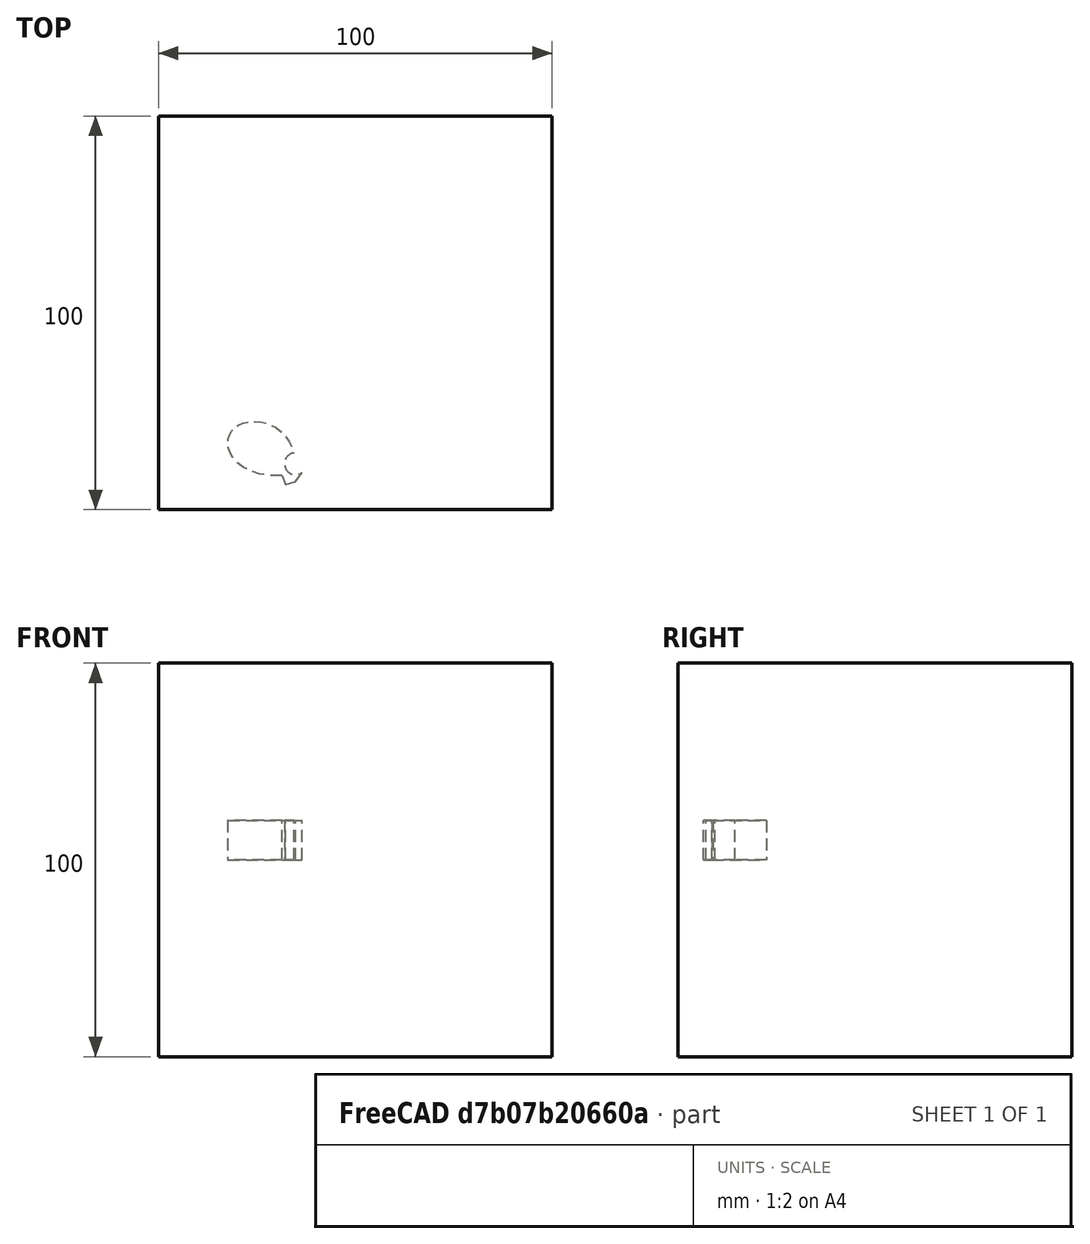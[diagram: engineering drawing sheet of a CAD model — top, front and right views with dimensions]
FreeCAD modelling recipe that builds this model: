
FCSTD DOCUMENT  (FreeCAD 0.19RUnknown)
Label: mirrorTest-3
License: All rights reserved
LicenseURL: http://en.wikipedia.org/wiki/All_rights_reserved
objects: App::DocumentObjectGroupPython×1248, Part::Mirroring×2, App::Part×2, Part::FeaturePython×1, Sketcher::SketchObject×1, Part::Extrusion×1
note: 5 computed .brp shape members not serialized (recipe doc carries the construction recipe); baked Part::Feature solids carry a one-line shape summary decoded from their .brp

FEATURE [App::DocumentObjectGroupPython] HALFPI  # scripted group (container) (typed FeaturePython)
  name = HALFPI
  value = pi/2.
FEATURE [App::DocumentObjectGroupPython] PI  # scripted group (container) (typed FeaturePython)
  name = PI
  value = 1.*pi
FEATURE [App::DocumentObjectGroupPython] TWOPI  # scripted group (container) (typed FeaturePython)
  name = TWOPI
  value = 2.*pi
FEATURE [App::DocumentObjectGroupPython] Constants  # scripted group (container) (typed FeaturePython)
  Group = -> [HALFPI,PI,TWOPI]
FEATURE [App::DocumentObjectGroupPython] Variables  # scripted group (container) (typed FeaturePython)
FEATURE [App::DocumentObjectGroupPython] Quantities  # scripted group (container) (typed FeaturePython)
FEATURE [App::DocumentObjectGroupPython] Isotopes  # scripted group (container) (typed FeaturePython)
FEATURE [App::DocumentObjectGroupPython] Elements  # scripted group (container) (typed FeaturePython)
FEATURE [App::DocumentObjectGroupPython] G4Isotopes  # scripted group (container) (typed FeaturePython)
FEATURE [App::DocumentObjectGroupPython] H_element  # scripted group (container) (typed FeaturePython)
  Z = 1
  atom_value = 1.008
  formula = H
  name = H_element
FEATURE [App::DocumentObjectGroupPython] He_element  # scripted group (container) (typed FeaturePython)
  Z = 2
  atom_value = 4.0026
  formula = He
  name = He_element
FEATURE [App::DocumentObjectGroupPython] Li_element  # scripted group (container) (typed FeaturePython)
  Z = 3
  atom_value = 6.94
  formula = Li
  name = Li_element
FEATURE [App::DocumentObjectGroupPython] Be_element  # scripted group (container) (typed FeaturePython)
  Z = 4
  atom_value = 9.01218
  formula = Be
  name = Be_element
FEATURE [App::DocumentObjectGroupPython] B_element  # scripted group (container) (typed FeaturePython)
  Z = 5
  atom_value = 10.81
  formula = B
  name = B_element
FEATURE [App::DocumentObjectGroupPython] C_element  # scripted group (container) (typed FeaturePython)
  Z = 6
  atom_value = 12.011
  formula = C
  name = C_element
FEATURE [App::DocumentObjectGroupPython] N_element  # scripted group (container) (typed FeaturePython)
  Z = 7
  atom_value = 14.007
  formula = N
  name = N_element
FEATURE [App::DocumentObjectGroupPython] O_element  # scripted group (container) (typed FeaturePython)
  Z = 8
  atom_value = 15.999
  formula = O
  name = O_element
FEATURE [App::DocumentObjectGroupPython] F_element  # scripted group (container) (typed FeaturePython)
  Z = 9
  atom_value = 18.9984
  formula = F
  name = F_element
FEATURE [App::DocumentObjectGroupPython] Ne_element  # scripted group (container) (typed FeaturePython)
  Z = 10
  atom_value = 20.1797
  formula = Ne
  name = Ne_element
FEATURE [App::DocumentObjectGroupPython] Na_element  # scripted group (container) (typed FeaturePython)
  Z = 11
  atom_value = 22.9898
  formula = Na
  name = Na_element
FEATURE [App::DocumentObjectGroupPython] Mg_element  # scripted group (container) (typed FeaturePython)
  Z = 12
  atom_value = 24.305
  formula = Mg
  name = Mg_element
FEATURE [App::DocumentObjectGroupPython] Al_element  # scripted group (container) (typed FeaturePython)
  Z = 13
  atom_value = 26.9815
  formula = Al
  name = Al_element
FEATURE [App::DocumentObjectGroupPython] Si_element  # scripted group (container) (typed FeaturePython)
  Z = 14
  atom_value = 28.085
  formula = Si
  name = Si_element
FEATURE [App::DocumentObjectGroupPython] P_element  # scripted group (container) (typed FeaturePython)
  Z = 15
  atom_value = 30.9738
  formula = P
  name = P_element
FEATURE [App::DocumentObjectGroupPython] S_element  # scripted group (container) (typed FeaturePython)
  Z = 16
  atom_value = 32.06
  formula = S
  name = S_element
FEATURE [App::DocumentObjectGroupPython] Cl_element  # scripted group (container) (typed FeaturePython)
  Z = 17
  atom_value = 35.45
  formula = Cl
  name = Cl_element
FEATURE [App::DocumentObjectGroupPython] Ar_element  # scripted group (container) (typed FeaturePython)
  Z = 18
  atom_value = 39.95
  formula = Ar
  name = Ar_element
FEATURE [App::DocumentObjectGroupPython] K_element  # scripted group (container) (typed FeaturePython)
  Z = 19
  atom_value = 39.0983
  formula = K
  name = K_element
FEATURE [App::DocumentObjectGroupPython] Ca_element  # scripted group (container) (typed FeaturePython)
  Z = 20
  atom_value = 40.078
  formula = Ca
  name = Ca_element
FEATURE [App::DocumentObjectGroupPython] Sc_element  # scripted group (container) (typed FeaturePython)
  Z = 21
  atom_value = 44.9559
  formula = Sc
  name = Sc_element
FEATURE [App::DocumentObjectGroupPython] Ti_element  # scripted group (container) (typed FeaturePython)
  Z = 22
  atom_value = 47.867
  formula = Ti
  name = Ti_element
FEATURE [App::DocumentObjectGroupPython] V_element  # scripted group (container) (typed FeaturePython)
  Z = 23
  atom_value = 50.9415
  formula = V
  name = V_element
FEATURE [App::DocumentObjectGroupPython] Cr_element  # scripted group (container) (typed FeaturePython)
  Z = 24
  atom_value = 51.9961
  formula = Cr
  name = Cr_element
FEATURE [App::DocumentObjectGroupPython] Mn_element  # scripted group (container) (typed FeaturePython)
  Z = 25
  atom_value = 54.938
  formula = Mn
  name = Mn_element
FEATURE [App::DocumentObjectGroupPython] Fe_element  # scripted group (container) (typed FeaturePython)
  Z = 26
  atom_value = 55.845
  formula = Fe
  name = Fe_element
FEATURE [App::DocumentObjectGroupPython] Co_element  # scripted group (container) (typed FeaturePython)
  Z = 27
  atom_value = 58.9332
  formula = Co
  name = Co_element
FEATURE [App::DocumentObjectGroupPython] Ni_element  # scripted group (container) (typed FeaturePython)
  Z = 28
  atom_value = 58.6934
  formula = Ni
  name = Ni_element
FEATURE [App::DocumentObjectGroupPython] Cu_element  # scripted group (container) (typed FeaturePython)
  Z = 29
  atom_value = 63.546
  formula = Cu
  name = Cu_element
FEATURE [App::DocumentObjectGroupPython] Zn_element  # scripted group (container) (typed FeaturePython)
  Z = 30
  atom_value = 65.38
  formula = Zn
  name = Zn_element
FEATURE [App::DocumentObjectGroupPython] Ga_element  # scripted group (container) (typed FeaturePython)
  Z = 31
  atom_value = 69.723
  formula = Ga
  name = Ga_element
FEATURE [App::DocumentObjectGroupPython] Ge_element  # scripted group (container) (typed FeaturePython)
  Z = 32
  atom_value = 72.63
  formula = Ge
  name = Ge_element
FEATURE [App::DocumentObjectGroupPython] As_element  # scripted group (container) (typed FeaturePython)
  Z = 33
  atom_value = 74.9216
  formula = As
  name = As_element
FEATURE [App::DocumentObjectGroupPython] Se_element  # scripted group (container) (typed FeaturePython)
  Z = 34
  atom_value = 78.971
  formula = Se
  name = Se_element
FEATURE [App::DocumentObjectGroupPython] Br_element  # scripted group (container) (typed FeaturePython)
  Z = 35
  atom_value = 79.904
  formula = Br
  name = Br_element
FEATURE [App::DocumentObjectGroupPython] Kr_element  # scripted group (container) (typed FeaturePython)
  Z = 36
  atom_value = 83.798
  formula = Kr
  name = Kr_element
FEATURE [App::DocumentObjectGroupPython] Rb_element  # scripted group (container) (typed FeaturePython)
  Z = 37
  atom_value = 85.4678
  formula = Rb
  name = Rb_element
FEATURE [App::DocumentObjectGroupPython] Sr_element  # scripted group (container) (typed FeaturePython)
  Z = 38
  atom_value = 87.62
  formula = Sr
  name = Sr_element
FEATURE [App::DocumentObjectGroupPython] Y_element  # scripted group (container) (typed FeaturePython)
  Z = 39
  atom_value = 88.9058
  formula = Y
  name = Y_element
FEATURE [App::DocumentObjectGroupPython] Zr_element  # scripted group (container) (typed FeaturePython)
  Z = 40
  atom_value = 91.224
  formula = Zr
  name = Zr_element
FEATURE [App::DocumentObjectGroupPython] Nb_element  # scripted group (container) (typed FeaturePython)
  Z = 41
  atom_value = 92.9064
  formula = Nb
  name = Nb_element
FEATURE [App::DocumentObjectGroupPython] Mo_element  # scripted group (container) (typed FeaturePython)
  Z = 42
  atom_value = 95.95
  formula = Mo
  name = Mo_element
FEATURE [App::DocumentObjectGroupPython] Tc_element  # scripted group (container) (typed FeaturePython)
  Z = 43
  atom_value = 97
  formula = Tc
  name = Tc_element
FEATURE [App::DocumentObjectGroupPython] Ru_element  # scripted group (container) (typed FeaturePython)
  Z = 44
  atom_value = 101.07
  formula = Ru
  name = Ru_element
FEATURE [App::DocumentObjectGroupPython] Rh_element  # scripted group (container) (typed FeaturePython)
  Z = 45
  atom_value = 102.905
  formula = Rh
  name = Rh_element
FEATURE [App::DocumentObjectGroupPython] Pd_element  # scripted group (container) (typed FeaturePython)
  Z = 46
  atom_value = 106.42
  formula = Pd
  name = Pd_element
FEATURE [App::DocumentObjectGroupPython] Ag_element  # scripted group (container) (typed FeaturePython)
  Z = 47
  atom_value = 107.868
  formula = Ag
  name = Ag_element
FEATURE [App::DocumentObjectGroupPython] Cd_element  # scripted group (container) (typed FeaturePython)
  Z = 48
  atom_value = 112.414
  formula = Cd
  name = Cd_element
FEATURE [App::DocumentObjectGroupPython] In_element  # scripted group (container) (typed FeaturePython)
  Z = 49
  atom_value = 114.818
  formula = In
  name = In_element
FEATURE [App::DocumentObjectGroupPython] Sn_element  # scripted group (container) (typed FeaturePython)
  Z = 50
  atom_value = 118.71
  formula = Sn
  name = Sn_element
FEATURE [App::DocumentObjectGroupPython] Sb_element  # scripted group (container) (typed FeaturePython)
  Z = 51
  atom_value = 121.76
  formula = Sb
  name = Sb_element
FEATURE [App::DocumentObjectGroupPython] Te_element  # scripted group (container) (typed FeaturePython)
  Z = 52
  atom_value = 127.6
  formula = Te
  name = Te_element
FEATURE [App::DocumentObjectGroupPython] I_element  # scripted group (container) (typed FeaturePython)
  Z = 53
  atom_value = 126.904
  formula = I
  name = I_element
FEATURE [App::DocumentObjectGroupPython] Xe_element  # scripted group (container) (typed FeaturePython)
  Z = 54
  atom_value = 131.293
  formula = Xe
  name = Xe_element
FEATURE [App::DocumentObjectGroupPython] Cs_element  # scripted group (container) (typed FeaturePython)
  Z = 55
  atom_value = 132.905
  formula = Cs
  name = Cs_element
FEATURE [App::DocumentObjectGroupPython] Ba_element  # scripted group (container) (typed FeaturePython)
  Z = 56
  atom_value = 137.327
  formula = Ba
  name = Ba_element
FEATURE [App::DocumentObjectGroupPython] La_element  # scripted group (container) (typed FeaturePython)
  Z = 57
  atom_value = 138.905
  formula = La
  name = La_element
FEATURE [App::DocumentObjectGroupPython] Ce_element  # scripted group (container) (typed FeaturePython)
  Z = 58
  atom_value = 140.116
  formula = Ce
  name = Ce_element
FEATURE [App::DocumentObjectGroupPython] Pr_element  # scripted group (container) (typed FeaturePython)
  Z = 59
  atom_value = 140.908
  formula = Pr
  name = Pr_element
FEATURE [App::DocumentObjectGroupPython] Nd_element  # scripted group (container) (typed FeaturePython)
  Z = 60
  atom_value = 144.242
  formula = Nd
  name = Nd_element
FEATURE [App::DocumentObjectGroupPython] Pm_element  # scripted group (container) (typed FeaturePython)
  Z = 61
  atom_value = 145
  formula = Pm
  name = Pm_element
FEATURE [App::DocumentObjectGroupPython] Sm_element  # scripted group (container) (typed FeaturePython)
  Z = 62
  atom_value = 150.36
  formula = Sm
  name = Sm_element
FEATURE [App::DocumentObjectGroupPython] Eu_element  # scripted group (container) (typed FeaturePython)
  Z = 63
  atom_value = 151.964
  formula = Eu
  name = Eu_element
FEATURE [App::DocumentObjectGroupPython] Gd_element  # scripted group (container) (typed FeaturePython)
  Z = 64
  atom_value = 157.25
  formula = Gd
  name = Gd_element
FEATURE [App::DocumentObjectGroupPython] Tb_element  # scripted group (container) (typed FeaturePython)
  Z = 65
  atom_value = 158.925
  formula = Tb
  name = Tb_element
FEATURE [App::DocumentObjectGroupPython] Dy_element  # scripted group (container) (typed FeaturePython)
  Z = 66
  atom_value = 162.5
  formula = Dy
  name = Dy_element
FEATURE [App::DocumentObjectGroupPython] Ho_element  # scripted group (container) (typed FeaturePython)
  Z = 67
  atom_value = 164.93
  formula = Ho
  name = Ho_element
FEATURE [App::DocumentObjectGroupPython] Er_element  # scripted group (container) (typed FeaturePython)
  Z = 68
  atom_value = 167.259
  formula = Er
  name = Er_element
FEATURE [App::DocumentObjectGroupPython] Tm_element  # scripted group (container) (typed FeaturePython)
  Z = 69
  atom_value = 168.934
  formula = Tm
  name = Tm_element
FEATURE [App::DocumentObjectGroupPython] Yb_element  # scripted group (container) (typed FeaturePython)
  Z = 70
  atom_value = 173.045
  formula = Yb
  name = Yb_element
FEATURE [App::DocumentObjectGroupPython] Lu_element  # scripted group (container) (typed FeaturePython)
  Z = 71
  atom_value = 174.967
  formula = Lu
  name = Lu_element
FEATURE [App::DocumentObjectGroupPython] Hf_element  # scripted group (container) (typed FeaturePython)
  Z = 72
  atom_value = 178.49
  formula = Hf
  name = Hf_element
FEATURE [App::DocumentObjectGroupPython] Ta_element  # scripted group (container) (typed FeaturePython)
  Z = 73
  atom_value = 180.948
  formula = Ta
  name = Ta_element
FEATURE [App::DocumentObjectGroupPython] W_element  # scripted group (container) (typed FeaturePython)
  Z = 74
  atom_value = 183.84
  formula = W
  name = W_element
FEATURE [App::DocumentObjectGroupPython] Re_element  # scripted group (container) (typed FeaturePython)
  Z = 75
  atom_value = 186.207
  formula = Re
  name = Re_element
FEATURE [App::DocumentObjectGroupPython] Os_element  # scripted group (container) (typed FeaturePython)
  Z = 76
  atom_value = 190.23
  formula = Os
  name = Os_element
FEATURE [App::DocumentObjectGroupPython] Ir_element  # scripted group (container) (typed FeaturePython)
  Z = 77
  atom_value = 192.217
  formula = Ir
  name = Ir_element
FEATURE [App::DocumentObjectGroupPython] Pt_element  # scripted group (container) (typed FeaturePython)
  Z = 78
  atom_value = 195.084
  formula = Pt
  name = Pt_element
FEATURE [App::DocumentObjectGroupPython] Au_element  # scripted group (container) (typed FeaturePython)
  Z = 79
  atom_value = 196.967
  formula = Au
  name = Au_element
FEATURE [App::DocumentObjectGroupPython] Hg_element  # scripted group (container) (typed FeaturePython)
  Z = 80
  atom_value = 200.592
  formula = Hg
  name = Hg_element
FEATURE [App::DocumentObjectGroupPython] Tl_element  # scripted group (container) (typed FeaturePython)
  Z = 81
  atom_value = 204.38
  formula = Tl
  name = Tl_element
FEATURE [App::DocumentObjectGroupPython] Pb_element  # scripted group (container) (typed FeaturePython)
  Z = 82
  atom_value = 207.2
  formula = Pb
  name = Pb_element
FEATURE [App::DocumentObjectGroupPython] Bi_element  # scripted group (container) (typed FeaturePython)
  Z = 83
  atom_value = 208.98
  formula = Bi
  name = Bi_element
FEATURE [App::DocumentObjectGroupPython] Po_element  # scripted group (container) (typed FeaturePython)
  Z = 84
  atom_value = 209
  formula = Po
  name = Po_element
FEATURE [App::DocumentObjectGroupPython] At_element  # scripted group (container) (typed FeaturePython)
  Z = 85
  atom_value = 210
  formula = At
  name = At_element
FEATURE [App::DocumentObjectGroupPython] Rn_element  # scripted group (container) (typed FeaturePython)
  Z = 86
  atom_value = 222
  formula = Rn
  name = Rn_element
FEATURE [App::DocumentObjectGroupPython] Fr_element  # scripted group (container) (typed FeaturePython)
  Z = 87
  atom_value = 223
  formula = Fr
  name = Fr_element
FEATURE [App::DocumentObjectGroupPython] Ra_element  # scripted group (container) (typed FeaturePython)
  Z = 88
  atom_value = 226
  formula = Ra
  name = Ra_element
FEATURE [App::DocumentObjectGroupPython] Ac_element  # scripted group (container) (typed FeaturePython)
  Z = 89
  atom_value = 227
  formula = Ac
  name = Ac_element
FEATURE [App::DocumentObjectGroupPython] Th_element  # scripted group (container) (typed FeaturePython)
  Z = 90
  atom_value = 232.038
  formula = Th
  name = Th_element
FEATURE [App::DocumentObjectGroupPython] Pa_element  # scripted group (container) (typed FeaturePython)
  Z = 91
  atom_value = 231.036
  formula = Pa
  name = Pa_element
FEATURE [App::DocumentObjectGroupPython] U_element  # scripted group (container) (typed FeaturePython)
  Z = 92
  atom_value = 238.029
  formula = U
  name = U_element
FEATURE [App::DocumentObjectGroupPython] Np_element  # scripted group (container) (typed FeaturePython)
  Z = 93
  atom_value = 237
  formula = Np
  name = Np_element
FEATURE [App::DocumentObjectGroupPython] Pu_element  # scripted group (container) (typed FeaturePython)
  Z = 94
  atom_value = 244
  formula = Pu
  name = Pu_element
FEATURE [App::DocumentObjectGroupPython] Am_element  # scripted group (container) (typed FeaturePython)
  Z = 95
  atom_value = 243
  formula = Am
  name = Am_element
FEATURE [App::DocumentObjectGroupPython] Cm_element  # scripted group (container) (typed FeaturePython)
  Z = 96
  atom_value = 247
  formula = Cm
  name = Cm_element
FEATURE [App::DocumentObjectGroupPython] Bk_element  # scripted group (container) (typed FeaturePython)
  Z = 97
  atom_value = 247
  formula = Bk
  name = Bk_element
FEATURE [App::DocumentObjectGroupPython] Cf_element  # scripted group (container) (typed FeaturePython)
  Z = 98
  atom_value = 251
  formula = Cf
  name = Cf_element
FEATURE [App::DocumentObjectGroupPython] G4Elements  # scripted group (container) (typed FeaturePython)
  Group = -> [H_element,He_element,Li_element,Be_element,B_element,C_element,N_element,O_element,F_element,Ne_element,Na_element,Mg_element,Al_element,Si_element,P_element,S_element,Cl_element,Ar_element,K_element,Ca_element,Sc_element,Ti_element,V_element,Cr_element,Mn_element,Fe_element,Co_element,Ni_element,Cu_element,Zn_element,Ga_element,Ge_element,As_element,Se_element,Br_element,Kr_element,Rb_element,+61 more]
FEATURE [App::DocumentObjectGroupPython] H_element001  label="H_element : 0.101"  # scripted group (container) (typed FeaturePython)
  n = 0.101327
FEATURE [App::DocumentObjectGroupPython] C_element001  label="C_element : 0.775"  # scripted group (container) (typed FeaturePython)
  n = 0.7755
FEATURE [App::DocumentObjectGroupPython] N_element001  label="N_element : 0.035"  # scripted group (container) (typed FeaturePython)
  n = 0.035057
FEATURE [App::DocumentObjectGroupPython] O_element001  label="O_element : 0.052"  # scripted group (container) (typed FeaturePython)
  n = 0.0523159
FEATURE [App::DocumentObjectGroupPython] F_element001  label="F_element : 0.017"  # scripted group (container) (typed FeaturePython)
  n = 0.017422
FEATURE [App::DocumentObjectGroupPython] Ca_element001  label="Ca_element : 0.018"  # scripted group (container) (typed FeaturePython)
  n = 0.018378
FEATURE [App::DocumentObjectGroupPython] G4_A_150_TISSUE  label="G4_A-150_TISSUE"  # scripted group (container) (typed FeaturePython)
  Dunit = g/cm3
  Dvalue = 1.127
  Group = -> [H_element001,C_element001,N_element001,O_element001,F_element001,Ca_element001]
  conduct = 2
  density = 1
  expand = 3
  formula = G4_A-150_TISSUE
  name = G4_A-150_TISSUE
  specific = 4
FEATURE [App::DocumentObjectGroupPython] C_element002  label="C_element : 3"  # scripted group (container) (typed FeaturePython)
  n = 3
  ref = C_element
FEATURE [App::DocumentObjectGroupPython] H_element002  label="H_element : 6"  # scripted group (container) (typed FeaturePython)
  n = 6
  ref = H_element
FEATURE [App::DocumentObjectGroupPython] O_element002  label="O_element : 1"  # scripted group (container) (typed FeaturePython)
  n = 1
  ref = O_element
FEATURE [App::DocumentObjectGroupPython] G4_ACETONE  # scripted group (container) (typed FeaturePython)
  Dunit = g/cm3
  Dvalue = 0.7899
  Group = -> [C_element002,H_element002,O_element002]
  conduct = 2
  density = 1
  expand = 3
  formula = G4_ACETONE
  name = G4_ACETONE
  specific = 4
FEATURE [App::DocumentObjectGroupPython] C_element003  label="C_element : 2"  # scripted group (container) (typed FeaturePython)
  n = 2
  ref = C_element
FEATURE [App::DocumentObjectGroupPython] H_element003  label="H_element : 2"  # scripted group (container) (typed FeaturePython)
  n = 2
  ref = H_element
FEATURE [App::DocumentObjectGroupPython] G4_ACETYLENE  # scripted group (container) (typed FeaturePython)
  Dunit = g/cm3
  Dvalue = 0.0010967
  Group = -> [C_element003,H_element003]
  conduct = 2
  density = 1
  expand = 3
  formula = G4_ACETYLENE
  name = G4_ACETYLENE
  specific = 4
FEATURE [App::DocumentObjectGroupPython] C_element004  label="C_element : 5"  # scripted group (container) (typed FeaturePython)
  n = 5
  ref = C_element
FEATURE [App::DocumentObjectGroupPython] H_element004  label="H_element : 5"  # scripted group (container) (typed FeaturePython)
  n = 5
  ref = H_element
FEATURE [App::DocumentObjectGroupPython] N_element002  label="N_element : 5"  # scripted group (container) (typed FeaturePython)
  n = 5
  ref = N_element
FEATURE [App::DocumentObjectGroupPython] G4_ADENINE  # scripted group (container) (typed FeaturePython)
  Dunit = g/cm3
  Dvalue = 1.6
  Group = -> [C_element004,H_element004,N_element002]
  conduct = 2
  density = 1
  expand = 3
  formula = G4_ADENINE
  name = G4_ADENINE
  specific = 4
FEATURE [App::DocumentObjectGroupPython] H_element005  label="H_element : 0.114"  # scripted group (container) (typed FeaturePython)
  n = 0.114
FEATURE [App::DocumentObjectGroupPython] C_element005  label="C_element : 0.598"  # scripted group (container) (typed FeaturePython)
  n = 0.598
FEATURE [App::DocumentObjectGroupPython] N_element003  label="N_element : 0.007"  # scripted group (container) (typed FeaturePython)
  n = 0.007
FEATURE [App::DocumentObjectGroupPython] O_element003  label="O_element : 0.278"  # scripted group (container) (typed FeaturePython)
  n = 0.278
FEATURE [App::DocumentObjectGroupPython] Na_element001  label="Na_element : 0.001"  # scripted group (container) (typed FeaturePython)
  n = 0.001
FEATURE [App::DocumentObjectGroupPython] S_element001  label="S_element : 0.001"  # scripted group (container) (typed FeaturePython)
  n = 0.001
FEATURE [App::DocumentObjectGroupPython] Cl_element001  label="Cl_element : 0.001"  # scripted group (container) (typed FeaturePython)
  n = 0.001
FEATURE [App::DocumentObjectGroupPython] G4_ADIPOSE_TISSUE_ICRP  # scripted group (container) (typed FeaturePython)
  Dunit = g/cm3
  Dvalue = 0.95
  Group = -> [H_element005,C_element005,N_element003,O_element003,Na_element001,S_element001,Cl_element001]
  conduct = 2
  density = 1
  expand = 3
  formula = G4_ADIPOSE_TISSUE_ICRP
  name = G4_ADIPOSE_TISSUE_ICRP
  specific = 4
FEATURE [App::DocumentObjectGroupPython] C_element006  label="C_element : 0.000"  # scripted group (container) (typed FeaturePython)
  n = 0.000124
FEATURE [App::DocumentObjectGroupPython] N_element004  label="N_element : 0.755"  # scripted group (container) (typed FeaturePython)
  n = 0.755268
FEATURE [App::DocumentObjectGroupPython] O_element004  label="O_element : 0.232"  # scripted group (container) (typed FeaturePython)
  n = 0.231781
FEATURE [App::DocumentObjectGroupPython] Ar_element001  label="Ar_element : 0.013"  # scripted group (container) (typed FeaturePython)
  n = 0.012827
FEATURE [App::DocumentObjectGroupPython] G4_AIR  # scripted group (container) (typed FeaturePython)
  Dunit = g/cm3
  Dvalue = 0.00120479
  Group = -> [C_element006,N_element004,O_element004,Ar_element001]
  conduct = 2
  density = 1
  expand = 3
  formula = G4_AIR
  name = G4_AIR
  specific = 4
FEATURE [App::DocumentObjectGroupPython] C_element007  label="C_element : 006"  # scripted group (container) (typed FeaturePython)
  n = 3
  ref = C_element
FEATURE [App::DocumentObjectGroupPython] H_element006  label="H_element : 7"  # scripted group (container) (typed FeaturePython)
  n = 7
  ref = H_element
FEATURE [App::DocumentObjectGroupPython] N_element005  label="N_element : 1"  # scripted group (container) (typed FeaturePython)
  n = 1
  ref = N_element
FEATURE [App::DocumentObjectGroupPython] O_element005  label="O_element : 2"  # scripted group (container) (typed FeaturePython)
  n = 2
  ref = O_element
FEATURE [App::DocumentObjectGroupPython] G4_ALANINE  # scripted group (container) (typed FeaturePython)
  Dunit = g/cm3
  Dvalue = 1.42
  Group = -> [C_element007,H_element006,N_element005,O_element005]
  conduct = 2
  density = 1
  expand = 3
  formula = G4_ALANINE
  name = G4_ALANINE
  specific = 4
FEATURE [App::DocumentObjectGroupPython] Al_element001  label="Al_element : 2"  # scripted group (container) (typed FeaturePython)
  n = 2
  ref = Al_element
FEATURE [App::DocumentObjectGroupPython] O_element006  label="O_element : 3"  # scripted group (container) (typed FeaturePython)
  n = 3
  ref = O_element
FEATURE [App::DocumentObjectGroupPython] G4_ALUMINUM_OXIDE  # scripted group (container) (typed FeaturePython)
  Dunit = g/cm3
  Dvalue = 3.97
  Group = -> [Al_element001,O_element006]
  conduct = 2
  density = 1
  expand = 3
  formula = G4_ALUMINUM_OXIDE
  name = G4_ALUMINUM_OXIDE
  specific = 4
FEATURE [App::DocumentObjectGroupPython] H_element007  label="H_element : 0.106"  # scripted group (container) (typed FeaturePython)
  n = 0.10593
FEATURE [App::DocumentObjectGroupPython] C_element008  label="C_element : 0.789"  # scripted group (container) (typed FeaturePython)
  n = 0.788974
FEATURE [App::DocumentObjectGroupPython] O_element007  label="O_element : 0.105"  # scripted group (container) (typed FeaturePython)
  n = 0.105096
FEATURE [App::DocumentObjectGroupPython] G4_AMBER  # scripted group (container) (typed FeaturePython)
  Dunit = g/cm3
  Dvalue = 1.1
  Group = -> [H_element007,C_element008,O_element007]
  conduct = 2
  density = 1
  expand = 3
  formula = G4_AMBER
  name = G4_AMBER
  specific = 4
FEATURE [App::DocumentObjectGroupPython] N_element006  label="N_element : 006"  # scripted group (container) (typed FeaturePython)
  n = 1
  ref = N_element
FEATURE [App::DocumentObjectGroupPython] H_element008  label="H_element : 3"  # scripted group (container) (typed FeaturePython)
  n = 3
  ref = H_element
FEATURE [App::DocumentObjectGroupPython] G4_AMMONIA  # scripted group (container) (typed FeaturePython)
  Dunit = g/cm3
  Dvalue = 0.000826019
  Group = -> [N_element006,H_element008]
  conduct = 2
  density = 1
  expand = 3
  formula = G4_AMMONIA
  name = G4_AMMONIA
  specific = 4
FEATURE [App::DocumentObjectGroupPython] C_element009  label="C_element : 6"  # scripted group (container) (typed FeaturePython)
  n = 6
  ref = C_element
FEATURE [App::DocumentObjectGroupPython] H_element009  label="H_element : 008"  # scripted group (container) (typed FeaturePython)
  n = 7
  ref = H_element
FEATURE [App::DocumentObjectGroupPython] N_element007  label="N_element : 007"  # scripted group (container) (typed FeaturePython)
  n = 1
  ref = N_element
FEATURE [App::DocumentObjectGroupPython] G4_ANILINE  # scripted group (container) (typed FeaturePython)
  Dunit = g/cm3
  Dvalue = 1.0235
  Group = -> [C_element009,H_element009,N_element007]
  conduct = 2
  density = 1
  expand = 3
  formula = G4_ANILINE
  name = G4_ANILINE
  specific = 4
FEATURE [App::DocumentObjectGroupPython] C_element010  label="C_element : 14"  # scripted group (container) (typed FeaturePython)
  n = 14
  ref = C_element
FEATURE [App::DocumentObjectGroupPython] H_element010  label="H_element : 10"  # scripted group (container) (typed FeaturePython)
  n = 10
  ref = H_element
FEATURE [App::DocumentObjectGroupPython] G4_ANTHRACENE  # scripted group (container) (typed FeaturePython)
  Dunit = g/cm3
  Dvalue = 1.283
  Group = -> [C_element010,H_element010]
  conduct = 2
  density = 1
  expand = 3
  formula = G4_ANTHRACENE
  name = G4_ANTHRACENE
  specific = 4
FEATURE [App::DocumentObjectGroupPython] H_element011  label="H_element : 0.065"  # scripted group (container) (typed FeaturePython)
  n = 0.0654709
FEATURE [App::DocumentObjectGroupPython] C_element011  label="C_element : 0.537"  # scripted group (container) (typed FeaturePython)
  n = 0.536944
FEATURE [App::DocumentObjectGroupPython] N_element008  label="N_element : 0.021"  # scripted group (container) (typed FeaturePython)
  n = 0.0215
FEATURE [App::DocumentObjectGroupPython] O_element008  label="O_element : 0.032"  # scripted group (container) (typed FeaturePython)
  n = 0.032085
FEATURE [App::DocumentObjectGroupPython] F_element002  label="F_element : 0.167"  # scripted group (container) (typed FeaturePython)
  n = 0.167411
FEATURE [App::DocumentObjectGroupPython] Ca_element002  label="Ca_element : 0.177"  # scripted group (container) (typed FeaturePython)
  n = 0.176589
FEATURE [App::DocumentObjectGroupPython] G4_B_100_BONE  label="G4_B-100_BONE"  # scripted group (container) (typed FeaturePython)
  Dunit = g/cm3
  Dvalue = 1.45
  Group = -> [H_element011,C_element011,N_element008,O_element008,F_element002,Ca_element002]
  conduct = 2
  density = 1
  expand = 3
  formula = G4_B-100_BONE
  name = G4_B-100_BONE
  specific = 4
FEATURE [App::DocumentObjectGroupPython] H_element012  label="H_element : 0.057"  # scripted group (container) (typed FeaturePython)
  n = 0.057441
FEATURE [App::DocumentObjectGroupPython] C_element012  label="C_element : 0.790"  # scripted group (container) (typed FeaturePython)
  n = 0.774591
FEATURE [App::DocumentObjectGroupPython] O_element009  label="O_element : 0.168"  # scripted group (container) (typed FeaturePython)
  n = 0.167968
FEATURE [App::DocumentObjectGroupPython] G4_BAKELITE  # scripted group (container) (typed FeaturePython)
  Dunit = g/cm3
  Dvalue = 1.25
  Group = -> [H_element012,C_element012,O_element009]
  conduct = 2
  density = 1
  expand = 3
  formula = G4_BAKELITE
  name = G4_BAKELITE
  specific = 4
FEATURE [App::DocumentObjectGroupPython] Ba_element001  label="Ba_element : 1"  # scripted group (container) (typed FeaturePython)
  n = 1
  ref = Ba_element
FEATURE [App::DocumentObjectGroupPython] F_element003  label="F_element : 2"  # scripted group (container) (typed FeaturePython)
  n = 2
  ref = F_element
FEATURE [App::DocumentObjectGroupPython] G4_BARIUM_FLUORIDE  # scripted group (container) (typed FeaturePython)
  Dunit = g/cm3
  Dvalue = 4.89
  Group = -> [Ba_element001,F_element003]
  conduct = 2
  density = 1
  expand = 3
  formula = G4_BARIUM_FLUORIDE
  name = G4_BARIUM_FLUORIDE
  specific = 4
FEATURE [App::DocumentObjectGroupPython] Ba_element002  label="Ba_element : 002"  # scripted group (container) (typed FeaturePython)
  n = 1
  ref = Ba_element
FEATURE [App::DocumentObjectGroupPython] S_element002  label="S_element : 1"  # scripted group (container) (typed FeaturePython)
  n = 1
  ref = S_element
FEATURE [App::DocumentObjectGroupPython] O_element010  label="O_element : 4"  # scripted group (container) (typed FeaturePython)
  n = 4
  ref = O_element
FEATURE [App::DocumentObjectGroupPython] G4_BARIUM_SULFATE  # scripted group (container) (typed FeaturePython)
  Dunit = g/cm3
  Dvalue = 4.5
  Group = -> [Ba_element002,S_element002,O_element010]
  conduct = 2
  density = 1
  expand = 3
  formula = G4_BARIUM_SULFATE
  name = G4_BARIUM_SULFATE
  specific = 4
FEATURE [App::DocumentObjectGroupPython] C_element013  label="C_element : 007"  # scripted group (container) (typed FeaturePython)
  n = 6
  ref = C_element
FEATURE [App::DocumentObjectGroupPython] H_element013  label="H_element : 009"  # scripted group (container) (typed FeaturePython)
  n = 6
  ref = H_element
FEATURE [App::DocumentObjectGroupPython] G4_BENZENE  # scripted group (container) (typed FeaturePython)
  Dunit = g/cm3
  Dvalue = 0.87865
  Group = -> [C_element013,H_element013]
  conduct = 2
  density = 1
  expand = 3
  formula = G4_BENZENE
  name = G4_BENZENE
  specific = 4
FEATURE [App::DocumentObjectGroupPython] Be_element001  label="Be_element : 1"  # scripted group (container) (typed FeaturePython)
  n = 1
  ref = Be_element
FEATURE [App::DocumentObjectGroupPython] O_element011  label="O_element : 005"  # scripted group (container) (typed FeaturePython)
  n = 1
  ref = O_element
FEATURE [App::DocumentObjectGroupPython] G4_BERYLLIUM_OXIDE  # scripted group (container) (typed FeaturePython)
  Dunit = g/cm3
  Dvalue = 3.01
  Group = -> [Be_element001,O_element011]
  conduct = 2
  density = 1
  expand = 3
  formula = G4_BERYLLIUM_OXIDE
  name = G4_BERYLLIUM_OXIDE
  specific = 4
FEATURE [App::DocumentObjectGroupPython] Bi_element001  label="Bi_element : 4"  # scripted group (container) (typed FeaturePython)
  n = 4
  ref = Bi_element
FEATURE [App::DocumentObjectGroupPython] Ge_element001  label="Ge_element : 3"  # scripted group (container) (typed FeaturePython)
  n = 3
  ref = Ge_element
FEATURE [App::DocumentObjectGroupPython] O_element012  label="O_element : 12"  # scripted group (container) (typed FeaturePython)
  n = 12
  ref = O_element
FEATURE [App::DocumentObjectGroupPython] G4_BGO  # scripted group (container) (typed FeaturePython)
  Dunit = g/cm3
  Dvalue = 7.13
  Group = -> [Bi_element001,Ge_element001,O_element012]
  conduct = 2
  density = 1
  expand = 3
  formula = G4_BGO
  name = G4_BGO
  specific = 4
FEATURE [App::DocumentObjectGroupPython] H_element014  label="H_element : 0.102"  # scripted group (container) (typed FeaturePython)
  n = 0.102
FEATURE [App::DocumentObjectGroupPython] C_element014  label="C_element : 0.110"  # scripted group (container) (typed FeaturePython)
  n = 0.11
FEATURE [App::DocumentObjectGroupPython] N_element009  label="N_element : 0.033"  # scripted group (container) (typed FeaturePython)
  n = 0.033
FEATURE [App::DocumentObjectGroupPython] O_element013  label="O_element : 0.745"  # scripted group (container) (typed FeaturePython)
  n = 0.745
FEATURE [App::DocumentObjectGroupPython] Na_element002  label="Na_element : 0.002"  # scripted group (container) (typed FeaturePython)
  n = 0.001
FEATURE [App::DocumentObjectGroupPython] P_element001  label="P_element : 0.001"  # scripted group (container) (typed FeaturePython)
  n = 0.001
FEATURE [App::DocumentObjectGroupPython] S_element003  label="S_element : 0.002"  # scripted group (container) (typed FeaturePython)
  n = 0.002
FEATURE [App::DocumentObjectGroupPython] Cl_element002  label="Cl_element : 0.003"  # scripted group (container) (typed FeaturePython)
  n = 0.003
FEATURE [App::DocumentObjectGroupPython] K_element001  label="K_element : 0.002"  # scripted group (container) (typed FeaturePython)
  n = 0.002
FEATURE [App::DocumentObjectGroupPython] Fe_element001  label="Fe_element : 0.001"  # scripted group (container) (typed FeaturePython)
  n = 0.001
FEATURE [App::DocumentObjectGroupPython] G4_BLOOD_ICRP  # scripted group (container) (typed FeaturePython)
  Dunit = g/cm3
  Dvalue = 1.06
  Group = -> [H_element014,C_element014,N_element009,O_element013,Na_element002,P_element001,S_element003,Cl_element002,K_element001,Fe_element001]
  conduct = 2
  density = 1
  expand = 3
  formula = G4_BLOOD_ICRP
  name = G4_BLOOD_ICRP
  specific = 4
FEATURE [App::DocumentObjectGroupPython] H_element015  label="H_element : 0.064"  # scripted group (container) (typed FeaturePython)
  n = 0.064
FEATURE [App::DocumentObjectGroupPython] C_element015  label="C_element : 0.278"  # scripted group (container) (typed FeaturePython)
  n = 0.278
FEATURE [App::DocumentObjectGroupPython] N_element010  label="N_element : 0.027"  # scripted group (container) (typed FeaturePython)
  n = 0.027
FEATURE [App::DocumentObjectGroupPython] O_element014  label="O_element : 0.410"  # scripted group (container) (typed FeaturePython)
  n = 0.41
FEATURE [App::DocumentObjectGroupPython] Mg_element001  label="Mg_element : 0.002"  # scripted group (container) (typed FeaturePython)
  n = 0.002
FEATURE [App::DocumentObjectGroupPython] P_element002  label="P_element : 0.070"  # scripted group (container) (typed FeaturePython)
  n = 0.07
FEATURE [App::DocumentObjectGroupPython] S_element004  label="S_element : 0.003"  # scripted group (container) (typed FeaturePython)
  n = 0.002
FEATURE [App::DocumentObjectGroupPython] Ca_element003  label="Ca_element : 0.147"  # scripted group (container) (typed FeaturePython)
  n = 0.147
FEATURE [App::DocumentObjectGroupPython] G4_BONE_COMPACT_ICRU  # scripted group (container) (typed FeaturePython)
  Dunit = g/cm3
  Dvalue = 1.85
  Group = -> [H_element015,C_element015,N_element010,O_element014,Mg_element001,P_element002,S_element004,Ca_element003]
  conduct = 2
  density = 1
  expand = 3
  formula = G4_BONE_COMPACT_ICRU
  name = G4_BONE_COMPACT_ICRU
  specific = 4
FEATURE [App::DocumentObjectGroupPython] H_element016  label="H_element : 0.034"  # scripted group (container) (typed FeaturePython)
  n = 0.034
FEATURE [App::DocumentObjectGroupPython] C_element016  label="C_element : 0.155"  # scripted group (container) (typed FeaturePython)
  n = 0.155
FEATURE [App::DocumentObjectGroupPython] N_element011  label="N_element : 0.042"  # scripted group (container) (typed FeaturePython)
  n = 0.042
FEATURE [App::DocumentObjectGroupPython] O_element015  label="O_element : 0.435"  # scripted group (container) (typed FeaturePython)
  n = 0.435
FEATURE [App::DocumentObjectGroupPython] Na_element003  label="Na_element : 0.003"  # scripted group (container) (typed FeaturePython)
  n = 0.001
FEATURE [App::DocumentObjectGroupPython] Mg_element002  label="Mg_element : 0.003"  # scripted group (container) (typed FeaturePython)
  n = 0.002
FEATURE [App::DocumentObjectGroupPython] P_element003  label="P_element : 0.103"  # scripted group (container) (typed FeaturePython)
  n = 0.103
FEATURE [App::DocumentObjectGroupPython] S_element005  label="S_element : 0.004"  # scripted group (container) (typed FeaturePython)
  n = 0.003
FEATURE [App::DocumentObjectGroupPython] Ca_element004  label="Ca_element : 0.225"  # scripted group (container) (typed FeaturePython)
  n = 0.225
FEATURE [App::DocumentObjectGroupPython] G4_BONE_CORTICAL_ICRP  # scripted group (container) (typed FeaturePython)
  Dunit = g/cm3
  Dvalue = 1.92
  Group = -> [H_element016,C_element016,N_element011,O_element015,Na_element003,Mg_element002,P_element003,S_element005,Ca_element004]
  conduct = 2
  density = 1
  expand = 3
  formula = G4_BONE_CORTICAL_ICRP
  name = G4_BONE_CORTICAL_ICRP
  specific = 4
FEATURE [App::DocumentObjectGroupPython] B_element001  label="B_element : 4"  # scripted group (container) (typed FeaturePython)
  n = 4
  ref = B_element
FEATURE [App::DocumentObjectGroupPython] C_element017  label="C_element : 1"  # scripted group (container) (typed FeaturePython)
  n = 1
  ref = C_element
FEATURE [App::DocumentObjectGroupPython] G4_BORON_CARBIDE  # scripted group (container) (typed FeaturePython)
  Dunit = g/cm3
  Dvalue = 2.52
  Group = -> [B_element001,C_element017]
  conduct = 2
  density = 1
  expand = 3
  formula = G4_BORON_CARBIDE
  name = G4_BORON_CARBIDE
  specific = 4
FEATURE [App::DocumentObjectGroupPython] B_element002  label="B_element : 2"  # scripted group (container) (typed FeaturePython)
  n = 2
  ref = B_element
FEATURE [App::DocumentObjectGroupPython] O_element016  label="O_element : 006"  # scripted group (container) (typed FeaturePython)
  n = 3
  ref = O_element
FEATURE [App::DocumentObjectGroupPython] G4_BORON_OXIDE  # scripted group (container) (typed FeaturePython)
  Dunit = g/cm3
  Dvalue = 1.812
  Group = -> [B_element002,O_element016]
  conduct = 2
  density = 1
  expand = 3
  formula = G4_BORON_OXIDE
  name = G4_BORON_OXIDE
  specific = 4
FEATURE [App::DocumentObjectGroupPython] H_element017  label="H_element : 0.107"  # scripted group (container) (typed FeaturePython)
  n = 0.107
FEATURE [App::DocumentObjectGroupPython] C_element018  label="C_element : 0.145"  # scripted group (container) (typed FeaturePython)
  n = 0.145
FEATURE [App::DocumentObjectGroupPython] N_element012  label="N_element : 0.022"  # scripted group (container) (typed FeaturePython)
  n = 0.022
FEATURE [App::DocumentObjectGroupPython] O_element017  label="O_element : 0.712"  # scripted group (container) (typed FeaturePython)
  n = 0.712
FEATURE [App::DocumentObjectGroupPython] Na_element004  label="Na_element : 0.004"  # scripted group (container) (typed FeaturePython)
  n = 0.002
FEATURE [App::DocumentObjectGroupPython] P_element004  label="P_element : 0.004"  # scripted group (container) (typed FeaturePython)
  n = 0.004
FEATURE [App::DocumentObjectGroupPython] S_element006  label="S_element : 0.005"  # scripted group (container) (typed FeaturePython)
  n = 0.002
FEATURE [App::DocumentObjectGroupPython] Cl_element003  label="Cl_element : 0.004"  # scripted group (container) (typed FeaturePython)
  n = 0.003
FEATURE [App::DocumentObjectGroupPython] K_element002  label="K_element : 0.003"  # scripted group (container) (typed FeaturePython)
  n = 0.003
FEATURE [App::DocumentObjectGroupPython] G4_BRAIN_ICRP  # scripted group (container) (typed FeaturePython)
  Dunit = g/cm3
  Dvalue = 1.04
  Group = -> [H_element017,C_element018,N_element012,O_element017,Na_element004,P_element004,S_element006,Cl_element003,K_element002]
  conduct = 2
  density = 1
  expand = 3
  formula = G4_BRAIN_ICRP
  name = G4_BRAIN_ICRP
  specific = 4
FEATURE [App::DocumentObjectGroupPython] C_element019  label="C_element : 4"  # scripted group (container) (typed FeaturePython)
  n = 4
  ref = C_element
FEATURE [App::DocumentObjectGroupPython] H_element018  label="H_element : 010"  # scripted group (container) (typed FeaturePython)
  n = 10
  ref = H_element
FEATURE [App::DocumentObjectGroupPython] G4_BUTANE  # scripted group (container) (typed FeaturePython)
  Dunit = g/cm3
  Dvalue = 0.00249343
  Group = -> [C_element019,H_element018]
  conduct = 2
  density = 1
  expand = 3
  formula = G4_BUTANE
  name = G4_BUTANE
  specific = 4
FEATURE [App::DocumentObjectGroupPython] C_element020  label="C_element : 008"  # scripted group (container) (typed FeaturePython)
  n = 4
  ref = C_element
FEATURE [App::DocumentObjectGroupPython] H_element019  label="H_element : 011"  # scripted group (container) (typed FeaturePython)
  n = 10
  ref = H_element
FEATURE [App::DocumentObjectGroupPython] O_element018  label="O_element : 007"  # scripted group (container) (typed FeaturePython)
  n = 1
  ref = O_element
FEATURE [App::DocumentObjectGroupPython] G4_N_BUTYL_ALCOHOL  label="G4_N-BUTYL_ALCOHOL"  # scripted group (container) (typed FeaturePython)
  Dunit = g/cm3
  Dvalue = 0.8098
  Group = -> [C_element020,H_element019,O_element018]
  conduct = 2
  density = 1
  expand = 3
  formula = G4_N-BUTYL_ALCOHOL
  name = G4_N-BUTYL_ALCOHOL
  specific = 4
FEATURE [App::DocumentObjectGroupPython] H_element020  label="H_element : 0.025"  # scripted group (container) (typed FeaturePython)
  n = 0.02468
FEATURE [App::DocumentObjectGroupPython] C_element021  label="C_element : 0.502"  # scripted group (container) (typed FeaturePython)
  n = 0.501611
FEATURE [App::DocumentObjectGroupPython] O_element019  label="O_element : 0.005"  # scripted group (container) (typed FeaturePython)
  n = 0.004527
FEATURE [App::DocumentObjectGroupPython] F_element004  label="F_element : 0.465"  # scripted group (container) (typed FeaturePython)
  n = 0.465209
FEATURE [App::DocumentObjectGroupPython] Si_element001  label="Si_element : 0.004"  # scripted group (container) (typed FeaturePython)
  n = 0.003973
FEATURE [App::DocumentObjectGroupPython] G4_C_552  label="G4_C-552"  # scripted group (container) (typed FeaturePython)
  Dunit = g/cm3
  Dvalue = 1.76
  Group = -> [H_element020,C_element021,O_element019,F_element004,Si_element001]
  conduct = 2
  density = 1
  expand = 3
  formula = G4_C-552
  name = G4_C-552
  specific = 4
FEATURE [App::DocumentObjectGroupPython] Cd_element001  label="Cd_element : 1"  # scripted group (container) (typed FeaturePython)
  n = 1
  ref = Cd_element
FEATURE [App::DocumentObjectGroupPython] Te_element001  label="Te_element : 1"  # scripted group (container) (typed FeaturePython)
  n = 1
  ref = Te_element
FEATURE [App::DocumentObjectGroupPython] G4_CADMIUM_TELLURIDE  # scripted group (container) (typed FeaturePython)
  Dunit = g/cm3
  Dvalue = 6.2
  Group = -> [Cd_element001,Te_element001]
  conduct = 2
  density = 1
  expand = 3
  formula = G4_CADMIUM_TELLURIDE
  name = G4_CADMIUM_TELLURIDE
  specific = 4
FEATURE [App::DocumentObjectGroupPython] Cd_element002  label="Cd_element : 002"  # scripted group (container) (typed FeaturePython)
  n = 1
  ref = Cd_element
FEATURE [App::DocumentObjectGroupPython] W_element001  label="W_element : 1"  # scripted group (container) (typed FeaturePython)
  n = 1
  ref = W_element
FEATURE [App::DocumentObjectGroupPython] O_element020  label="O_element : 008"  # scripted group (container) (typed FeaturePython)
  n = 4
  ref = O_element
FEATURE [App::DocumentObjectGroupPython] G4_CADMIUM_TUNGSTATE  # scripted group (container) (typed FeaturePython)
  Dunit = g/cm3
  Dvalue = 7.9
  Group = -> [Cd_element002,W_element001,O_element020]
  conduct = 2
  density = 1
  expand = 3
  formula = G4_CADMIUM_TUNGSTATE
  name = G4_CADMIUM_TUNGSTATE
  specific = 4
FEATURE [App::DocumentObjectGroupPython] Ca_element005  label="Ca_element : 1"  # scripted group (container) (typed FeaturePython)
  n = 1
  ref = Ca_element
FEATURE [App::DocumentObjectGroupPython] C_element022  label="C_element : 009"  # scripted group (container) (typed FeaturePython)
  n = 1
  ref = C_element
FEATURE [App::DocumentObjectGroupPython] O_element021  label="O_element : 009"  # scripted group (container) (typed FeaturePython)
  n = 3
  ref = O_element
FEATURE [App::DocumentObjectGroupPython] G4_CALCIUM_CARBONATE  # scripted group (container) (typed FeaturePython)
  Dunit = g/cm3
  Dvalue = 2.8
  Group = -> [Ca_element005,C_element022,O_element021]
  conduct = 2
  density = 1
  expand = 3
  formula = G4_CALCIUM_CARBONATE
  name = G4_CALCIUM_CARBONATE
  specific = 4
FEATURE [App::DocumentObjectGroupPython] Ca_element006  label="Ca_element : 002"  # scripted group (container) (typed FeaturePython)
  n = 1
  ref = Ca_element
FEATURE [App::DocumentObjectGroupPython] F_element005  label="F_element : 003"  # scripted group (container) (typed FeaturePython)
  n = 2
  ref = F_element
FEATURE [App::DocumentObjectGroupPython] G4_CALCIUM_FLUORIDE  # scripted group (container) (typed FeaturePython)
  Dunit = g/cm3
  Dvalue = 3.18
  Group = -> [Ca_element006,F_element005]
  conduct = 2
  density = 1
  expand = 3
  formula = G4_CALCIUM_FLUORIDE
  name = G4_CALCIUM_FLUORIDE
  specific = 4
FEATURE [App::DocumentObjectGroupPython] Ca_element007  label="Ca_element : 003"  # scripted group (container) (typed FeaturePython)
  n = 1
  ref = Ca_element
FEATURE [App::DocumentObjectGroupPython] O_element022  label="O_element : 010"  # scripted group (container) (typed FeaturePython)
  n = 1
  ref = O_element
FEATURE [App::DocumentObjectGroupPython] G4_CALCIUM_OXIDE  # scripted group (container) (typed FeaturePython)
  Dunit = g/cm3
  Dvalue = 3.3
  Group = -> [Ca_element007,O_element022]
  conduct = 2
  density = 1
  expand = 3
  formula = G4_CALCIUM_OXIDE
  name = G4_CALCIUM_OXIDE
  specific = 4
FEATURE [App::DocumentObjectGroupPython] Ca_element008  label="Ca_element : 004"  # scripted group (container) (typed FeaturePython)
  n = 1
  ref = Ca_element
FEATURE [App::DocumentObjectGroupPython] S_element007  label="S_element : 002"  # scripted group (container) (typed FeaturePython)
  n = 1
  ref = S_element
FEATURE [App::DocumentObjectGroupPython] O_element023  label="O_element : 011"  # scripted group (container) (typed FeaturePython)
  n = 4
  ref = O_element
FEATURE [App::DocumentObjectGroupPython] G4_CALCIUM_SULFATE  # scripted group (container) (typed FeaturePython)
  Dunit = g/cm3
  Dvalue = 2.96
  Group = -> [Ca_element008,S_element007,O_element023]
  conduct = 2
  density = 1
  expand = 3
  formula = G4_CALCIUM_SULFATE
  name = G4_CALCIUM_SULFATE
  specific = 4
FEATURE [App::DocumentObjectGroupPython] Ca_element009  label="Ca_element : 005"  # scripted group (container) (typed FeaturePython)
  n = 1
  ref = Ca_element
FEATURE [App::DocumentObjectGroupPython] W_element002  label="W_element : 002"  # scripted group (container) (typed FeaturePython)
  n = 1
  ref = W_element
FEATURE [App::DocumentObjectGroupPython] O_element024  label="O_element : 012"  # scripted group (container) (typed FeaturePython)
  n = 4
  ref = O_element
FEATURE [App::DocumentObjectGroupPython] G4_CALCIUM_TUNGSTATE  # scripted group (container) (typed FeaturePython)
  Dunit = g/cm3
  Dvalue = 6.062
  Group = -> [Ca_element009,W_element002,O_element024]
  conduct = 2
  density = 1
  expand = 3
  formula = G4_CALCIUM_TUNGSTATE
  name = G4_CALCIUM_TUNGSTATE
  specific = 4
FEATURE [App::DocumentObjectGroupPython] C_element023  label="C_element : 010"  # scripted group (container) (typed FeaturePython)
  n = 1
  ref = C_element
FEATURE [App::DocumentObjectGroupPython] O_element025  label="O_element : 013"  # scripted group (container) (typed FeaturePython)
  n = 2
  ref = O_element
FEATURE [App::DocumentObjectGroupPython] G4_CARBON_DIOXIDE  # scripted group (container) (typed FeaturePython)
  Dunit = g/cm3
  Dvalue = 0.00184212
  Group = -> [C_element023,O_element025]
  conduct = 2
  density = 1
  expand = 3
  formula = G4_CARBON_DIOXIDE
  name = G4_CARBON_DIOXIDE
  specific = 4
FEATURE [App::DocumentObjectGroupPython] C_element024  label="C_element : 011"  # scripted group (container) (typed FeaturePython)
  n = 1
  ref = C_element
FEATURE [App::DocumentObjectGroupPython] Cl_element004  label="Cl_element : 4"  # scripted group (container) (typed FeaturePython)
  n = 4
  ref = Cl_element
FEATURE [App::DocumentObjectGroupPython] G4_CARBON_TETRACHLORIDE  # scripted group (container) (typed FeaturePython)
  Dunit = g/cm3
  Dvalue = 1.594
  Group = -> [C_element024,Cl_element004]
  conduct = 2
  density = 1
  expand = 3
  formula = G4_CARBON_TETRACHLORIDE
  name = G4_CARBON_TETRACHLORIDE
  specific = 4
FEATURE [App::DocumentObjectGroupPython] C_element025  label="C_element : 012"  # scripted group (container) (typed FeaturePython)
  n = 6
  ref = C_element
FEATURE [App::DocumentObjectGroupPython] H_element021  label="H_element : 012"  # scripted group (container) (typed FeaturePython)
  n = 10
  ref = H_element
FEATURE [App::DocumentObjectGroupPython] O_element026  label="O_element : 5"  # scripted group (container) (typed FeaturePython)
  n = 5
  ref = O_element
FEATURE [App::DocumentObjectGroupPython] G4_CELLULOSE_CELLOPHANE  # scripted group (container) (typed FeaturePython)
  Dunit = g/cm3
  Dvalue = 1.42
  Group = -> [C_element025,H_element021,O_element026]
  conduct = 2
  density = 1
  expand = 3
  formula = G4_CELLULOSE_CELLOPHANE
  name = G4_CELLULOSE_CELLOPHANE
  specific = 4
FEATURE [App::DocumentObjectGroupPython] H_element022  label="H_element : 0.067"  # scripted group (container) (typed FeaturePython)
  n = 0.067125
FEATURE [App::DocumentObjectGroupPython] C_element026  label="C_element : 0.545"  # scripted group (container) (typed FeaturePython)
  n = 0.545403
FEATURE [App::DocumentObjectGroupPython] O_element027  label="O_element : 0.387"  # scripted group (container) (typed FeaturePython)
  n = 0.387472
FEATURE [App::DocumentObjectGroupPython] G4_CELLULOSE_BUTYRATE  # scripted group (container) (typed FeaturePython)
  Dunit = g/cm3
  Dvalue = 1.2
  Group = -> [H_element022,C_element026,O_element027]
  conduct = 2
  density = 1
  expand = 3
  formula = G4_CELLULOSE_BUTYRATE
  name = G4_CELLULOSE_BUTYRATE
  specific = 4
FEATURE [App::DocumentObjectGroupPython] H_element023  label="H_element : 0.029"  # scripted group (container) (typed FeaturePython)
  n = 0.029216
FEATURE [App::DocumentObjectGroupPython] C_element027  label="C_element : 0.271"  # scripted group (container) (typed FeaturePython)
  n = 0.271296
FEATURE [App::DocumentObjectGroupPython] N_element013  label="N_element : 0.121"  # scripted group (container) (typed FeaturePython)
  n = 0.121276
FEATURE [App::DocumentObjectGroupPython] O_element028  label="O_element : 0.578"  # scripted group (container) (typed FeaturePython)
  n = 0.578212
FEATURE [App::DocumentObjectGroupPython] G4_CELLULOSE_NITRATE  # scripted group (container) (typed FeaturePython)
  Dunit = g/cm3
  Dvalue = 1.49
  Group = -> [H_element023,C_element027,N_element013,O_element028]
  conduct = 2
  density = 1
  expand = 3
  formula = G4_CELLULOSE_NITRATE
  name = G4_CELLULOSE_NITRATE
  specific = 4
FEATURE [App::DocumentObjectGroupPython] H_element024  label="H_element : 0.108"  # scripted group (container) (typed FeaturePython)
  n = 0.107596
FEATURE [App::DocumentObjectGroupPython] N_element014  label="N_element : 0.001"  # scripted group (container) (typed FeaturePython)
  n = 0.0008
FEATURE [App::DocumentObjectGroupPython] O_element029  label="O_element : 0.875"  # scripted group (container) (typed FeaturePython)
  n = 0.874976
FEATURE [App::DocumentObjectGroupPython] S_element008  label="S_element : 0.015"  # scripted group (container) (typed FeaturePython)
  n = 0.014627
FEATURE [App::DocumentObjectGroupPython] Ce_element001  label="Ce_element : 0.002"  # scripted group (container) (typed FeaturePython)
  n = 0.002001
FEATURE [App::DocumentObjectGroupPython] G4_CERIC_SULFATE  # scripted group (container) (typed FeaturePython)
  Dunit = g/cm3
  Dvalue = 1.03
  Group = -> [H_element024,N_element014,O_element029,S_element008,Ce_element001]
  conduct = 2
  density = 1
  expand = 3
  formula = G4_CERIC_SULFATE
  name = G4_CERIC_SULFATE
  specific = 4
FEATURE [App::DocumentObjectGroupPython] Cs_element001  label="Cs_element : 1"  # scripted group (container) (typed FeaturePython)
  n = 1
  ref = Cs_element
FEATURE [App::DocumentObjectGroupPython] F_element006  label="F_element : 1"  # scripted group (container) (typed FeaturePython)
  n = 1
  ref = F_element
FEATURE [App::DocumentObjectGroupPython] G4_CESIUM_FLUORIDE  # scripted group (container) (typed FeaturePython)
  Dunit = g/cm3
  Dvalue = 4.115
  Group = -> [Cs_element001,F_element006]
  conduct = 2
  density = 1
  expand = 3
  formula = G4_CESIUM_FLUORIDE
  name = G4_CESIUM_FLUORIDE
  specific = 4
FEATURE [App::DocumentObjectGroupPython] Cs_element002  label="Cs_element : 002"  # scripted group (container) (typed FeaturePython)
  n = 1
  ref = Cs_element
FEATURE [App::DocumentObjectGroupPython] I_element001  label="I_element : 1"  # scripted group (container) (typed FeaturePython)
  n = 1
  ref = I_element
FEATURE [App::DocumentObjectGroupPython] G4_CESIUM_IODIDE  # scripted group (container) (typed FeaturePython)
  Dunit = g/cm3
  Dvalue = 4.51
  Group = -> [Cs_element002,I_element001]
  conduct = 2
  density = 1
  expand = 3
  formula = G4_CESIUM_IODIDE
  name = G4_CESIUM_IODIDE
  specific = 4
FEATURE [App::DocumentObjectGroupPython] C_element028  label="C_element : 013"  # scripted group (container) (typed FeaturePython)
  n = 6
  ref = C_element
FEATURE [App::DocumentObjectGroupPython] H_element025  label="H_element : 013"  # scripted group (container) (typed FeaturePython)
  n = 5
  ref = H_element
FEATURE [App::DocumentObjectGroupPython] Cl_element005  label="Cl_element : 1"  # scripted group (container) (typed FeaturePython)
  n = 1
  ref = Cl_element
FEATURE [App::DocumentObjectGroupPython] G4_CHLOROBENZENE  # scripted group (container) (typed FeaturePython)
  Dunit = g/cm3
  Dvalue = 1.1058
  Group = -> [C_element028,H_element025,Cl_element005]
  conduct = 2
  density = 1
  expand = 3
  formula = G4_CHLOROBENZENE
  name = G4_CHLOROBENZENE
  specific = 4
FEATURE [App::DocumentObjectGroupPython] C_element029  label="C_element : 014"  # scripted group (container) (typed FeaturePython)
  n = 1
  ref = C_element
FEATURE [App::DocumentObjectGroupPython] H_element026  label="H_element : 1"  # scripted group (container) (typed FeaturePython)
  n = 1
  ref = H_element
FEATURE [App::DocumentObjectGroupPython] Cl_element006  label="Cl_element : 3"  # scripted group (container) (typed FeaturePython)
  n = 3
  ref = Cl_element
FEATURE [App::DocumentObjectGroupPython] G4_CHLOROFORM  # scripted group (container) (typed FeaturePython)
  Dunit = g/cm3
  Dvalue = 1.4832
  Group = -> [C_element029,H_element026,Cl_element006]
  conduct = 2
  density = 1
  expand = 3
  formula = G4_CHLOROFORM
  name = G4_CHLOROFORM
  specific = 4
FEATURE [App::DocumentObjectGroupPython] H_element027  label="H_element : 0.010"  # scripted group (container) (typed FeaturePython)
  n = 0.01
FEATURE [App::DocumentObjectGroupPython] C_element030  label="C_element : 0.001"  # scripted group (container) (typed FeaturePython)
  n = 0.001
FEATURE [App::DocumentObjectGroupPython] O_element030  label="O_element : 0.529"  # scripted group (container) (typed FeaturePython)
  n = 0.529107
FEATURE [App::DocumentObjectGroupPython] Na_element005  label="Na_element : 0.016"  # scripted group (container) (typed FeaturePython)
  n = 0.016
FEATURE [App::DocumentObjectGroupPython] Mg_element003  label="Mg_element : 0.004"  # scripted group (container) (typed FeaturePython)
  n = 0.002
FEATURE [App::DocumentObjectGroupPython] Al_element002  label="Al_element : 0.034"  # scripted group (container) (typed FeaturePython)
  n = 0.033872
FEATURE [App::DocumentObjectGroupPython] Si_element002  label="Si_element : 0.337"  # scripted group (container) (typed FeaturePython)
  n = 0.337021
FEATURE [App::DocumentObjectGroupPython] K_element003  label="K_element : 0.013"  # scripted group (container) (typed FeaturePython)
  n = 0.013
FEATURE [App::DocumentObjectGroupPython] Ca_element010  label="Ca_element : 0.044"  # scripted group (container) (typed FeaturePython)
  n = 0.044
FEATURE [App::DocumentObjectGroupPython] Fe_element002  label="Fe_element : 0.014"  # scripted group (container) (typed FeaturePython)
  n = 0.014
FEATURE [App::DocumentObjectGroupPython] G4_CONCRETE  # scripted group (container) (typed FeaturePython)
  Dunit = g/cm3
  Dvalue = 2.3
  Group = -> [H_element027,C_element030,O_element030,Na_element005,Mg_element003,Al_element002,Si_element002,K_element003,Ca_element010,Fe_element002]
  conduct = 2
  density = 1
  expand = 3
  formula = G4_CONCRETE
  name = G4_CONCRETE
  specific = 4
FEATURE [App::DocumentObjectGroupPython] C_element031  label="C_element : 015"  # scripted group (container) (typed FeaturePython)
  n = 6
  ref = C_element
FEATURE [App::DocumentObjectGroupPython] H_element028  label="H_element : 12"  # scripted group (container) (typed FeaturePython)
  n = 12
  ref = H_element
FEATURE [App::DocumentObjectGroupPython] G4_CYCLOHEXANE  # scripted group (container) (typed FeaturePython)
  Dunit = g/cm3
  Dvalue = 0.779
  Group = -> [C_element031,H_element028]
  conduct = 2
  density = 1
  expand = 3
  formula = G4_CYCLOHEXANE
  name = G4_CYCLOHEXANE
  specific = 4
FEATURE [App::DocumentObjectGroupPython] C_element032  label="C_element : 016"  # scripted group (container) (typed FeaturePython)
  n = 6
  ref = C_element
FEATURE [App::DocumentObjectGroupPython] H_element029  label="H_element : 4"  # scripted group (container) (typed FeaturePython)
  n = 4
  ref = H_element
FEATURE [App::DocumentObjectGroupPython] Cl_element007  label="Cl_element : 2"  # scripted group (container) (typed FeaturePython)
  n = 2
  ref = Cl_element
FEATURE [App::DocumentObjectGroupPython] G4_1_2_DICHLOROBENZENE  label="G4_1.2-DICHLOROBENZENE"  # scripted group (container) (typed FeaturePython)
  Dunit = g/cm3
  Dvalue = 1.3048
  Group = -> [C_element032,H_element029,Cl_element007]
  conduct = 2
  density = 1
  expand = 3
  formula = G4_1.2-DICHLOROBENZENE
  name = G4_1.2-DICHLOROBENZENE
  specific = 4
FEATURE [App::DocumentObjectGroupPython] C_element033  label="C_element : 017"  # scripted group (container) (typed FeaturePython)
  n = 4
  ref = C_element
FEATURE [App::DocumentObjectGroupPython] H_element030  label="H_element : 8"  # scripted group (container) (typed FeaturePython)
  n = 8
  ref = H_element
FEATURE [App::DocumentObjectGroupPython] O_element031  label="O_element : 014"  # scripted group (container) (typed FeaturePython)
  n = 1
  ref = O_element
FEATURE [App::DocumentObjectGroupPython] Cl_element008  label="Cl_element : 005"  # scripted group (container) (typed FeaturePython)
  n = 2
  ref = Cl_element
FEATURE [App::DocumentObjectGroupPython] G4_DICHLORODIETHYL_ETHER  # scripted group (container) (typed FeaturePython)
  Dunit = g/cm3
  Dvalue = 1.2199
  Group = -> [C_element033,H_element030,O_element031,Cl_element008]
  conduct = 2
  density = 1
  expand = 3
  formula = G4_DICHLORODIETHYL_ETHER
  name = G4_DICHLORODIETHYL_ETHER
  specific = 4
FEATURE [App::DocumentObjectGroupPython] C_element034  label="C_element : 018"  # scripted group (container) (typed FeaturePython)
  n = 2
  ref = C_element
FEATURE [App::DocumentObjectGroupPython] H_element031  label="H_element : 014"  # scripted group (container) (typed FeaturePython)
  n = 4
  ref = H_element
FEATURE [App::DocumentObjectGroupPython] Cl_element009  label="Cl_element : 006"  # scripted group (container) (typed FeaturePython)
  n = 2
  ref = Cl_element
FEATURE [App::DocumentObjectGroupPython] G4_1_2_DICHLOROETHANE  label="G4_1.2-DICHLOROETHANE"  # scripted group (container) (typed FeaturePython)
  Dunit = g/cm3
  Dvalue = 1.2351
  Group = -> [C_element034,H_element031,Cl_element009]
  conduct = 2
  density = 1
  expand = 3
  formula = G4_1.2-DICHLOROETHANE
  name = G4_1.2-DICHLOROETHANE
  specific = 4
FEATURE [App::DocumentObjectGroupPython] C_element035  label="C_element : 019"  # scripted group (container) (typed FeaturePython)
  n = 4
  ref = C_element
FEATURE [App::DocumentObjectGroupPython] H_element032  label="H_element : 015"  # scripted group (container) (typed FeaturePython)
  n = 10
  ref = H_element
FEATURE [App::DocumentObjectGroupPython] O_element032  label="O_element : 015"  # scripted group (container) (typed FeaturePython)
  n = 1
  ref = O_element
FEATURE [App::DocumentObjectGroupPython] G4_DIETHYL_ETHER  # scripted group (container) (typed FeaturePython)
  Dunit = g/cm3
  Dvalue = 0.71378
  Group = -> [C_element035,H_element032,O_element032]
  conduct = 2
  density = 1
  expand = 3
  formula = G4_DIETHYL_ETHER
  name = G4_DIETHYL_ETHER
  specific = 4
FEATURE [App::DocumentObjectGroupPython] C_element036  label="C_element : 020"  # scripted group (container) (typed FeaturePython)
  n = 3
  ref = C_element
FEATURE [App::DocumentObjectGroupPython] H_element033  label="H_element : 016"  # scripted group (container) (typed FeaturePython)
  n = 7
  ref = H_element
FEATURE [App::DocumentObjectGroupPython] N_element015  label="N_element : 008"  # scripted group (container) (typed FeaturePython)
  n = 1
  ref = N_element
FEATURE [App::DocumentObjectGroupPython] O_element033  label="O_element : 016"  # scripted group (container) (typed FeaturePython)
  n = 1
  ref = O_element
FEATURE [App::DocumentObjectGroupPython] G4_N_N_DIMETHYL_FORMAMIDE  label="G4_N.N-DIMETHYL_FORMAMIDE"  # scripted group (container) (typed FeaturePython)
  Dunit = g/cm3
  Dvalue = 0.9487
  Group = -> [C_element036,H_element033,N_element015,O_element033]
  conduct = 2
  density = 1
  expand = 3
  formula = G4_N.N-DIMETHYL_FORMAMIDE
  name = G4_N.N-DIMETHYL_FORMAMIDE
  specific = 4
FEATURE [App::DocumentObjectGroupPython] C_element037  label="C_element : 021"  # scripted group (container) (typed FeaturePython)
  n = 2
  ref = C_element
FEATURE [App::DocumentObjectGroupPython] H_element034  label="H_element : 017"  # scripted group (container) (typed FeaturePython)
  n = 6
  ref = H_element
FEATURE [App::DocumentObjectGroupPython] O_element034  label="O_element : 017"  # scripted group (container) (typed FeaturePython)
  n = 1
  ref = O_element
FEATURE [App::DocumentObjectGroupPython] S_element009  label="S_element : 003"  # scripted group (container) (typed FeaturePython)
  n = 1
  ref = S_element
FEATURE [App::DocumentObjectGroupPython] G4_DIMETHYL_SULFOXIDE  # scripted group (container) (typed FeaturePython)
  Dunit = g/cm3
  Dvalue = 1.1014
  Group = -> [C_element037,H_element034,O_element034,S_element009]
  conduct = 2
  density = 1
  expand = 3
  formula = G4_DIMETHYL_SULFOXIDE
  name = G4_DIMETHYL_SULFOXIDE
  specific = 4
FEATURE [App::DocumentObjectGroupPython] C_element038  label="C_element : 022"  # scripted group (container) (typed FeaturePython)
  n = 2
  ref = C_element
FEATURE [App::DocumentObjectGroupPython] H_element035  label="H_element : 018"  # scripted group (container) (typed FeaturePython)
  n = 6
  ref = H_element
FEATURE [App::DocumentObjectGroupPython] G4_ETHANE  # scripted group (container) (typed FeaturePython)
  Dunit = g/cm3
  Dvalue = 0.00125324
  Group = -> [C_element038,H_element035]
  conduct = 2
  density = 1
  expand = 3
  formula = G4_ETHANE
  name = G4_ETHANE
  specific = 4
FEATURE [App::DocumentObjectGroupPython] C_element039  label="C_element : 023"  # scripted group (container) (typed FeaturePython)
  n = 2
  ref = C_element
FEATURE [App::DocumentObjectGroupPython] H_element036  label="H_element : 019"  # scripted group (container) (typed FeaturePython)
  n = 6
  ref = H_element
FEATURE [App::DocumentObjectGroupPython] O_element035  label="O_element : 018"  # scripted group (container) (typed FeaturePython)
  n = 1
  ref = O_element
FEATURE [App::DocumentObjectGroupPython] G4_ETHYL_ALCOHOL  # scripted group (container) (typed FeaturePython)
  Dunit = g/cm3
  Dvalue = 0.7893
  Group = -> [C_element039,H_element036,O_element035]
  conduct = 2
  density = 1
  expand = 3
  formula = G4_ETHYL_ALCOHOL
  name = G4_ETHYL_ALCOHOL
  specific = 4
FEATURE [App::DocumentObjectGroupPython] H_element037  label="H_element : 0.090"  # scripted group (container) (typed FeaturePython)
  n = 0.090027
FEATURE [App::DocumentObjectGroupPython] C_element040  label="C_element : 0.585"  # scripted group (container) (typed FeaturePython)
  n = 0.585182
FEATURE [App::DocumentObjectGroupPython] O_element036  label="O_element : 0.325"  # scripted group (container) (typed FeaturePython)
  n = 0.324791
FEATURE [App::DocumentObjectGroupPython] G4_ETHYL_CELLULOSE  # scripted group (container) (typed FeaturePython)
  Dunit = g/cm3
  Dvalue = 1.13
  Group = -> [H_element037,C_element040,O_element036]
  conduct = 2
  density = 1
  expand = 3
  formula = G4_ETHYL_CELLULOSE
  name = G4_ETHYL_CELLULOSE
  specific = 4
FEATURE [App::DocumentObjectGroupPython] C_element041  label="C_element : 024"  # scripted group (container) (typed FeaturePython)
  n = 2
  ref = C_element
FEATURE [App::DocumentObjectGroupPython] H_element038  label="H_element : 020"  # scripted group (container) (typed FeaturePython)
  n = 4
  ref = H_element
FEATURE [App::DocumentObjectGroupPython] G4_ETHYLENE  # scripted group (container) (typed FeaturePython)
  Dunit = g/cm3
  Dvalue = 0.00117497
  Group = -> [C_element041,H_element038]
  conduct = 2
  density = 1
  expand = 3
  formula = G4_ETHYLENE
  name = G4_ETHYLENE
  specific = 4
FEATURE [App::DocumentObjectGroupPython] H_element039  label="H_element : 0.096"  # scripted group (container) (typed FeaturePython)
  n = 0.096
FEATURE [App::DocumentObjectGroupPython] C_element042  label="C_element : 0.195"  # scripted group (container) (typed FeaturePython)
  n = 0.195
FEATURE [App::DocumentObjectGroupPython] N_element016  label="N_element : 0.057"  # scripted group (container) (typed FeaturePython)
  n = 0.057
FEATURE [App::DocumentObjectGroupPython] O_element037  label="O_element : 0.646"  # scripted group (container) (typed FeaturePython)
  n = 0.646
FEATURE [App::DocumentObjectGroupPython] Na_element006  label="Na_element : 0.017"  # scripted group (container) (typed FeaturePython)
  n = 0.001
FEATURE [App::DocumentObjectGroupPython] P_element005  label="P_element : 0.104"  # scripted group (container) (typed FeaturePython)
  n = 0.001
FEATURE [App::DocumentObjectGroupPython] S_element010  label="S_element : 0.016"  # scripted group (container) (typed FeaturePython)
  n = 0.003
FEATURE [App::DocumentObjectGroupPython] Cl_element010  label="Cl_element : 0.005"  # scripted group (container) (typed FeaturePython)
  n = 0.001
FEATURE [App::DocumentObjectGroupPython] G4_EYE_LENS_ICRP  # scripted group (container) (typed FeaturePython)
  Dunit = g/cm3
  Dvalue = 1.07
  Group = -> [H_element039,C_element042,N_element016,O_element037,Na_element006,P_element005,S_element010,Cl_element010]
  conduct = 2
  density = 1
  expand = 3
  formula = G4_EYE_LENS_ICRP
  name = G4_EYE_LENS_ICRP
  specific = 4
FEATURE [App::DocumentObjectGroupPython] Fe_element003  label="Fe_element : 2"  # scripted group (container) (typed FeaturePython)
  n = 2
  ref = Fe_element
FEATURE [App::DocumentObjectGroupPython] O_element038  label="O_element : 019"  # scripted group (container) (typed FeaturePython)
  n = 3
  ref = O_element
FEATURE [App::DocumentObjectGroupPython] G4_FERRIC_OXIDE  # scripted group (container) (typed FeaturePython)
  Dunit = g/cm3
  Dvalue = 5.2
  Group = -> [Fe_element003,O_element038]
  conduct = 2
  density = 1
  expand = 3
  formula = G4_FERRIC_OXIDE
  name = G4_FERRIC_OXIDE
  specific = 4
FEATURE [App::DocumentObjectGroupPython] Fe_element004  label="Fe_element : 1"  # scripted group (container) (typed FeaturePython)
  n = 1
  ref = Fe_element
FEATURE [App::DocumentObjectGroupPython] B_element003  label="B_element : 1"  # scripted group (container) (typed FeaturePython)
  n = 1
  ref = B_element
FEATURE [App::DocumentObjectGroupPython] G4_FERROBORIDE  # scripted group (container) (typed FeaturePython)
  Dunit = g/cm3
  Dvalue = 7.15
  Group = -> [Fe_element004,B_element003]
  conduct = 2
  density = 1
  expand = 3
  formula = G4_FERROBORIDE
  name = G4_FERROBORIDE
  specific = 4
FEATURE [App::DocumentObjectGroupPython] Fe_element005  label="Fe_element : 003"  # scripted group (container) (typed FeaturePython)
  n = 1
  ref = Fe_element
FEATURE [App::DocumentObjectGroupPython] O_element039  label="O_element : 020"  # scripted group (container) (typed FeaturePython)
  n = 1
  ref = O_element
FEATURE [App::DocumentObjectGroupPython] G4_FERROUS_OXIDE  # scripted group (container) (typed FeaturePython)
  Dunit = g/cm3
  Dvalue = 5.7
  Group = -> [Fe_element005,O_element039]
  conduct = 2
  density = 1
  expand = 3
  formula = G4_FERROUS_OXIDE
  name = G4_FERROUS_OXIDE
  specific = 4
FEATURE [App::DocumentObjectGroupPython] H_element040  label="H_element : 0.115"  # scripted group (container) (typed FeaturePython)
  n = 0.108259
FEATURE [App::DocumentObjectGroupPython] N_element017  label="N_element : 0.000"  # scripted group (container) (typed FeaturePython)
  n = 2.7e-05
FEATURE [App::DocumentObjectGroupPython] O_element040  label="O_element : 0.879"  # scripted group (container) (typed FeaturePython)
  n = 0.878636
FEATURE [App::DocumentObjectGroupPython] Na_element007  label="Na_element : 0.000"  # scripted group (container) (typed FeaturePython)
  n = 2.2e-05
FEATURE [App::DocumentObjectGroupPython] S_element011  label="S_element : 0.013"  # scripted group (container) (typed FeaturePython)
  n = 0.012968
FEATURE [App::DocumentObjectGroupPython] Cl_element011  label="Cl_element : 0.000"  # scripted group (container) (typed FeaturePython)
  n = 3.4e-05
FEATURE [App::DocumentObjectGroupPython] Fe_element006  label="Fe_element : 0.000"  # scripted group (container) (typed FeaturePython)
  n = 5.4e-05
FEATURE [App::DocumentObjectGroupPython] G4_FERROUS_SULFATE  # scripted group (container) (typed FeaturePython)
  Dunit = g/cm3
  Dvalue = 1.024
  Group = -> [H_element040,N_element017,O_element040,Na_element007,S_element011,Cl_element011,Fe_element006]
  conduct = 2
  density = 1
  expand = 3
  formula = G4_FERROUS_SULFATE
  name = G4_FERROUS_SULFATE
  specific = 4
FEATURE [App::DocumentObjectGroupPython] C_element043  label="C_element : 0.099"  # scripted group (container) (typed FeaturePython)
  n = 0.099335
FEATURE [App::DocumentObjectGroupPython] F_element007  label="F_element : 0.314"  # scripted group (container) (typed FeaturePython)
  n = 0.314247
FEATURE [App::DocumentObjectGroupPython] Cl_element012  label="Cl_element : 0.586"  # scripted group (container) (typed FeaturePython)
  n = 0.586418
FEATURE [App::DocumentObjectGroupPython] G4_FREON_12  label="G4_FREON-12"  # scripted group (container) (typed FeaturePython)
  Dunit = g/cm3
  Dvalue = 1.12
  Group = -> [C_element043,F_element007,Cl_element012]
  conduct = 2
  density = 1
  expand = 3
  formula = G4_FREON-12
  name = G4_FREON-12
  specific = 4
FEATURE [App::DocumentObjectGroupPython] C_element044  label="C_element : 0.057"  # scripted group (container) (typed FeaturePython)
  n = 0.057245
FEATURE [App::DocumentObjectGroupPython] F_element008  label="F_element : 0.181"  # scripted group (container) (typed FeaturePython)
  n = 0.181096
FEATURE [App::DocumentObjectGroupPython] Br_element001  label="Br_element : 0.762"  # scripted group (container) (typed FeaturePython)
  n = 0.761659
FEATURE [App::DocumentObjectGroupPython] G4_FREON_12B2  label="G4_FREON-12B2"  # scripted group (container) (typed FeaturePython)
  Dunit = g/cm3
  Dvalue = 1.8
  Group = -> [C_element044,F_element008,Br_element001]
  conduct = 2
  density = 1
  expand = 3
  formula = G4_FREON-12B2
  name = G4_FREON-12B2
  specific = 4
FEATURE [App::DocumentObjectGroupPython] C_element045  label="C_element : 0.115"  # scripted group (container) (typed FeaturePython)
  n = 0.114983
FEATURE [App::DocumentObjectGroupPython] F_element009  label="F_element : 0.546"  # scripted group (container) (typed FeaturePython)
  n = 0.545621
FEATURE [App::DocumentObjectGroupPython] Cl_element013  label="Cl_element : 0.339"  # scripted group (container) (typed FeaturePython)
  n = 0.339396
FEATURE [App::DocumentObjectGroupPython] G4_FREON_13  label="G4_FREON-13"  # scripted group (container) (typed FeaturePython)
  Dunit = g/cm3
  Dvalue = 0.95
  Group = -> [C_element045,F_element009,Cl_element013]
  conduct = 2
  density = 1
  expand = 3
  formula = G4_FREON-13
  name = G4_FREON-13
  specific = 4
FEATURE [App::DocumentObjectGroupPython] C_element046  label="C_element : 025"  # scripted group (container) (typed FeaturePython)
  n = 1
  ref = C_element
FEATURE [App::DocumentObjectGroupPython] F_element010  label="F_element : 3"  # scripted group (container) (typed FeaturePython)
  n = 3
  ref = F_element
FEATURE [App::DocumentObjectGroupPython] Br_element002  label="Br_element : 1"  # scripted group (container) (typed FeaturePython)
  n = 1
  ref = Br_element
FEATURE [App::DocumentObjectGroupPython] G4_FREON_13B1  label="G4_FREON-13B1"  # scripted group (container) (typed FeaturePython)
  Dunit = g/cm3
  Dvalue = 1.5
  Group = -> [C_element046,F_element010,Br_element002]
  conduct = 2
  density = 1
  expand = 3
  formula = G4_FREON-13B1
  name = G4_FREON-13B1
  specific = 4
FEATURE [App::DocumentObjectGroupPython] C_element047  label="C_element : 0.061"  # scripted group (container) (typed FeaturePython)
  n = 0.061309
FEATURE [App::DocumentObjectGroupPython] F_element011  label="F_element : 0.291"  # scripted group (container) (typed FeaturePython)
  n = 0.290924
FEATURE [App::DocumentObjectGroupPython] I_element002  label="I_element : 0.648"  # scripted group (container) (typed FeaturePython)
  n = 0.647767
FEATURE [App::DocumentObjectGroupPython] G4_FREON_13I1  label="G4_FREON-13I1"  # scripted group (container) (typed FeaturePython)
  Dunit = g/cm3
  Dvalue = 1.8
  Group = -> [C_element047,F_element011,I_element002]
  conduct = 2
  density = 1
  expand = 3
  formula = G4_FREON-13I1
  name = G4_FREON-13I1
  specific = 4
FEATURE [App::DocumentObjectGroupPython] Gd_element001  label="Gd_element : 2"  # scripted group (container) (typed FeaturePython)
  n = 2
  ref = Gd_element
FEATURE [App::DocumentObjectGroupPython] O_element041  label="O_element : 021"  # scripted group (container) (typed FeaturePython)
  n = 2
  ref = O_element
FEATURE [App::DocumentObjectGroupPython] S_element012  label="S_element : 004"  # scripted group (container) (typed FeaturePython)
  n = 1
  ref = S_element
FEATURE [App::DocumentObjectGroupPython] G4_GADOLINIUM_OXYSULFIDE  # scripted group (container) (typed FeaturePython)
  Dunit = g/cm3
  Dvalue = 7.44
  Group = -> [Gd_element001,O_element041,S_element012]
  conduct = 2
  density = 1
  expand = 3
  formula = G4_GADOLINIUM_OXYSULFIDE
  name = G4_GADOLINIUM_OXYSULFIDE
  specific = 4
FEATURE [App::DocumentObjectGroupPython] Ga_element001  label="Ga_element : 1"  # scripted group (container) (typed FeaturePython)
  n = 1
  ref = Ga_element
FEATURE [App::DocumentObjectGroupPython] As_element001  label="As_element : 1"  # scripted group (container) (typed FeaturePython)
  n = 1
  ref = As_element
FEATURE [App::DocumentObjectGroupPython] G4_GALLIUM_ARSENIDE  # scripted group (container) (typed FeaturePython)
  Dunit = g/cm3
  Dvalue = 5.31
  Group = -> [Ga_element001,As_element001]
  conduct = 2
  density = 1
  expand = 3
  formula = G4_GALLIUM_ARSENIDE
  name = G4_GALLIUM_ARSENIDE
  specific = 4
FEATURE [App::DocumentObjectGroupPython] H_element041  label="H_element : 0.081"  # scripted group (container) (typed FeaturePython)
  n = 0.08118
FEATURE [App::DocumentObjectGroupPython] C_element048  label="C_element : 0.416"  # scripted group (container) (typed FeaturePython)
  n = 0.41606
FEATURE [App::DocumentObjectGroupPython] N_element018  label="N_element : 0.111"  # scripted group (container) (typed FeaturePython)
  n = 0.11124
FEATURE [App::DocumentObjectGroupPython] O_element042  label="O_element : 0.381"  # scripted group (container) (typed FeaturePython)
  n = 0.38064
FEATURE [App::DocumentObjectGroupPython] S_element013  label="S_element : 0.011"  # scripted group (container) (typed FeaturePython)
  n = 0.01088
FEATURE [App::DocumentObjectGroupPython] G4_GEL_PHOTO_EMULSION  # scripted group (container) (typed FeaturePython)
  Dunit = g/cm3
  Dvalue = 1.2914
  Group = -> [H_element041,C_element048,N_element018,O_element042,S_element013]
  conduct = 2
  density = 1
  expand = 3
  formula = G4_GEL_PHOTO_EMULSION
  name = G4_GEL_PHOTO_EMULSION
  specific = 4
FEATURE [App::DocumentObjectGroupPython] B_element004  label="B_element : 0.040"  # scripted group (container) (typed FeaturePython)
  n = 0.0400639
FEATURE [App::DocumentObjectGroupPython] O_element043  label="O_element : 0.540"  # scripted group (container) (typed FeaturePython)
  n = 0.539561
FEATURE [App::DocumentObjectGroupPython] Na_element008  label="Na_element : 0.028"  # scripted group (container) (typed FeaturePython)
  n = 0.0281909
FEATURE [App::DocumentObjectGroupPython] Al_element003  label="Al_element : 0.012"  # scripted group (container) (typed FeaturePython)
  n = 0.011644
FEATURE [App::DocumentObjectGroupPython] Si_element003  label="Si_element : 0.377"  # scripted group (container) (typed FeaturePython)
  n = 0.377219
FEATURE [App::DocumentObjectGroupPython] K_element004  label="K_element : 0.014"  # scripted group (container) (typed FeaturePython)
  n = 0.00332099
FEATURE [App::DocumentObjectGroupPython] G4_Pyrex_Glass  # scripted group (container) (typed FeaturePython)
  Dunit = g/cm3
  Dvalue = 2.23
  Group = -> [B_element004,O_element043,Na_element008,Al_element003,Si_element003,K_element004]
  conduct = 2
  density = 1
  expand = 3
  formula = G4_Pyrex_Glass
  name = G4_Pyrex_Glass
  specific = 4
FEATURE [App::DocumentObjectGroupPython] O_element044  label="O_element : 0.156"  # scripted group (container) (typed FeaturePython)
  n = 0.156453
FEATURE [App::DocumentObjectGroupPython] Si_element004  label="Si_element : 0.081"  # scripted group (container) (typed FeaturePython)
  n = 0.080866
FEATURE [App::DocumentObjectGroupPython] Ti_element001  label="Ti_element : 0.008"  # scripted group (container) (typed FeaturePython)
  n = 0.008092
FEATURE [App::DocumentObjectGroupPython] As_element002  label="As_element : 0.003"  # scripted group (container) (typed FeaturePython)
  n = 0.002651
FEATURE [App::DocumentObjectGroupPython] Pb_element001  label="Pb_element : 0.752"  # scripted group (container) (typed FeaturePython)
  n = 0.751938
FEATURE [App::DocumentObjectGroupPython] G4_GLASS_LEAD  # scripted group (container) (typed FeaturePython)
  Dunit = g/cm3
  Dvalue = 6.22
  Group = -> [O_element044,Si_element004,Ti_element001,As_element002,Pb_element001]
  conduct = 2
  density = 1
  expand = 3
  formula = G4_GLASS_LEAD
  name = G4_GLASS_LEAD
  specific = 4
FEATURE [App::DocumentObjectGroupPython] O_element045  label="O_element : 0.460"  # scripted group (container) (typed FeaturePython)
  n = 0.4598
FEATURE [App::DocumentObjectGroupPython] Na_element009  label="Na_element : 0.096"  # scripted group (container) (typed FeaturePython)
  n = 0.0964411
FEATURE [App::DocumentObjectGroupPython] Si_element005  label="Si_element : 0.378"  # scripted group (container) (typed FeaturePython)
  n = 0.336553
FEATURE [App::DocumentObjectGroupPython] Ca_element011  label="Ca_element : 0.107"  # scripted group (container) (typed FeaturePython)
  n = 0.107205
FEATURE [App::DocumentObjectGroupPython] G4_GLASS_PLATE  # scripted group (container) (typed FeaturePython)
  Dunit = g/cm3
  Dvalue = 2.4
  Group = -> [O_element045,Na_element009,Si_element005,Ca_element011]
  conduct = 2
  density = 1
  expand = 3
  formula = G4_GLASS_PLATE
  name = G4_GLASS_PLATE
  specific = 4
FEATURE [App::DocumentObjectGroupPython] C_element049  label="C_element : 026"  # scripted group (container) (typed FeaturePython)
  n = 5
  ref = C_element
FEATURE [App::DocumentObjectGroupPython] H_element042  label="H_element : 021"  # scripted group (container) (typed FeaturePython)
  n = 10
  ref = H_element
FEATURE [App::DocumentObjectGroupPython] N_element019  label="N_element : 2"  # scripted group (container) (typed FeaturePython)
  n = 2
  ref = N_element
FEATURE [App::DocumentObjectGroupPython] O_element046  label="O_element : 022"  # scripted group (container) (typed FeaturePython)
  n = 3
  ref = O_element
FEATURE [App::DocumentObjectGroupPython] G4_GLUTAMINE  # scripted group (container) (typed FeaturePython)
  Dunit = g/cm3
  Dvalue = 1.46
  Group = -> [C_element049,H_element042,N_element019,O_element046]
  conduct = 2
  density = 1
  expand = 3
  formula = G4_GLUTAMINE
  name = G4_GLUTAMINE
  specific = 4
FEATURE [App::DocumentObjectGroupPython] C_element050  label="C_element : 027"  # scripted group (container) (typed FeaturePython)
  n = 3
  ref = C_element
FEATURE [App::DocumentObjectGroupPython] H_element043  label="H_element : 022"  # scripted group (container) (typed FeaturePython)
  n = 8
  ref = H_element
FEATURE [App::DocumentObjectGroupPython] O_element047  label="O_element : 023"  # scripted group (container) (typed FeaturePython)
  n = 3
  ref = O_element
FEATURE [App::DocumentObjectGroupPython] G4_GLYCEROL  # scripted group (container) (typed FeaturePython)
  Dunit = g/cm3
  Dvalue = 1.2613
  Group = -> [C_element050,H_element043,O_element047]
  conduct = 2
  density = 1
  expand = 3
  formula = G4_GLYCEROL
  name = G4_GLYCEROL
  specific = 4
FEATURE [App::DocumentObjectGroupPython] C_element051  label="C_element : 028"  # scripted group (container) (typed FeaturePython)
  n = 5
  ref = C_element
FEATURE [App::DocumentObjectGroupPython] H_element044  label="H_element : 023"  # scripted group (container) (typed FeaturePython)
  n = 5
  ref = H_element
FEATURE [App::DocumentObjectGroupPython] N_element020  label="N_element : 009"  # scripted group (container) (typed FeaturePython)
  n = 5
  ref = N_element
FEATURE [App::DocumentObjectGroupPython] O_element048  label="O_element : 024"  # scripted group (container) (typed FeaturePython)
  n = 1
  ref = O_element
FEATURE [App::DocumentObjectGroupPython] G4_GUANINE  # scripted group (container) (typed FeaturePython)
  Dunit = g/cm3
  Dvalue = 2.2
  Group = -> [C_element051,H_element044,N_element020,O_element048]
  conduct = 2
  density = 1
  expand = 3
  formula = G4_GUANINE
  name = G4_GUANINE
  specific = 4
FEATURE [App::DocumentObjectGroupPython] Ca_element012  label="Ca_element : 006"  # scripted group (container) (typed FeaturePython)
  n = 1
  ref = Ca_element
FEATURE [App::DocumentObjectGroupPython] S_element014  label="S_element : 005"  # scripted group (container) (typed FeaturePython)
  n = 1
  ref = S_element
FEATURE [App::DocumentObjectGroupPython] O_element049  label="O_element : 6"  # scripted group (container) (typed FeaturePython)
  n = 6
  ref = O_element
FEATURE [App::DocumentObjectGroupPython] H_element045  label="H_element : 024"  # scripted group (container) (typed FeaturePython)
  n = 4
  ref = H_element
FEATURE [App::DocumentObjectGroupPython] G4_GYPSUM  # scripted group (container) (typed FeaturePython)
  Dunit = g/cm3
  Dvalue = 2.32
  Group = -> [Ca_element012,S_element014,O_element049,H_element045]
  conduct = 2
  density = 1
  expand = 3
  formula = G4_GYPSUM
  name = G4_GYPSUM
  specific = 4
FEATURE [App::DocumentObjectGroupPython] C_element052  label="C_element : 7"  # scripted group (container) (typed FeaturePython)
  n = 7
  ref = C_element
FEATURE [App::DocumentObjectGroupPython] H_element046  label="H_element : 16"  # scripted group (container) (typed FeaturePython)
  n = 16
  ref = H_element
FEATURE [App::DocumentObjectGroupPython] G4_N_HEPTANE  label="G4_N-HEPTANE"  # scripted group (container) (typed FeaturePython)
  Dunit = g/cm3
  Dvalue = 0.68376
  Group = -> [C_element052,H_element046]
  conduct = 2
  density = 1
  expand = 3
  formula = G4_N-HEPTANE
  name = G4_N-HEPTANE
  specific = 4
FEATURE [App::DocumentObjectGroupPython] C_element053  label="C_element : 029"  # scripted group (container) (typed FeaturePython)
  n = 6
  ref = C_element
FEATURE [App::DocumentObjectGroupPython] H_element047  label="H_element : 14"  # scripted group (container) (typed FeaturePython)
  n = 14
  ref = H_element
FEATURE [App::DocumentObjectGroupPython] G4_N_HEXANE  label="G4_N-HEXANE"  # scripted group (container) (typed FeaturePython)
  Dunit = g/cm3
  Dvalue = 0.6603
  Group = -> [C_element053,H_element047]
  conduct = 2
  density = 1
  expand = 3
  formula = G4_N-HEXANE
  name = G4_N-HEXANE
  specific = 4
FEATURE [App::DocumentObjectGroupPython] C_element054  label="C_element : 22"  # scripted group (container) (typed FeaturePython)
  n = 22
  ref = C_element
FEATURE [App::DocumentObjectGroupPython] H_element048  label="H_element : 025"  # scripted group (container) (typed FeaturePython)
  n = 10
  ref = H_element
FEATURE [App::DocumentObjectGroupPython] N_element021  label="N_element : 010"  # scripted group (container) (typed FeaturePython)
  n = 2
  ref = N_element
FEATURE [App::DocumentObjectGroupPython] O_element050  label="O_element : 025"  # scripted group (container) (typed FeaturePython)
  n = 5
  ref = O_element
FEATURE [App::DocumentObjectGroupPython] G4_KAPTON  # scripted group (container) (typed FeaturePython)
  Dunit = g/cm3
  Dvalue = 1.42
  Group = -> [C_element054,H_element048,N_element021,O_element050]
  conduct = 2
  density = 1
  expand = 3
  formula = G4_KAPTON
  name = G4_KAPTON
  specific = 4
FEATURE [App::DocumentObjectGroupPython] La_element001  label="La_element : 1"  # scripted group (container) (typed FeaturePython)
  n = 1
  ref = La_element
FEATURE [App::DocumentObjectGroupPython] Br_element003  label="Br_element : 002"  # scripted group (container) (typed FeaturePython)
  n = 1
  ref = Br_element
FEATURE [App::DocumentObjectGroupPython] O_element051  label="O_element : 026"  # scripted group (container) (typed FeaturePython)
  n = 1
  ref = O_element
FEATURE [App::DocumentObjectGroupPython] G4_LANTHANUM_OXYBROMIDE  # scripted group (container) (typed FeaturePython)
  Dunit = g/cm3
  Dvalue = 6.28
  Group = -> [La_element001,Br_element003,O_element051]
  conduct = 2
  density = 1
  expand = 3
  formula = G4_LANTHANUM_OXYBROMIDE
  name = G4_LANTHANUM_OXYBROMIDE
  specific = 4
FEATURE [App::DocumentObjectGroupPython] La_element002  label="La_element : 2"  # scripted group (container) (typed FeaturePython)
  n = 2
  ref = La_element
FEATURE [App::DocumentObjectGroupPython] O_element052  label="O_element : 027"  # scripted group (container) (typed FeaturePython)
  n = 2
  ref = O_element
FEATURE [App::DocumentObjectGroupPython] S_element015  label="S_element : 006"  # scripted group (container) (typed FeaturePython)
  n = 1
  ref = S_element
FEATURE [App::DocumentObjectGroupPython] G4_LANTHANUM_OXYSULFIDE  # scripted group (container) (typed FeaturePython)
  Dunit = g/cm3
  Dvalue = 5.86
  Group = -> [La_element002,O_element052,S_element015]
  conduct = 2
  density = 1
  expand = 3
  formula = G4_LANTHANUM_OXYSULFIDE
  name = G4_LANTHANUM_OXYSULFIDE
  specific = 4
FEATURE [App::DocumentObjectGroupPython] O_element053  label="O_element : 0.072"  # scripted group (container) (typed FeaturePython)
  n = 0.071682
FEATURE [App::DocumentObjectGroupPython] Pb_element002  label="Pb_element : 0.928"  # scripted group (container) (typed FeaturePython)
  n = 0.928318
FEATURE [App::DocumentObjectGroupPython] G4_LEAD_OXIDE  # scripted group (container) (typed FeaturePython)
  Dunit = g/cm3
  Dvalue = 9.53
  Group = -> [O_element053,Pb_element002]
  conduct = 2
  density = 1
  expand = 3
  formula = G4_LEAD_OXIDE
  name = G4_LEAD_OXIDE
  specific = 4
FEATURE [App::DocumentObjectGroupPython] Li_element001  label="Li_element : 1"  # scripted group (container) (typed FeaturePython)
  n = 1
  ref = Li_element
FEATURE [App::DocumentObjectGroupPython] N_element022  label="N_element : 011"  # scripted group (container) (typed FeaturePython)
  n = 1
  ref = N_element
FEATURE [App::DocumentObjectGroupPython] H_element049  label="H_element : 026"  # scripted group (container) (typed FeaturePython)
  n = 2
  ref = H_element
FEATURE [App::DocumentObjectGroupPython] G4_LITHIUM_AMIDE  # scripted group (container) (typed FeaturePython)
  Dunit = g/cm3
  Dvalue = 1.178
  Group = -> [Li_element001,N_element022,H_element049]
  conduct = 2
  density = 1
  expand = 3
  formula = G4_LITHIUM_AMIDE
  name = G4_LITHIUM_AMIDE
  specific = 4
FEATURE [App::DocumentObjectGroupPython] Li_element002  label="Li_element : 2"  # scripted group (container) (typed FeaturePython)
  n = 2
  ref = Li_element
FEATURE [App::DocumentObjectGroupPython] C_element055  label="C_element : 030"  # scripted group (container) (typed FeaturePython)
  n = 1
  ref = C_element
FEATURE [App::DocumentObjectGroupPython] O_element054  label="O_element : 028"  # scripted group (container) (typed FeaturePython)
  n = 3
  ref = O_element
FEATURE [App::DocumentObjectGroupPython] G4_LITHIUM_CARBONATE  # scripted group (container) (typed FeaturePython)
  Dunit = g/cm3
  Dvalue = 2.11
  Group = -> [Li_element002,C_element055,O_element054]
  conduct = 2
  density = 1
  expand = 3
  formula = G4_LITHIUM_CARBONATE
  name = G4_LITHIUM_CARBONATE
  specific = 4
FEATURE [App::DocumentObjectGroupPython] Li_element003  label="Li_element : 003"  # scripted group (container) (typed FeaturePython)
  n = 1
  ref = Li_element
FEATURE [App::DocumentObjectGroupPython] F_element012  label="F_element : 004"  # scripted group (container) (typed FeaturePython)
  n = 1
  ref = F_element
FEATURE [App::DocumentObjectGroupPython] G4_LITHIUM_FLUORIDE  # scripted group (container) (typed FeaturePython)
  Dunit = g/cm3
  Dvalue = 2.635
  Group = -> [Li_element003,F_element012]
  conduct = 2
  density = 1
  expand = 3
  formula = G4_LITHIUM_FLUORIDE
  name = G4_LITHIUM_FLUORIDE
  specific = 4
FEATURE [App::DocumentObjectGroupPython] Li_element004  label="Li_element : 004"  # scripted group (container) (typed FeaturePython)
  n = 1
  ref = Li_element
FEATURE [App::DocumentObjectGroupPython] H_element050  label="H_element : 027"  # scripted group (container) (typed FeaturePython)
  n = 1
  ref = H_element
FEATURE [App::DocumentObjectGroupPython] G4_LITHIUM_HYDRIDE  # scripted group (container) (typed FeaturePython)
  Dunit = g/cm3
  Dvalue = 0.82
  Group = -> [Li_element004,H_element050]
  conduct = 2
  density = 1
  expand = 3
  formula = G4_LITHIUM_HYDRIDE
  name = G4_LITHIUM_HYDRIDE
  specific = 4
FEATURE [App::DocumentObjectGroupPython] Li_element005  label="Li_element : 005"  # scripted group (container) (typed FeaturePython)
  n = 1
  ref = Li_element
FEATURE [App::DocumentObjectGroupPython] I_element003  label="I_element : 002"  # scripted group (container) (typed FeaturePython)
  n = 1
  ref = I_element
FEATURE [App::DocumentObjectGroupPython] G4_LITHIUM_IODIDE  # scripted group (container) (typed FeaturePython)
  Dunit = g/cm3
  Dvalue = 3.494
  Group = -> [Li_element005,I_element003]
  conduct = 2
  density = 1
  expand = 3
  formula = G4_LITHIUM_IODIDE
  name = G4_LITHIUM_IODIDE
  specific = 4
FEATURE [App::DocumentObjectGroupPython] Li_element006  label="Li_element : 006"  # scripted group (container) (typed FeaturePython)
  n = 2
  ref = Li_element
FEATURE [App::DocumentObjectGroupPython] O_element055  label="O_element : 029"  # scripted group (container) (typed FeaturePython)
  n = 1
  ref = O_element
FEATURE [App::DocumentObjectGroupPython] G4_LITHIUM_OXIDE  # scripted group (container) (typed FeaturePython)
  Dunit = g/cm3
  Dvalue = 2.013
  Group = -> [Li_element006,O_element055]
  conduct = 2
  density = 1
  expand = 3
  formula = G4_LITHIUM_OXIDE
  name = G4_LITHIUM_OXIDE
  specific = 4
FEATURE [App::DocumentObjectGroupPython] Li_element007  label="Li_element : 007"  # scripted group (container) (typed FeaturePython)
  n = 2
  ref = Li_element
FEATURE [App::DocumentObjectGroupPython] B_element005  label="B_element : 005"  # scripted group (container) (typed FeaturePython)
  n = 4
  ref = B_element
FEATURE [App::DocumentObjectGroupPython] O_element056  label="O_element : 7"  # scripted group (container) (typed FeaturePython)
  n = 7
  ref = O_element
FEATURE [App::DocumentObjectGroupPython] G4_LITHIUM_TETRABORATE  # scripted group (container) (typed FeaturePython)
  Dunit = g/cm3
  Dvalue = 2.44
  Group = -> [Li_element007,B_element005,O_element056]
  conduct = 2
  density = 1
  expand = 3
  formula = G4_LITHIUM_TETRABORATE
  name = G4_LITHIUM_TETRABORATE
  specific = 4
FEATURE [App::DocumentObjectGroupPython] H_element051  label="H_element : 0.105"  # scripted group (container) (typed FeaturePython)
  n = 0.105
FEATURE [App::DocumentObjectGroupPython] C_element056  label="C_element : 0.083"  # scripted group (container) (typed FeaturePython)
  n = 0.083
FEATURE [App::DocumentObjectGroupPython] N_element023  label="N_element : 0.023"  # scripted group (container) (typed FeaturePython)
  n = 0.023
FEATURE [App::DocumentObjectGroupPython] O_element057  label="O_element : 0.779"  # scripted group (container) (typed FeaturePython)
  n = 0.779
FEATURE [App::DocumentObjectGroupPython] Na_element010  label="Na_element : 0.097"  # scripted group (container) (typed FeaturePython)
  n = 0.002
FEATURE [App::DocumentObjectGroupPython] P_element006  label="P_element : 0.105"  # scripted group (container) (typed FeaturePython)
  n = 0.001
FEATURE [App::DocumentObjectGroupPython] S_element016  label="S_element : 0.017"  # scripted group (container) (typed FeaturePython)
  n = 0.002
FEATURE [App::DocumentObjectGroupPython] Cl_element014  label="Cl_element : 0.587"  # scripted group (container) (typed FeaturePython)
  n = 0.003
FEATURE [App::DocumentObjectGroupPython] K_element005  label="K_element : 0.015"  # scripted group (container) (typed FeaturePython)
  n = 0.002
FEATURE [App::DocumentObjectGroupPython] G4_LUNG_ICRP  # scripted group (container) (typed FeaturePython)
  Dunit = g/cm3
  Dvalue = 1.04
  Group = -> [H_element051,C_element056,N_element023,O_element057,Na_element010,P_element006,S_element016,Cl_element014,K_element005]
  conduct = 2
  density = 1
  expand = 3
  formula = G4_LUNG_ICRP
  name = G4_LUNG_ICRP
  specific = 4
FEATURE [App::DocumentObjectGroupPython] H_element052  label="H_element : 0.116"  # scripted group (container) (typed FeaturePython)
  n = 0.114318
FEATURE [App::DocumentObjectGroupPython] C_element057  label="C_element : 0.656"  # scripted group (container) (typed FeaturePython)
  n = 0.655824
FEATURE [App::DocumentObjectGroupPython] O_element058  label="O_element : 0.092"  # scripted group (container) (typed FeaturePython)
  n = 0.0921831
FEATURE [App::DocumentObjectGroupPython] Mg_element004  label="Mg_element : 0.135"  # scripted group (container) (typed FeaturePython)
  n = 0.134792
FEATURE [App::DocumentObjectGroupPython] Ca_element013  label="Ca_element : 0.003"  # scripted group (container) (typed FeaturePython)
  n = 0.002883
FEATURE [App::DocumentObjectGroupPython] G4_M3_WAX  # scripted group (container) (typed FeaturePython)
  Dunit = g/cm3
  Dvalue = 1.05
  Group = -> [H_element052,C_element057,O_element058,Mg_element004,Ca_element013]
  conduct = 2
  density = 1
  expand = 3
  formula = G4_M3_WAX
  name = G4_M3_WAX
  specific = 4
FEATURE [App::DocumentObjectGroupPython] Mg_element005  label="Mg_element : 1"  # scripted group (container) (typed FeaturePython)
  n = 1
  ref = Mg_element
FEATURE [App::DocumentObjectGroupPython] C_element058  label="C_element : 031"  # scripted group (container) (typed FeaturePython)
  n = 1
  ref = C_element
FEATURE [App::DocumentObjectGroupPython] O_element059  label="O_element : 030"  # scripted group (container) (typed FeaturePython)
  n = 3
  ref = O_element
FEATURE [App::DocumentObjectGroupPython] G4_MAGNESIUM_CARBONATE  # scripted group (container) (typed FeaturePython)
  Dunit = g/cm3
  Dvalue = 2.958
  Group = -> [Mg_element005,C_element058,O_element059]
  conduct = 2
  density = 1
  expand = 3
  formula = G4_MAGNESIUM_CARBONATE
  name = G4_MAGNESIUM_CARBONATE
  specific = 4
FEATURE [App::DocumentObjectGroupPython] Mg_element006  label="Mg_element : 002"  # scripted group (container) (typed FeaturePython)
  n = 1
  ref = Mg_element
FEATURE [App::DocumentObjectGroupPython] F_element013  label="F_element : 005"  # scripted group (container) (typed FeaturePython)
  n = 2
  ref = F_element
FEATURE [App::DocumentObjectGroupPython] G4_MAGNESIUM_FLUORIDE  # scripted group (container) (typed FeaturePython)
  Dunit = g/cm3
  Dvalue = 3
  Group = -> [Mg_element006,F_element013]
  conduct = 2
  density = 1
  expand = 3
  formula = G4_MAGNESIUM_FLUORIDE
  name = G4_MAGNESIUM_FLUORIDE
  specific = 4
FEATURE [App::DocumentObjectGroupPython] Mg_element007  label="Mg_element : 003"  # scripted group (container) (typed FeaturePython)
  n = 1
  ref = Mg_element
FEATURE [App::DocumentObjectGroupPython] O_element060  label="O_element : 031"  # scripted group (container) (typed FeaturePython)
  n = 1
  ref = O_element
FEATURE [App::DocumentObjectGroupPython] G4_MAGNESIUM_OXIDE  # scripted group (container) (typed FeaturePython)
  Dunit = g/cm3
  Dvalue = 3.58
  Group = -> [Mg_element007,O_element060]
  conduct = 2
  density = 1
  expand = 3
  formula = G4_MAGNESIUM_OXIDE
  name = G4_MAGNESIUM_OXIDE
  specific = 4
FEATURE [App::DocumentObjectGroupPython] Mg_element008  label="Mg_element : 004"  # scripted group (container) (typed FeaturePython)
  n = 1
  ref = Mg_element
FEATURE [App::DocumentObjectGroupPython] B_element006  label="B_element : 006"  # scripted group (container) (typed FeaturePython)
  n = 4
  ref = B_element
FEATURE [App::DocumentObjectGroupPython] O_element061  label="O_element : 032"  # scripted group (container) (typed FeaturePython)
  n = 7
  ref = O_element
FEATURE [App::DocumentObjectGroupPython] G4_MAGNESIUM_TETRABORATE  # scripted group (container) (typed FeaturePython)
  Dunit = g/cm3
  Dvalue = 2.53
  Group = -> [Mg_element008,B_element006,O_element061]
  conduct = 2
  density = 1
  expand = 3
  formula = G4_MAGNESIUM_TETRABORATE
  name = G4_MAGNESIUM_TETRABORATE
  specific = 4
FEATURE [App::DocumentObjectGroupPython] Hg_element001  label="Hg_element : 1"  # scripted group (container) (typed FeaturePython)
  n = 1
  ref = Hg_element
FEATURE [App::DocumentObjectGroupPython] I_element004  label="I_element : 2"  # scripted group (container) (typed FeaturePython)
  n = 2
  ref = I_element
FEATURE [App::DocumentObjectGroupPython] G4_MERCURIC_IODIDE  # scripted group (container) (typed FeaturePython)
  Dunit = g/cm3
  Dvalue = 6.36
  Group = -> [Hg_element001,I_element004]
  conduct = 2
  density = 1
  expand = 3
  formula = G4_MERCURIC_IODIDE
  name = G4_MERCURIC_IODIDE
  specific = 4
FEATURE [App::DocumentObjectGroupPython] C_element059  label="C_element : 032"  # scripted group (container) (typed FeaturePython)
  n = 1
  ref = C_element
FEATURE [App::DocumentObjectGroupPython] H_element053  label="H_element : 028"  # scripted group (container) (typed FeaturePython)
  n = 4
  ref = H_element
FEATURE [App::DocumentObjectGroupPython] G4_METHANE  # scripted group (container) (typed FeaturePython)
  Dunit = g/cm3
  Dvalue = 0.000667151
  Group = -> [C_element059,H_element053]
  conduct = 2
  density = 1
  expand = 3
  formula = G4_METHANE
  name = G4_METHANE
  specific = 4
FEATURE [App::DocumentObjectGroupPython] C_element060  label="C_element : 033"  # scripted group (container) (typed FeaturePython)
  n = 1
  ref = C_element
FEATURE [App::DocumentObjectGroupPython] H_element054  label="H_element : 029"  # scripted group (container) (typed FeaturePython)
  n = 4
  ref = H_element
FEATURE [App::DocumentObjectGroupPython] O_element062  label="O_element : 033"  # scripted group (container) (typed FeaturePython)
  n = 1
  ref = O_element
FEATURE [App::DocumentObjectGroupPython] G4_METHANOL  # scripted group (container) (typed FeaturePython)
  Dunit = g/cm3
  Dvalue = 0.7914
  Group = -> [C_element060,H_element054,O_element062]
  conduct = 2
  density = 1
  expand = 3
  formula = G4_METHANOL
  name = G4_METHANOL
  specific = 4
FEATURE [App::DocumentObjectGroupPython] H_element055  label="H_element : 0.134"  # scripted group (container) (typed FeaturePython)
  n = 0.13404
FEATURE [App::DocumentObjectGroupPython] C_element061  label="C_element : 0.778"  # scripted group (container) (typed FeaturePython)
  n = 0.77796
FEATURE [App::DocumentObjectGroupPython] O_element063  label="O_element : 0.035"  # scripted group (container) (typed FeaturePython)
  n = 0.03502
FEATURE [App::DocumentObjectGroupPython] Mg_element009  label="Mg_element : 0.039"  # scripted group (container) (typed FeaturePython)
  n = 0.038594
FEATURE [App::DocumentObjectGroupPython] Ti_element002  label="Ti_element : 0.014"  # scripted group (container) (typed FeaturePython)
  n = 0.014386
FEATURE [App::DocumentObjectGroupPython] G4_MIX_D_WAX  # scripted group (container) (typed FeaturePython)
  Dunit = g/cm3
  Dvalue = 0.99
  Group = -> [H_element055,C_element061,O_element063,Mg_element009,Ti_element002]
  conduct = 2
  density = 1
  expand = 3
  formula = G4_MIX_D_WAX
  name = G4_MIX_D_WAX
  specific = 4
FEATURE [App::DocumentObjectGroupPython] H_element056  label="H_element : 0.135"  # scripted group (container) (typed FeaturePython)
  n = 0.081192
FEATURE [App::DocumentObjectGroupPython] C_element062  label="C_element : 0.583"  # scripted group (container) (typed FeaturePython)
  n = 0.583442
FEATURE [App::DocumentObjectGroupPython] N_element024  label="N_element : 0.018"  # scripted group (container) (typed FeaturePython)
  n = 0.017798
FEATURE [App::DocumentObjectGroupPython] O_element064  label="O_element : 0.186"  # scripted group (container) (typed FeaturePython)
  n = 0.186381
FEATURE [App::DocumentObjectGroupPython] Mg_element010  label="Mg_element : 0.130"  # scripted group (container) (typed FeaturePython)
  n = 0.130287
FEATURE [App::DocumentObjectGroupPython] Cl_element015  label="Cl_element : 0.588"  # scripted group (container) (typed FeaturePython)
  n = 0.0009
FEATURE [App::DocumentObjectGroupPython] G4_MS20_TISSUE  # scripted group (container) (typed FeaturePython)
  Dunit = g/cm3
  Dvalue = 1
  Group = -> [H_element056,C_element062,N_element024,O_element064,Mg_element010,Cl_element015]
  conduct = 2
  density = 1
  expand = 3
  formula = G4_MS20_TISSUE
  name = G4_MS20_TISSUE
  specific = 4
FEATURE [App::DocumentObjectGroupPython] H_element057  label="H_element : 0.136"  # scripted group (container) (typed FeaturePython)
  n = 0.102
FEATURE [App::DocumentObjectGroupPython] C_element063  label="C_element : 0.143"  # scripted group (container) (typed FeaturePython)
  n = 0.143
FEATURE [App::DocumentObjectGroupPython] N_element025  label="N_element : 0.034"  # scripted group (container) (typed FeaturePython)
  n = 0.034
FEATURE [App::DocumentObjectGroupPython] O_element065  label="O_element : 0.710"  # scripted group (container) (typed FeaturePython)
  n = 0.71
FEATURE [App::DocumentObjectGroupPython] Na_element011  label="Na_element : 0.098"  # scripted group (container) (typed FeaturePython)
  n = 0.001
FEATURE [App::DocumentObjectGroupPython] P_element007  label="P_element : 0.002"  # scripted group (container) (typed FeaturePython)
  n = 0.002
FEATURE [App::DocumentObjectGroupPython] S_element017  label="S_element : 0.018"  # scripted group (container) (typed FeaturePython)
  n = 0.003
FEATURE [App::DocumentObjectGroupPython] Cl_element016  label="Cl_element : 0.589"  # scripted group (container) (typed FeaturePython)
  n = 0.001
FEATURE [App::DocumentObjectGroupPython] K_element006  label="K_element : 0.004"  # scripted group (container) (typed FeaturePython)
  n = 0.004
FEATURE [App::DocumentObjectGroupPython] G4_MUSCLE_SKELETAL_ICRP  # scripted group (container) (typed FeaturePython)
  Dunit = g/cm3
  Dvalue = 1.05
  Group = -> [H_element057,C_element063,N_element025,O_element065,Na_element011,P_element007,S_element017,Cl_element016,K_element006]
  conduct = 2
  density = 1
  expand = 3
  formula = G4_MUSCLE_SKELETAL_ICRP
  name = G4_MUSCLE_SKELETAL_ICRP
  specific = 4
FEATURE [App::DocumentObjectGroupPython] H_element058  label="H_element : 0.137"  # scripted group (container) (typed FeaturePython)
  n = 0.102102
FEATURE [App::DocumentObjectGroupPython] C_element064  label="C_element : 0.123"  # scripted group (container) (typed FeaturePython)
  n = 0.123123
FEATURE [App::DocumentObjectGroupPython] N_element026  label="N_element : 0.756"  # scripted group (container) (typed FeaturePython)
  n = 0.035035
FEATURE [App::DocumentObjectGroupPython] O_element066  label="O_element : 0.730"  # scripted group (container) (typed FeaturePython)
  n = 0.72973
FEATURE [App::DocumentObjectGroupPython] Na_element012  label="Na_element : 0.099"  # scripted group (container) (typed FeaturePython)
  n = 0.001001
FEATURE [App::DocumentObjectGroupPython] P_element008  label="P_element : 0.106"  # scripted group (container) (typed FeaturePython)
  n = 0.002002
FEATURE [App::DocumentObjectGroupPython] S_element018  label="S_element : 0.019"  # scripted group (container) (typed FeaturePython)
  n = 0.004004
FEATURE [App::DocumentObjectGroupPython] K_element007  label="K_element : 0.016"  # scripted group (container) (typed FeaturePython)
  n = 0.003003
FEATURE [App::DocumentObjectGroupPython] G4_MUSCLE_STRIATED_ICRU  # scripted group (container) (typed FeaturePython)
  Dunit = g/cm3
  Dvalue = 1.04
  Group = -> [H_element058,C_element064,N_element026,O_element066,Na_element012,P_element008,S_element018,K_element007]
  conduct = 2
  density = 1
  expand = 3
  formula = G4_MUSCLE_STRIATED_ICRU
  name = G4_MUSCLE_STRIATED_ICRU
  specific = 4
FEATURE [App::DocumentObjectGroupPython] H_element059  label="H_element : 0.098"  # scripted group (container) (typed FeaturePython)
  n = 0.0982341
FEATURE [App::DocumentObjectGroupPython] C_element065  label="C_element : 0.156"  # scripted group (container) (typed FeaturePython)
  n = 0.156214
FEATURE [App::DocumentObjectGroupPython] N_element027  label="N_element : 0.757"  # scripted group (container) (typed FeaturePython)
  n = 0.035451
FEATURE [App::DocumentObjectGroupPython] O_element067  label="O_element : 0.880"  # scripted group (container) (typed FeaturePython)
  n = 0.710101
FEATURE [App::DocumentObjectGroupPython] G4_MUSCLE_WITH_SUCROSE  # scripted group (container) (typed FeaturePython)
  Dunit = g/cm3
  Dvalue = 1.11
  Group = -> [H_element059,C_element065,N_element027,O_element067]
  conduct = 2
  density = 1
  expand = 3
  formula = G4_MUSCLE_WITH_SUCROSE
  name = G4_MUSCLE_WITH_SUCROSE
  specific = 4
FEATURE [App::DocumentObjectGroupPython] H_element060  label="H_element : 0.138"  # scripted group (container) (typed FeaturePython)
  n = 0.101969
FEATURE [App::DocumentObjectGroupPython] C_element066  label="C_element : 0.120"  # scripted group (container) (typed FeaturePython)
  n = 0.120058
FEATURE [App::DocumentObjectGroupPython] N_element028  label="N_element : 0.758"  # scripted group (container) (typed FeaturePython)
  n = 0.035451
FEATURE [App::DocumentObjectGroupPython] O_element068  label="O_element : 0.743"  # scripted group (container) (typed FeaturePython)
  n = 0.742522
FEATURE [App::DocumentObjectGroupPython] G4_MUSCLE_WITHOUT_SUCROSE  # scripted group (container) (typed FeaturePython)
  Dunit = g/cm3
  Dvalue = 1.07
  Group = -> [H_element060,C_element066,N_element028,O_element068]
  conduct = 2
  density = 1
  expand = 3
  formula = G4_MUSCLE_WITHOUT_SUCROSE
  name = G4_MUSCLE_WITHOUT_SUCROSE
  specific = 4
FEATURE [App::DocumentObjectGroupPython] C_element067  label="C_element : 10"  # scripted group (container) (typed FeaturePython)
  n = 10
  ref = C_element
FEATURE [App::DocumentObjectGroupPython] H_element061  label="H_element : 030"  # scripted group (container) (typed FeaturePython)
  n = 8
  ref = H_element
FEATURE [App::DocumentObjectGroupPython] G4_NAPHTHALENE  # scripted group (container) (typed FeaturePython)
  Dunit = g/cm3
  Dvalue = 1.145
  Group = -> [C_element067,H_element061]
  conduct = 2
  density = 1
  expand = 3
  formula = G4_NAPHTHALENE
  name = G4_NAPHTHALENE
  specific = 4
FEATURE [App::DocumentObjectGroupPython] C_element068  label="C_element : 034"  # scripted group (container) (typed FeaturePython)
  n = 6
  ref = C_element
FEATURE [App::DocumentObjectGroupPython] H_element062  label="H_element : 031"  # scripted group (container) (typed FeaturePython)
  n = 5
  ref = H_element
FEATURE [App::DocumentObjectGroupPython] N_element029  label="N_element : 012"  # scripted group (container) (typed FeaturePython)
  n = 1
  ref = N_element
FEATURE [App::DocumentObjectGroupPython] O_element069  label="O_element : 034"  # scripted group (container) (typed FeaturePython)
  n = 2
  ref = O_element
FEATURE [App::DocumentObjectGroupPython] G4_NITROBENZENE  # scripted group (container) (typed FeaturePython)
  Dunit = g/cm3
  Dvalue = 1.19867
  Group = -> [C_element068,H_element062,N_element029,O_element069]
  conduct = 2
  density = 1
  expand = 3
  formula = G4_NITROBENZENE
  name = G4_NITROBENZENE
  specific = 4
FEATURE [App::DocumentObjectGroupPython] N_element030  label="N_element : 013"  # scripted group (container) (typed FeaturePython)
  n = 2
  ref = N_element
FEATURE [App::DocumentObjectGroupPython] O_element070  label="O_element : 035"  # scripted group (container) (typed FeaturePython)
  n = 1
  ref = O_element
FEATURE [App::DocumentObjectGroupPython] G4_NITROUS_OXIDE  # scripted group (container) (typed FeaturePython)
  Dunit = g/cm3
  Dvalue = 0.00183094
  Group = -> [N_element030,O_element070]
  conduct = 2
  density = 1
  expand = 3
  formula = G4_NITROUS_OXIDE
  name = G4_NITROUS_OXIDE
  specific = 4
FEATURE [App::DocumentObjectGroupPython] H_element063  label="H_element : 0.104"  # scripted group (container) (typed FeaturePython)
  n = 0.103509
FEATURE [App::DocumentObjectGroupPython] C_element069  label="C_element : 0.648"  # scripted group (container) (typed FeaturePython)
  n = 0.648416
FEATURE [App::DocumentObjectGroupPython] N_element031  label="N_element : 0.100"  # scripted group (container) (typed FeaturePython)
  n = 0.0995361
FEATURE [App::DocumentObjectGroupPython] O_element071  label="O_element : 0.149"  # scripted group (container) (typed FeaturePython)
  n = 0.148539
FEATURE [App::DocumentObjectGroupPython] G4_NYLON_8062  label="G4_NYLON-8062"  # scripted group (container) (typed FeaturePython)
  Dunit = g/cm3
  Dvalue = 1.08
  Group = -> [H_element063,C_element069,N_element031,O_element071]
  conduct = 2
  density = 1
  expand = 3
  formula = G4_NYLON-8062
  name = G4_NYLON-8062
  specific = 4
FEATURE [App::DocumentObjectGroupPython] C_element070  label="C_element : 035"  # scripted group (container) (typed FeaturePython)
  n = 6
  ref = C_element
FEATURE [App::DocumentObjectGroupPython] H_element064  label="H_element : 11"  # scripted group (container) (typed FeaturePython)
  n = 11
  ref = H_element
FEATURE [App::DocumentObjectGroupPython] N_element032  label="N_element : 014"  # scripted group (container) (typed FeaturePython)
  n = 1
  ref = N_element
FEATURE [App::DocumentObjectGroupPython] O_element072  label="O_element : 036"  # scripted group (container) (typed FeaturePython)
  n = 1
  ref = O_element
FEATURE [App::DocumentObjectGroupPython] G4_NYLON_6_6  label="G4_NYLON-6-6"  # scripted group (container) (typed FeaturePython)
  Dunit = g/cm3
  Dvalue = 1.14
  Group = -> [C_element070,H_element064,N_element032,O_element072]
  conduct = 2
  density = 1
  expand = 3
  formula = G4_NYLON-6-6
  name = G4_NYLON-6-6
  specific = 4
FEATURE [App::DocumentObjectGroupPython] H_element065  label="H_element : 0.139"  # scripted group (container) (typed FeaturePython)
  n = 0.107062
FEATURE [App::DocumentObjectGroupPython] C_element071  label="C_element : 0.680"  # scripted group (container) (typed FeaturePython)
  n = 0.680449
FEATURE [App::DocumentObjectGroupPython] N_element033  label="N_element : 0.099"  # scripted group (container) (typed FeaturePython)
  n = 0.099189
FEATURE [App::DocumentObjectGroupPython] O_element073  label="O_element : 0.113"  # scripted group (container) (typed FeaturePython)
  n = 0.1133
FEATURE [App::DocumentObjectGroupPython] G4_NYLON_6_10  label="G4_NYLON-6-10"  # scripted group (container) (typed FeaturePython)
  Dunit = g/cm3
  Dvalue = 1.14
  Group = -> [H_element065,C_element071,N_element033,O_element073]
  conduct = 2
  density = 1
  expand = 3
  formula = G4_NYLON-6-10
  name = G4_NYLON-6-10
  specific = 4
FEATURE [App::DocumentObjectGroupPython] H_element066  label="H_element : 0.140"  # scripted group (container) (typed FeaturePython)
  n = 0.115476
FEATURE [App::DocumentObjectGroupPython] C_element072  label="C_element : 0.721"  # scripted group (container) (typed FeaturePython)
  n = 0.720818
FEATURE [App::DocumentObjectGroupPython] N_element034  label="N_element : 0.076"  # scripted group (container) (typed FeaturePython)
  n = 0.0764169
FEATURE [App::DocumentObjectGroupPython] O_element074  label="O_element : 0.087"  # scripted group (container) (typed FeaturePython)
  n = 0.0872889
FEATURE [App::DocumentObjectGroupPython] G4_NYLON_11_RILSAN  label="G4_NYLON-11_RILSAN"  # scripted group (container) (typed FeaturePython)
  Dunit = g/cm3
  Dvalue = 1.425
  Group = -> [H_element066,C_element072,N_element034,O_element074]
  conduct = 2
  density = 1
  expand = 3
  formula = G4_NYLON-11_RILSAN
  name = G4_NYLON-11_RILSAN
  specific = 4
FEATURE [App::DocumentObjectGroupPython] C_element073  label="C_element : 8"  # scripted group (container) (typed FeaturePython)
  n = 8
  ref = C_element
FEATURE [App::DocumentObjectGroupPython] H_element067  label="H_element : 18"  # scripted group (container) (typed FeaturePython)
  n = 18
  ref = H_element
FEATURE [App::DocumentObjectGroupPython] G4_OCTANE  # scripted group (container) (typed FeaturePython)
  Dunit = g/cm3
  Dvalue = 0.7026
  Group = -> [C_element073,H_element067]
  conduct = 2
  density = 1
  expand = 3
  formula = G4_OCTANE
  name = G4_OCTANE
  specific = 4
FEATURE [App::DocumentObjectGroupPython] C_element074  label="C_element : 25"  # scripted group (container) (typed FeaturePython)
  n = 25
  ref = C_element
FEATURE [App::DocumentObjectGroupPython] H_element068  label="H_element : 52"  # scripted group (container) (typed FeaturePython)
  n = 52
  ref = H_element
FEATURE [App::DocumentObjectGroupPython] G4_PARAFFIN  # scripted group (container) (typed FeaturePython)
  Dunit = g/cm3
  Dvalue = 0.93
  Group = -> [C_element074,H_element068]
  conduct = 2
  density = 1
  expand = 3
  formula = G4_PARAFFIN
  name = G4_PARAFFIN
  specific = 4
FEATURE [App::DocumentObjectGroupPython] C_element075  label="C_element : 036"  # scripted group (container) (typed FeaturePython)
  n = 5
  ref = C_element
FEATURE [App::DocumentObjectGroupPython] H_element069  label="H_element : 032"  # scripted group (container) (typed FeaturePython)
  n = 12
  ref = H_element
FEATURE [App::DocumentObjectGroupPython] G4_N_PENTANE  label="G4_N-PENTANE"  # scripted group (container) (typed FeaturePython)
  Dunit = g/cm3
  Dvalue = 0.6262
  Group = -> [C_element075,H_element069]
  conduct = 2
  density = 1
  expand = 3
  formula = G4_N-PENTANE
  name = G4_N-PENTANE
  specific = 4
FEATURE [App::DocumentObjectGroupPython] H_element070  label="H_element : 0.014"  # scripted group (container) (typed FeaturePython)
  n = 0.0141
FEATURE [App::DocumentObjectGroupPython] C_element076  label="C_element : 0.072"  # scripted group (container) (typed FeaturePython)
  n = 0.072261
FEATURE [App::DocumentObjectGroupPython] N_element035  label="N_element : 0.019"  # scripted group (container) (typed FeaturePython)
  n = 0.01932
FEATURE [App::DocumentObjectGroupPython] O_element075  label="O_element : 0.066"  # scripted group (container) (typed FeaturePython)
  n = 0.066101
FEATURE [App::DocumentObjectGroupPython] S_element019  label="S_element : 0.020"  # scripted group (container) (typed FeaturePython)
  n = 0.00189
FEATURE [App::DocumentObjectGroupPython] Br_element004  label="Br_element : 0.349"  # scripted group (container) (typed FeaturePython)
  n = 0.349103
FEATURE [App::DocumentObjectGroupPython] Ag_element001  label="Ag_element : 0.474"  # scripted group (container) (typed FeaturePython)
  n = 0.474105
FEATURE [App::DocumentObjectGroupPython] I_element005  label="I_element : 0.003"  # scripted group (container) (typed FeaturePython)
  n = 0.00312
FEATURE [App::DocumentObjectGroupPython] G4_PHOTO_EMULSION  # scripted group (container) (typed FeaturePython)
  Dunit = g/cm3
  Dvalue = 3.815
  Group = -> [H_element070,C_element076,N_element035,O_element075,S_element019,Br_element004,Ag_element001,I_element005]
  conduct = 2
  density = 1
  expand = 3
  formula = G4_PHOTO_EMULSION
  name = G4_PHOTO_EMULSION
  specific = 4
FEATURE [App::DocumentObjectGroupPython] C_element077  label="C_element : 9"  # scripted group (container) (typed FeaturePython)
  n = 9
  ref = C_element
FEATURE [App::DocumentObjectGroupPython] H_element071  label="H_element : 033"  # scripted group (container) (typed FeaturePython)
  n = 10
  ref = H_element
FEATURE [App::DocumentObjectGroupPython] G4_PLASTIC_SC_VINYLTOLUENE  # scripted group (container) (typed FeaturePython)
  Dunit = g/cm3
  Dvalue = 1.032
  Group = -> [C_element077,H_element071]
  conduct = 2
  density = 1
  expand = 3
  formula = G4_PLASTIC_SC_VINYLTOLUENE
  name = G4_PLASTIC_SC_VINYLTOLUENE
  specific = 4
FEATURE [App::DocumentObjectGroupPython] Pu_element001  label="Pu_element : 1"  # scripted group (container) (typed FeaturePython)
  n = 1
  ref = Pu_element
FEATURE [App::DocumentObjectGroupPython] O_element076  label="O_element : 037"  # scripted group (container) (typed FeaturePython)
  n = 2
  ref = O_element
FEATURE [App::DocumentObjectGroupPython] G4_PLUTONIUM_DIOXIDE  # scripted group (container) (typed FeaturePython)
  Dunit = g/cm3
  Dvalue = 11.46
  Group = -> [Pu_element001,O_element076]
  conduct = 2
  density = 1
  expand = 3
  formula = G4_PLUTONIUM_DIOXIDE
  name = G4_PLUTONIUM_DIOXIDE
  specific = 4
FEATURE [App::DocumentObjectGroupPython] C_element078  label="C_element : 037"  # scripted group (container) (typed FeaturePython)
  n = 3
  ref = C_element
FEATURE [App::DocumentObjectGroupPython] H_element072  label="H_element : 034"  # scripted group (container) (typed FeaturePython)
  n = 3
  ref = H_element
FEATURE [App::DocumentObjectGroupPython] N_element036  label="N_element : 015"  # scripted group (container) (typed FeaturePython)
  n = 1
  ref = N_element
FEATURE [App::DocumentObjectGroupPython] G4_POLYACRYLONITRILE  # scripted group (container) (typed FeaturePython)
  Dunit = g/cm3
  Dvalue = 1.17
  Group = -> [C_element078,H_element072,N_element036]
  conduct = 2
  density = 1
  expand = 3
  formula = G4_POLYACRYLONITRILE
  name = G4_POLYACRYLONITRILE
  specific = 4
FEATURE [App::DocumentObjectGroupPython] C_element079  label="C_element : 16"  # scripted group (container) (typed FeaturePython)
  n = 16
  ref = C_element
FEATURE [App::DocumentObjectGroupPython] H_element073  label="H_element : 035"  # scripted group (container) (typed FeaturePython)
  n = 14
  ref = H_element
FEATURE [App::DocumentObjectGroupPython] O_element077  label="O_element : 038"  # scripted group (container) (typed FeaturePython)
  n = 3
  ref = O_element
FEATURE [App::DocumentObjectGroupPython] G4_POLYCARBONATE  # scripted group (container) (typed FeaturePython)
  Dunit = g/cm3
  Dvalue = 1.2
  Group = -> [C_element079,H_element073,O_element077]
  conduct = 2
  density = 1
  expand = 3
  formula = G4_POLYCARBONATE
  name = G4_POLYCARBONATE
  specific = 4
FEATURE [App::DocumentObjectGroupPython] C_element080  label="C_element : 038"  # scripted group (container) (typed FeaturePython)
  n = 8
  ref = C_element
FEATURE [App::DocumentObjectGroupPython] H_element074  label="H_element : 036"  # scripted group (container) (typed FeaturePython)
  n = 7
  ref = H_element
FEATURE [App::DocumentObjectGroupPython] Cl_element017  label="Cl_element : 007"  # scripted group (container) (typed FeaturePython)
  n = 1
  ref = Cl_element
FEATURE [App::DocumentObjectGroupPython] G4_POLYCHLOROSTYRENE  # scripted group (container) (typed FeaturePython)
  Dunit = g/cm3
  Dvalue = 1.3
  Group = -> [C_element080,H_element074,Cl_element017]
  conduct = 2
  density = 1
  expand = 3
  formula = G4_POLYCHLOROSTYRENE
  name = G4_POLYCHLOROSTYRENE
  specific = 4
FEATURE [App::DocumentObjectGroupPython] C_element081  label="C_element : 039"  # scripted group (container) (typed FeaturePython)
  n = 1
  ref = C_element
FEATURE [App::DocumentObjectGroupPython] H_element075  label="H_element : 037"  # scripted group (container) (typed FeaturePython)
  n = 2
  ref = H_element
FEATURE [App::DocumentObjectGroupPython] G4_POLYETHYLENE  # scripted group (container) (typed FeaturePython)
  Dunit = g/cm3
  Dvalue = 0.94
  Group = -> [C_element081,H_element075]
  conduct = 2
  density = 1
  expand = 3
  formula = G4_POLYETHYLENE
  name = G4_POLYETHYLENE
  specific = 4
FEATURE [App::DocumentObjectGroupPython] C_element082  label="C_element : 040"  # scripted group (container) (typed FeaturePython)
  n = 10
  ref = C_element
FEATURE [App::DocumentObjectGroupPython] H_element076  label="H_element : 038"  # scripted group (container) (typed FeaturePython)
  n = 8
  ref = H_element
FEATURE [App::DocumentObjectGroupPython] O_element078  label="O_element : 039"  # scripted group (container) (typed FeaturePython)
  n = 4
  ref = O_element
FEATURE [App::DocumentObjectGroupPython] G4_MYLAR  # scripted group (container) (typed FeaturePython)
  Dunit = g/cm3
  Dvalue = 1.4
  Group = -> [C_element082,H_element076,O_element078]
  conduct = 2
  density = 1
  expand = 3
  formula = G4_MYLAR
  name = G4_MYLAR
  specific = 4
FEATURE [App::DocumentObjectGroupPython] C_element083  label="C_element : 041"  # scripted group (container) (typed FeaturePython)
  n = 5
  ref = C_element
FEATURE [App::DocumentObjectGroupPython] H_element077  label="H_element : 039"  # scripted group (container) (typed FeaturePython)
  n = 8
  ref = H_element
FEATURE [App::DocumentObjectGroupPython] O_element079  label="O_element : 040"  # scripted group (container) (typed FeaturePython)
  n = 2
  ref = O_element
FEATURE [App::DocumentObjectGroupPython] G4_PLEXIGLASS  # scripted group (container) (typed FeaturePython)
  Dunit = g/cm3
  Dvalue = 1.19
  Group = -> [C_element083,H_element077,O_element079]
  conduct = 2
  density = 1
  expand = 3
  formula = G4_PLEXIGLASS
  name = G4_PLEXIGLASS
  specific = 4
FEATURE [App::DocumentObjectGroupPython] C_element084  label="C_element : 042"  # scripted group (container) (typed FeaturePython)
  n = 1
  ref = C_element
FEATURE [App::DocumentObjectGroupPython] H_element078  label="H_element : 040"  # scripted group (container) (typed FeaturePython)
  n = 2
  ref = H_element
FEATURE [App::DocumentObjectGroupPython] O_element080  label="O_element : 041"  # scripted group (container) (typed FeaturePython)
  n = 1
  ref = O_element
FEATURE [App::DocumentObjectGroupPython] G4_POLYOXYMETHYLENE  # scripted group (container) (typed FeaturePython)
  Dunit = g/cm3
  Dvalue = 1.425
  Group = -> [C_element084,H_element078,O_element080]
  conduct = 2
  density = 1
  expand = 3
  formula = G4_POLYOXYMETHYLENE
  name = G4_POLYOXYMETHYLENE
  specific = 4
FEATURE [App::DocumentObjectGroupPython] C_element085  label="C_element : 043"  # scripted group (container) (typed FeaturePython)
  n = 2
  ref = C_element
FEATURE [App::DocumentObjectGroupPython] H_element079  label="H_element : 041"  # scripted group (container) (typed FeaturePython)
  n = 4
  ref = H_element
FEATURE [App::DocumentObjectGroupPython] G4_POLYPROPYLENE  # scripted group (container) (typed FeaturePython)
  Dunit = g/cm3
  Dvalue = 0.9
  Group = -> [C_element085,H_element079]
  conduct = 2
  density = 1
  expand = 3
  formula = G4_POLYPROPYLENE
  name = G4_POLYPROPYLENE
  specific = 4
FEATURE [App::DocumentObjectGroupPython] C_element086  label="C_element : 044"  # scripted group (container) (typed FeaturePython)
  n = 8
  ref = C_element
FEATURE [App::DocumentObjectGroupPython] H_element080  label="H_element : 042"  # scripted group (container) (typed FeaturePython)
  n = 8
  ref = H_element
FEATURE [App::DocumentObjectGroupPython] G4_POLYSTYRENE  # scripted group (container) (typed FeaturePython)
  Dunit = g/cm3
  Dvalue = 1.06
  Group = -> [C_element086,H_element080]
  conduct = 2
  density = 1
  expand = 3
  formula = G4_POLYSTYRENE
  name = G4_POLYSTYRENE
  specific = 4
FEATURE [App::DocumentObjectGroupPython] C_element087  label="C_element : 045"  # scripted group (container) (typed FeaturePython)
  n = 2
  ref = C_element
FEATURE [App::DocumentObjectGroupPython] F_element014  label="F_element : 4"  # scripted group (container) (typed FeaturePython)
  n = 4
  ref = F_element
FEATURE [App::DocumentObjectGroupPython] G4_TEFLON  # scripted group (container) (typed FeaturePython)
  Dunit = g/cm3
  Dvalue = 2.2
  Group = -> [C_element087,F_element014]
  conduct = 2
  density = 1
  expand = 3
  formula = G4_TEFLON
  name = G4_TEFLON
  specific = 4
FEATURE [App::DocumentObjectGroupPython] C_element088  label="C_element : 046"  # scripted group (container) (typed FeaturePython)
  n = 2
  ref = C_element
FEATURE [App::DocumentObjectGroupPython] F_element015  label="F_element : 006"  # scripted group (container) (typed FeaturePython)
  n = 3
  ref = F_element
FEATURE [App::DocumentObjectGroupPython] Cl_element018  label="Cl_element : 008"  # scripted group (container) (typed FeaturePython)
  n = 1
  ref = Cl_element
FEATURE [App::DocumentObjectGroupPython] G4_POLYTRIFLUOROCHLOROETHYLENE  # scripted group (container) (typed FeaturePython)
  Dunit = g/cm3
  Dvalue = 2.1
  Group = -> [C_element088,F_element015,Cl_element018]
  conduct = 2
  density = 1
  expand = 3
  formula = G4_POLYTRIFLUOROCHLOROETHYLENE
  name = G4_POLYTRIFLUOROCHLOROETHYLENE
  specific = 4
FEATURE [App::DocumentObjectGroupPython] C_element089  label="C_element : 047"  # scripted group (container) (typed FeaturePython)
  n = 4
  ref = C_element
FEATURE [App::DocumentObjectGroupPython] H_element081  label="H_element : 043"  # scripted group (container) (typed FeaturePython)
  n = 6
  ref = H_element
FEATURE [App::DocumentObjectGroupPython] O_element081  label="O_element : 042"  # scripted group (container) (typed FeaturePython)
  n = 2
  ref = O_element
FEATURE [App::DocumentObjectGroupPython] G4_POLYVINYL_ACETATE  # scripted group (container) (typed FeaturePython)
  Dunit = g/cm3
  Dvalue = 1.19
  Group = -> [C_element089,H_element081,O_element081]
  conduct = 2
  density = 1
  expand = 3
  formula = G4_POLYVINYL_ACETATE
  name = G4_POLYVINYL_ACETATE
  specific = 4
FEATURE [App::DocumentObjectGroupPython] C_element090  label="C_element : 048"  # scripted group (container) (typed FeaturePython)
  n = 2
  ref = C_element
FEATURE [App::DocumentObjectGroupPython] H_element082  label="H_element : 044"  # scripted group (container) (typed FeaturePython)
  n = 4
  ref = H_element
FEATURE [App::DocumentObjectGroupPython] O_element082  label="O_element : 043"  # scripted group (container) (typed FeaturePython)
  n = 1
  ref = O_element
FEATURE [App::DocumentObjectGroupPython] G4_POLYVINYL_ALCOHOL  # scripted group (container) (typed FeaturePython)
  Dunit = g/cm3
  Dvalue = 1.3
  Group = -> [C_element090,H_element082,O_element082]
  conduct = 2
  density = 1
  expand = 3
  formula = G4_POLYVINYL_ALCOHOL
  name = G4_POLYVINYL_ALCOHOL
  specific = 4
FEATURE [App::DocumentObjectGroupPython] C_element091  label="C_element : 049"  # scripted group (container) (typed FeaturePython)
  n = 8
  ref = C_element
FEATURE [App::DocumentObjectGroupPython] H_element083  label="H_element : 045"  # scripted group (container) (typed FeaturePython)
  n = 14
  ref = H_element
FEATURE [App::DocumentObjectGroupPython] O_element083  label="O_element : 044"  # scripted group (container) (typed FeaturePython)
  n = 2
  ref = O_element
FEATURE [App::DocumentObjectGroupPython] G4_POLYVINYL_BUTYRAL  # scripted group (container) (typed FeaturePython)
  Dunit = g/cm3
  Dvalue = 1.12
  Group = -> [C_element091,H_element083,O_element083]
  conduct = 2
  density = 1
  expand = 3
  formula = G4_POLYVINYL_BUTYRAL
  name = G4_POLYVINYL_BUTYRAL
  specific = 4
FEATURE [App::DocumentObjectGroupPython] C_element092  label="C_element : 050"  # scripted group (container) (typed FeaturePython)
  n = 2
  ref = C_element
FEATURE [App::DocumentObjectGroupPython] H_element084  label="H_element : 046"  # scripted group (container) (typed FeaturePython)
  n = 3
  ref = H_element
FEATURE [App::DocumentObjectGroupPython] Cl_element019  label="Cl_element : 009"  # scripted group (container) (typed FeaturePython)
  n = 1
  ref = Cl_element
FEATURE [App::DocumentObjectGroupPython] G4_POLYVINYL_CHLORIDE  # scripted group (container) (typed FeaturePython)
  Dunit = g/cm3
  Dvalue = 1.3
  Group = -> [C_element092,H_element084,Cl_element019]
  conduct = 2
  density = 1
  expand = 3
  formula = G4_POLYVINYL_CHLORIDE
  name = G4_POLYVINYL_CHLORIDE
  specific = 4
FEATURE [App::DocumentObjectGroupPython] C_element093  label="C_element : 051"  # scripted group (container) (typed FeaturePython)
  n = 2
  ref = C_element
FEATURE [App::DocumentObjectGroupPython] H_element085  label="H_element : 047"  # scripted group (container) (typed FeaturePython)
  n = 2
  ref = H_element
FEATURE [App::DocumentObjectGroupPython] Cl_element020  label="Cl_element : 010"  # scripted group (container) (typed FeaturePython)
  n = 2
  ref = Cl_element
FEATURE [App::DocumentObjectGroupPython] G4_POLYVINYLIDENE_CHLORIDE  # scripted group (container) (typed FeaturePython)
  Dunit = g/cm3
  Dvalue = 1.7
  Group = -> [C_element093,H_element085,Cl_element020]
  conduct = 2
  density = 1
  expand = 3
  formula = G4_POLYVINYLIDENE_CHLORIDE
  name = G4_POLYVINYLIDENE_CHLORIDE
  specific = 4
FEATURE [App::DocumentObjectGroupPython] C_element094  label="C_element : 052"  # scripted group (container) (typed FeaturePython)
  n = 2
  ref = C_element
FEATURE [App::DocumentObjectGroupPython] H_element086  label="H_element : 048"  # scripted group (container) (typed FeaturePython)
  n = 2
  ref = H_element
FEATURE [App::DocumentObjectGroupPython] F_element016  label="F_element : 007"  # scripted group (container) (typed FeaturePython)
  n = 2
  ref = F_element
FEATURE [App::DocumentObjectGroupPython] G4_POLYVINYLIDENE_FLUORIDE  # scripted group (container) (typed FeaturePython)
  Dunit = g/cm3
  Dvalue = 1.76
  Group = -> [C_element094,H_element086,F_element016]
  conduct = 2
  density = 1
  expand = 3
  formula = G4_POLYVINYLIDENE_FLUORIDE
  name = G4_POLYVINYLIDENE_FLUORIDE
  specific = 4
FEATURE [App::DocumentObjectGroupPython] C_element095  label="C_element : 053"  # scripted group (container) (typed FeaturePython)
  n = 6
  ref = C_element
FEATURE [App::DocumentObjectGroupPython] H_element087  label="H_element : 9"  # scripted group (container) (typed FeaturePython)
  n = 9
  ref = H_element
FEATURE [App::DocumentObjectGroupPython] N_element037  label="N_element : 016"  # scripted group (container) (typed FeaturePython)
  n = 1
  ref = N_element
FEATURE [App::DocumentObjectGroupPython] O_element084  label="O_element : 045"  # scripted group (container) (typed FeaturePython)
  n = 1
  ref = O_element
FEATURE [App::DocumentObjectGroupPython] G4_POLYVINYL_PYRROLIDONE  # scripted group (container) (typed FeaturePython)
  Dunit = g/cm3
  Dvalue = 1.25
  Group = -> [C_element095,H_element087,N_element037,O_element084]
  conduct = 2
  density = 1
  expand = 3
  formula = G4_POLYVINYL_PYRROLIDONE
  name = G4_POLYVINYL_PYRROLIDONE
  specific = 4
FEATURE [App::DocumentObjectGroupPython] K_element008  label="K_element : 1"  # scripted group (container) (typed FeaturePython)
  n = 1
  ref = K_element
FEATURE [App::DocumentObjectGroupPython] I_element006  label="I_element : 003"  # scripted group (container) (typed FeaturePython)
  n = 1
  ref = I_element
FEATURE [App::DocumentObjectGroupPython] G4_POTASSIUM_IODIDE  # scripted group (container) (typed FeaturePython)
  Dunit = g/cm3
  Dvalue = 3.13
  Group = -> [K_element008,I_element006]
  conduct = 2
  density = 1
  expand = 3
  formula = G4_POTASSIUM_IODIDE
  name = G4_POTASSIUM_IODIDE
  specific = 4
FEATURE [App::DocumentObjectGroupPython] K_element009  label="K_element : 2"  # scripted group (container) (typed FeaturePython)
  n = 2
  ref = K_element
FEATURE [App::DocumentObjectGroupPython] O_element085  label="O_element : 046"  # scripted group (container) (typed FeaturePython)
  n = 1
  ref = O_element
FEATURE [App::DocumentObjectGroupPython] G4_POTASSIUM_OXIDE  # scripted group (container) (typed FeaturePython)
  Dunit = g/cm3
  Dvalue = 2.32
  Group = -> [K_element009,O_element085]
  conduct = 2
  density = 1
  expand = 3
  formula = G4_POTASSIUM_OXIDE
  name = G4_POTASSIUM_OXIDE
  specific = 4
FEATURE [App::DocumentObjectGroupPython] C_element096  label="C_element : 054"  # scripted group (container) (typed FeaturePython)
  n = 3
  ref = C_element
FEATURE [App::DocumentObjectGroupPython] H_element088  label="H_element : 049"  # scripted group (container) (typed FeaturePython)
  n = 8
  ref = H_element
FEATURE [App::DocumentObjectGroupPython] G4_PROPANE  # scripted group (container) (typed FeaturePython)
  Dunit = g/cm3
  Dvalue = 0.00187939
  Group = -> [C_element096,H_element088]
  conduct = 2
  density = 1
  expand = 3
  formula = G4_PROPANE
  name = G4_PROPANE
  specific = 4
FEATURE [App::DocumentObjectGroupPython] C_element097  label="C_element : 055"  # scripted group (container) (typed FeaturePython)
  n = 3
  ref = C_element
FEATURE [App::DocumentObjectGroupPython] H_element089  label="H_element : 050"  # scripted group (container) (typed FeaturePython)
  n = 8
  ref = H_element
FEATURE [App::DocumentObjectGroupPython] G4_lPROPANE  # scripted group (container) (typed FeaturePython)
  Dunit = g/cm3
  Dvalue = 0.43
  Group = -> [C_element097,H_element089]
  conduct = 2
  density = 1
  expand = 3
  formula = G4_lPROPANE
  name = G4_lPROPANE
  specific = 4
FEATURE [App::DocumentObjectGroupPython] C_element098  label="C_element : 056"  # scripted group (container) (typed FeaturePython)
  n = 3
  ref = C_element
FEATURE [App::DocumentObjectGroupPython] H_element090  label="H_element : 051"  # scripted group (container) (typed FeaturePython)
  n = 8
  ref = H_element
FEATURE [App::DocumentObjectGroupPython] O_element086  label="O_element : 047"  # scripted group (container) (typed FeaturePython)
  n = 1
  ref = O_element
FEATURE [App::DocumentObjectGroupPython] G4_N_PROPYL_ALCOHOL  label="G4_N-PROPYL_ALCOHOL"  # scripted group (container) (typed FeaturePython)
  Dunit = g/cm3
  Dvalue = 0.8035
  Group = -> [C_element098,H_element090,O_element086]
  conduct = 2
  density = 1
  expand = 3
  formula = G4_N-PROPYL_ALCOHOL
  name = G4_N-PROPYL_ALCOHOL
  specific = 4
FEATURE [App::DocumentObjectGroupPython] C_element099  label="C_element : 057"  # scripted group (container) (typed FeaturePython)
  n = 5
  ref = C_element
FEATURE [App::DocumentObjectGroupPython] H_element091  label="H_element : 052"  # scripted group (container) (typed FeaturePython)
  n = 5
  ref = H_element
FEATURE [App::DocumentObjectGroupPython] N_element038  label="N_element : 017"  # scripted group (container) (typed FeaturePython)
  n = 1
  ref = N_element
FEATURE [App::DocumentObjectGroupPython] G4_PYRIDINE  # scripted group (container) (typed FeaturePython)
  Dunit = g/cm3
  Dvalue = 0.9819
  Group = -> [C_element099,H_element091,N_element038]
  conduct = 2
  density = 1
  expand = 3
  formula = G4_PYRIDINE
  name = G4_PYRIDINE
  specific = 4
FEATURE [App::DocumentObjectGroupPython] H_element092  label="H_element : 0.144"  # scripted group (container) (typed FeaturePython)
  n = 0.143711
FEATURE [App::DocumentObjectGroupPython] C_element100  label="C_element : 0.856"  # scripted group (container) (typed FeaturePython)
  n = 0.856289
FEATURE [App::DocumentObjectGroupPython] G4_RUBBER_BUTYL  # scripted group (container) (typed FeaturePython)
  Dunit = g/cm3
  Dvalue = 0.92
  Group = -> [H_element092,C_element100]
  conduct = 2
  density = 1
  expand = 3
  formula = G4_RUBBER_BUTYL
  name = G4_RUBBER_BUTYL
  specific = 4
FEATURE [App::DocumentObjectGroupPython] H_element093  label="H_element : 0.118"  # scripted group (container) (typed FeaturePython)
  n = 0.118371
FEATURE [App::DocumentObjectGroupPython] C_element101  label="C_element : 0.882"  # scripted group (container) (typed FeaturePython)
  n = 0.881629
FEATURE [App::DocumentObjectGroupPython] G4_RUBBER_NATURAL  # scripted group (container) (typed FeaturePython)
  Dunit = g/cm3
  Dvalue = 0.92
  Group = -> [H_element093,C_element101]
  conduct = 2
  density = 1
  expand = 3
  formula = G4_RUBBER_NATURAL
  name = G4_RUBBER_NATURAL
  specific = 4
FEATURE [App::DocumentObjectGroupPython] H_element094  label="H_element : 0.145"  # scripted group (container) (typed FeaturePython)
  n = 0.05692
FEATURE [App::DocumentObjectGroupPython] C_element102  label="C_element : 0.543"  # scripted group (container) (typed FeaturePython)
  n = 0.542646
FEATURE [App::DocumentObjectGroupPython] Cl_element021  label="Cl_element : 0.400"  # scripted group (container) (typed FeaturePython)
  n = 0.400434
FEATURE [App::DocumentObjectGroupPython] G4_RUBBER_NEOPRENE  # scripted group (container) (typed FeaturePython)
  Dunit = g/cm3
  Dvalue = 1.23
  Group = -> [H_element094,C_element102,Cl_element021]
  conduct = 2
  density = 1
  expand = 3
  formula = G4_RUBBER_NEOPRENE
  name = G4_RUBBER_NEOPRENE
  specific = 4
FEATURE [App::DocumentObjectGroupPython] Si_element006  label="Si_element : 1"  # scripted group (container) (typed FeaturePython)
  n = 1
  ref = Si_element
FEATURE [App::DocumentObjectGroupPython] O_element087  label="O_element : 048"  # scripted group (container) (typed FeaturePython)
  n = 2
  ref = O_element
FEATURE [App::DocumentObjectGroupPython] G4_SILICON_DIOXIDE  # scripted group (container) (typed FeaturePython)
  Dunit = g/cm3
  Dvalue = 2.32
  Group = -> [Si_element006,O_element087]
  conduct = 2
  density = 1
  expand = 3
  formula = G4_SILICON_DIOXIDE
  name = G4_SILICON_DIOXIDE
  specific = 4
FEATURE [App::DocumentObjectGroupPython] Ag_element002  label="Ag_element : 1"  # scripted group (container) (typed FeaturePython)
  n = 1
  ref = Ag_element
FEATURE [App::DocumentObjectGroupPython] Br_element005  label="Br_element : 003"  # scripted group (container) (typed FeaturePython)
  n = 1
  ref = Br_element
FEATURE [App::DocumentObjectGroupPython] G4_SILVER_BROMIDE  # scripted group (container) (typed FeaturePython)
  Dunit = g/cm3
  Dvalue = 6.473
  Group = -> [Ag_element002,Br_element005]
  conduct = 2
  density = 1
  expand = 3
  formula = G4_SILVER_BROMIDE
  name = G4_SILVER_BROMIDE
  specific = 4
FEATURE [App::DocumentObjectGroupPython] Ag_element003  label="Ag_element : 002"  # scripted group (container) (typed FeaturePython)
  n = 1
  ref = Ag_element
FEATURE [App::DocumentObjectGroupPython] Cl_element022  label="Cl_element : 011"  # scripted group (container) (typed FeaturePython)
  n = 1
  ref = Cl_element
FEATURE [App::DocumentObjectGroupPython] G4_SILVER_CHLORIDE  # scripted group (container) (typed FeaturePython)
  Dunit = g/cm3
  Dvalue = 5.56
  Group = -> [Ag_element003,Cl_element022]
  conduct = 2
  density = 1
  expand = 3
  formula = G4_SILVER_CHLORIDE
  name = G4_SILVER_CHLORIDE
  specific = 4
FEATURE [App::DocumentObjectGroupPython] Br_element006  label="Br_element : 0.423"  # scripted group (container) (typed FeaturePython)
  n = 0.422895
FEATURE [App::DocumentObjectGroupPython] Ag_element004  label="Ag_element : 0.574"  # scripted group (container) (typed FeaturePython)
  n = 0.573748
FEATURE [App::DocumentObjectGroupPython] I_element007  label="I_element : 0.649"  # scripted group (container) (typed FeaturePython)
  n = 0.003357
FEATURE [App::DocumentObjectGroupPython] G4_SILVER_HALIDES  # scripted group (container) (typed FeaturePython)
  Dunit = g/cm3
  Dvalue = 6.47
  Group = -> [Br_element006,Ag_element004,I_element007]
  conduct = 2
  density = 1
  expand = 3
  formula = G4_SILVER_HALIDES
  name = G4_SILVER_HALIDES
  specific = 4
FEATURE [App::DocumentObjectGroupPython] Ag_element005  label="Ag_element : 003"  # scripted group (container) (typed FeaturePython)
  n = 1
  ref = Ag_element
FEATURE [App::DocumentObjectGroupPython] I_element008  label="I_element : 004"  # scripted group (container) (typed FeaturePython)
  n = 1
  ref = I_element
FEATURE [App::DocumentObjectGroupPython] G4_SILVER_IODIDE  # scripted group (container) (typed FeaturePython)
  Dunit = g/cm3
  Dvalue = 6.01
  Group = -> [Ag_element005,I_element008]
  conduct = 2
  density = 1
  expand = 3
  formula = G4_SILVER_IODIDE
  name = G4_SILVER_IODIDE
  specific = 4
FEATURE [App::DocumentObjectGroupPython] H_element095  label="H_element : 0.100"  # scripted group (container) (typed FeaturePython)
  n = 0.1
FEATURE [App::DocumentObjectGroupPython] C_element103  label="C_element : 0.204"  # scripted group (container) (typed FeaturePython)
  n = 0.204
FEATURE [App::DocumentObjectGroupPython] N_element039  label="N_element : 0.759"  # scripted group (container) (typed FeaturePython)
  n = 0.042
FEATURE [App::DocumentObjectGroupPython] O_element088  label="O_element : 0.645"  # scripted group (container) (typed FeaturePython)
  n = 0.645
FEATURE [App::DocumentObjectGroupPython] Na_element013  label="Na_element : 0.100"  # scripted group (container) (typed FeaturePython)
  n = 0.002
FEATURE [App::DocumentObjectGroupPython] P_element009  label="P_element : 0.107"  # scripted group (container) (typed FeaturePython)
  n = 0.001
FEATURE [App::DocumentObjectGroupPython] S_element020  label="S_element : 0.021"  # scripted group (container) (typed FeaturePython)
  n = 0.002
FEATURE [App::DocumentObjectGroupPython] Cl_element023  label="Cl_element : 0.590"  # scripted group (container) (typed FeaturePython)
  n = 0.003
FEATURE [App::DocumentObjectGroupPython] K_element010  label="K_element : 0.001"  # scripted group (container) (typed FeaturePython)
  n = 0.001
FEATURE [App::DocumentObjectGroupPython] G4_SKIN_ICRP  # scripted group (container) (typed FeaturePython)
  Dunit = g/cm3
  Dvalue = 1.09
  Group = -> [H_element095,C_element103,N_element039,O_element088,Na_element013,P_element009,S_element020,Cl_element023,K_element010]
  conduct = 2
  density = 1
  expand = 3
  formula = G4_SKIN_ICRP
  name = G4_SKIN_ICRP
  specific = 4
FEATURE [App::DocumentObjectGroupPython] Na_element014  label="Na_element : 2"  # scripted group (container) (typed FeaturePython)
  n = 2
  ref = Na_element
FEATURE [App::DocumentObjectGroupPython] C_element104  label="C_element : 058"  # scripted group (container) (typed FeaturePython)
  n = 1
  ref = C_element
FEATURE [App::DocumentObjectGroupPython] O_element089  label="O_element : 049"  # scripted group (container) (typed FeaturePython)
  n = 3
  ref = O_element
FEATURE [App::DocumentObjectGroupPython] G4_SODIUM_CARBONATE  # scripted group (container) (typed FeaturePython)
  Dunit = g/cm3
  Dvalue = 2.532
  Group = -> [Na_element014,C_element104,O_element089]
  conduct = 2
  density = 1
  expand = 3
  formula = G4_SODIUM_CARBONATE
  name = G4_SODIUM_CARBONATE
  specific = 4
FEATURE [App::DocumentObjectGroupPython] Na_element015  label="Na_element : 1"  # scripted group (container) (typed FeaturePython)
  n = 1
  ref = Na_element
FEATURE [App::DocumentObjectGroupPython] I_element009  label="I_element : 005"  # scripted group (container) (typed FeaturePython)
  n = 1
  ref = I_element
FEATURE [App::DocumentObjectGroupPython] G4_SODIUM_IODIDE  # scripted group (container) (typed FeaturePython)
  Dunit = g/cm3
  Dvalue = 3.667
  Group = -> [Na_element015,I_element009]
  conduct = 2
  density = 1
  expand = 3
  formula = G4_SODIUM_IODIDE
  name = G4_SODIUM_IODIDE
  specific = 4
FEATURE [App::DocumentObjectGroupPython] Na_element016  label="Na_element : 003"  # scripted group (container) (typed FeaturePython)
  n = 2
  ref = Na_element
FEATURE [App::DocumentObjectGroupPython] O_element090  label="O_element : 050"  # scripted group (container) (typed FeaturePython)
  n = 1
  ref = O_element
FEATURE [App::DocumentObjectGroupPython] G4_SODIUM_MONOXIDE  # scripted group (container) (typed FeaturePython)
  Dunit = g/cm3
  Dvalue = 2.27
  Group = -> [Na_element016,O_element090]
  conduct = 2
  density = 1
  expand = 3
  formula = G4_SODIUM_MONOXIDE
  name = G4_SODIUM_MONOXIDE
  specific = 4
FEATURE [App::DocumentObjectGroupPython] Na_element017  label="Na_element : 004"  # scripted group (container) (typed FeaturePython)
  n = 1
  ref = Na_element
FEATURE [App::DocumentObjectGroupPython] N_element040  label="N_element : 018"  # scripted group (container) (typed FeaturePython)
  n = 1
  ref = N_element
FEATURE [App::DocumentObjectGroupPython] O_element091  label="O_element : 051"  # scripted group (container) (typed FeaturePython)
  n = 3
  ref = O_element
FEATURE [App::DocumentObjectGroupPython] G4_SODIUM_NITRATE  # scripted group (container) (typed FeaturePython)
  Dunit = g/cm3
  Dvalue = 2.261
  Group = -> [Na_element017,N_element040,O_element091]
  conduct = 2
  density = 1
  expand = 3
  formula = G4_SODIUM_NITRATE
  name = G4_SODIUM_NITRATE
  specific = 4
FEATURE [App::DocumentObjectGroupPython] C_element105  label="C_element : 059"  # scripted group (container) (typed FeaturePython)
  n = 14
  ref = C_element
FEATURE [App::DocumentObjectGroupPython] H_element096  label="H_element : 053"  # scripted group (container) (typed FeaturePython)
  n = 12
  ref = H_element
FEATURE [App::DocumentObjectGroupPython] G4_STILBENE  # scripted group (container) (typed FeaturePython)
  Dunit = g/cm3
  Dvalue = 0.9707
  Group = -> [C_element105,H_element096]
  conduct = 2
  density = 1
  expand = 3
  formula = G4_STILBENE
  name = G4_STILBENE
  specific = 4
FEATURE [App::DocumentObjectGroupPython] C_element106  label="C_element : 12"  # scripted group (container) (typed FeaturePython)
  n = 12
  ref = C_element
FEATURE [App::DocumentObjectGroupPython] H_element097  label="H_element : 22"  # scripted group (container) (typed FeaturePython)
  n = 22
  ref = H_element
FEATURE [App::DocumentObjectGroupPython] O_element092  label="O_element : 11"  # scripted group (container) (typed FeaturePython)
  n = 11
  ref = O_element
FEATURE [App::DocumentObjectGroupPython] G4_SUCROSE  # scripted group (container) (typed FeaturePython)
  Dunit = g/cm3
  Dvalue = 1.5805
  Group = -> [C_element106,H_element097,O_element092]
  conduct = 2
  density = 1
  expand = 3
  formula = G4_SUCROSE
  name = G4_SUCROSE
  specific = 4
FEATURE [App::DocumentObjectGroupPython] C_element107  label="C_element : 18"  # scripted group (container) (typed FeaturePython)
  n = 18
  ref = C_element
FEATURE [App::DocumentObjectGroupPython] H_element098  label="H_element : 054"  # scripted group (container) (typed FeaturePython)
  n = 14
  ref = H_element
FEATURE [App::DocumentObjectGroupPython] G4_TERPHENYL  # scripted group (container) (typed FeaturePython)
  Dunit = g/cm3
  Dvalue = 1.24
  Group = -> [C_element107,H_element098]
  conduct = 2
  density = 1
  expand = 3
  formula = G4_TERPHENYL
  name = G4_TERPHENYL
  specific = 4
FEATURE [App::DocumentObjectGroupPython] H_element099  label="H_element : 0.146"  # scripted group (container) (typed FeaturePython)
  n = 0.106
FEATURE [App::DocumentObjectGroupPython] C_element108  label="C_element : 0.883"  # scripted group (container) (typed FeaturePython)
  n = 0.099
FEATURE [App::DocumentObjectGroupPython] N_element041  label="N_element : 0.020"  # scripted group (container) (typed FeaturePython)
  n = 0.02
FEATURE [App::DocumentObjectGroupPython] O_element093  label="O_element : 0.766"  # scripted group (container) (typed FeaturePython)
  n = 0.766
FEATURE [App::DocumentObjectGroupPython] Na_element018  label="Na_element : 0.101"  # scripted group (container) (typed FeaturePython)
  n = 0.002
FEATURE [App::DocumentObjectGroupPython] P_element010  label="P_element : 0.108"  # scripted group (container) (typed FeaturePython)
  n = 0.001
FEATURE [App::DocumentObjectGroupPython] S_element021  label="S_element : 0.022"  # scripted group (container) (typed FeaturePython)
  n = 0.002
FEATURE [App::DocumentObjectGroupPython] Cl_element024  label="Cl_element : 0.002"  # scripted group (container) (typed FeaturePython)
  n = 0.002
FEATURE [App::DocumentObjectGroupPython] K_element011  label="K_element : 0.017"  # scripted group (container) (typed FeaturePython)
  n = 0.002
FEATURE [App::DocumentObjectGroupPython] G4_TESTIS_ICRP  # scripted group (container) (typed FeaturePython)
  Dunit = g/cm3
  Dvalue = 1.04
  Group = -> [H_element099,C_element108,N_element041,O_element093,Na_element018,P_element010,S_element021,Cl_element024,K_element011]
  conduct = 2
  density = 1
  expand = 3
  formula = G4_TESTIS_ICRP
  name = G4_TESTIS_ICRP
  specific = 4
FEATURE [App::DocumentObjectGroupPython] C_element109  label="C_element : 060"  # scripted group (container) (typed FeaturePython)
  n = 2
  ref = C_element
FEATURE [App::DocumentObjectGroupPython] Cl_element025  label="Cl_element : 012"  # scripted group (container) (typed FeaturePython)
  n = 4
  ref = Cl_element
FEATURE [App::DocumentObjectGroupPython] G4_TETRACHLOROETHYLENE  # scripted group (container) (typed FeaturePython)
  Dunit = g/cm3
  Dvalue = 1.625
  Group = -> [C_element109,Cl_element025]
  conduct = 2
  density = 1
  expand = 3
  formula = G4_TETRACHLOROETHYLENE
  name = G4_TETRACHLOROETHYLENE
  specific = 4
FEATURE [App::DocumentObjectGroupPython] Tl_element001  label="Tl_element : 1"  # scripted group (container) (typed FeaturePython)
  n = 1
  ref = Tl_element
FEATURE [App::DocumentObjectGroupPython] Cl_element026  label="Cl_element : 013"  # scripted group (container) (typed FeaturePython)
  n = 1
  ref = Cl_element
FEATURE [App::DocumentObjectGroupPython] G4_THALLIUM_CHLORIDE  # scripted group (container) (typed FeaturePython)
  Dunit = g/cm3
  Dvalue = 7.004
  Group = -> [Tl_element001,Cl_element026]
  conduct = 2
  density = 1
  expand = 3
  formula = G4_THALLIUM_CHLORIDE
  name = G4_THALLIUM_CHLORIDE
  specific = 4
FEATURE [App::DocumentObjectGroupPython] H_element100  label="H_element : 0.147"  # scripted group (container) (typed FeaturePython)
  n = 0.105
FEATURE [App::DocumentObjectGroupPython] C_element110  label="C_element : 0.256"  # scripted group (container) (typed FeaturePython)
  n = 0.256
FEATURE [App::DocumentObjectGroupPython] N_element042  label="N_element : 0.760"  # scripted group (container) (typed FeaturePython)
  n = 0.027
FEATURE [App::DocumentObjectGroupPython] O_element094  label="O_element : 0.602"  # scripted group (container) (typed FeaturePython)
  n = 0.602
FEATURE [App::DocumentObjectGroupPython] Na_element019  label="Na_element : 0.102"  # scripted group (container) (typed FeaturePython)
  n = 0.001
FEATURE [App::DocumentObjectGroupPython] P_element011  label="P_element : 0.109"  # scripted group (container) (typed FeaturePython)
  n = 0.002
FEATURE [App::DocumentObjectGroupPython] S_element022  label="S_element : 0.023"  # scripted group (container) (typed FeaturePython)
  n = 0.003
FEATURE [App::DocumentObjectGroupPython] Cl_element027  label="Cl_element : 0.591"  # scripted group (container) (typed FeaturePython)
  n = 0.002
FEATURE [App::DocumentObjectGroupPython] K_element012  label="K_element : 0.018"  # scripted group (container) (typed FeaturePython)
  n = 0.002
FEATURE [App::DocumentObjectGroupPython] G4_TISSUE_SOFT_ICRP  # scripted group (container) (typed FeaturePython)
  Dunit = g/cm3
  Dvalue = 1.03
  Group = -> [H_element100,C_element110,N_element042,O_element094,Na_element019,P_element011,S_element022,Cl_element027,K_element012]
  conduct = 2
  density = 1
  expand = 3
  formula = G4_TISSUE_SOFT_ICRP
  name = G4_TISSUE_SOFT_ICRP
  specific = 4
FEATURE [App::DocumentObjectGroupPython] H_element101  label="H_element : 0.148"  # scripted group (container) (typed FeaturePython)
  n = 0.101
FEATURE [App::DocumentObjectGroupPython] C_element111  label="C_element : 0.111"  # scripted group (container) (typed FeaturePython)
  n = 0.111
FEATURE [App::DocumentObjectGroupPython] N_element043  label="N_element : 0.026"  # scripted group (container) (typed FeaturePython)
  n = 0.026
FEATURE [App::DocumentObjectGroupPython] O_element095  label="O_element : 0.762"  # scripted group (container) (typed FeaturePython)
  n = 0.762
FEATURE [App::DocumentObjectGroupPython] G4_TISSUE_SOFT_ICRU_4  label="G4_TISSUE_SOFT_ICRU-4"  # scripted group (container) (typed FeaturePython)
  Dunit = g/cm3
  Dvalue = 1
  Group = -> [H_element101,C_element111,N_element043,O_element095]
  conduct = 2
  density = 1
  expand = 3
  formula = G4_TISSUE_SOFT_ICRU-4
  name = G4_TISSUE_SOFT_ICRU-4
  specific = 4
FEATURE [App::DocumentObjectGroupPython] H_element102  label="H_element : 0.149"  # scripted group (container) (typed FeaturePython)
  n = 0.101869
FEATURE [App::DocumentObjectGroupPython] C_element112  label="C_element : 0.456"  # scripted group (container) (typed FeaturePython)
  n = 0.456179
FEATURE [App::DocumentObjectGroupPython] N_element044  label="N_element : 0.761"  # scripted group (container) (typed FeaturePython)
  n = 0.035172
FEATURE [App::DocumentObjectGroupPython] O_element096  label="O_element : 0.407"  # scripted group (container) (typed FeaturePython)
  n = 0.40678
FEATURE [App::DocumentObjectGroupPython] G4_TISSUE_METHANE  label="G4_TISSUE-METHANE"  # scripted group (container) (typed FeaturePython)
  Dunit = g/cm3
  Dvalue = 0.00106409
  Group = -> [H_element102,C_element112,N_element044,O_element096]
  conduct = 2
  density = 1
  expand = 3
  formula = G4_TISSUE-METHANE
  name = G4_TISSUE-METHANE
  specific = 4
FEATURE [App::DocumentObjectGroupPython] H_element103  label="H_element : 0.103"  # scripted group (container) (typed FeaturePython)
  n = 0.102672
FEATURE [App::DocumentObjectGroupPython] C_element113  label="C_element : 0.569"  # scripted group (container) (typed FeaturePython)
  n = 0.56894
FEATURE [App::DocumentObjectGroupPython] N_element045  label="N_element : 0.762"  # scripted group (container) (typed FeaturePython)
  n = 0.035022
FEATURE [App::DocumentObjectGroupPython] O_element097  label="O_element : 0.293"  # scripted group (container) (typed FeaturePython)
  n = 0.293366
FEATURE [App::DocumentObjectGroupPython] G4_TISSUE_PROPANE  label="G4_TISSUE-PROPANE"  # scripted group (container) (typed FeaturePython)
  Dunit = g/cm3
  Dvalue = 0.00182628
  Group = -> [H_element103,C_element113,N_element045,O_element097]
  conduct = 2
  density = 1
  expand = 3
  formula = G4_TISSUE-PROPANE
  name = G4_TISSUE-PROPANE
  specific = 4
FEATURE [App::DocumentObjectGroupPython] Ti_element003  label="Ti_element : 1"  # scripted group (container) (typed FeaturePython)
  n = 1
  ref = Ti_element
FEATURE [App::DocumentObjectGroupPython] O_element098  label="O_element : 052"  # scripted group (container) (typed FeaturePython)
  n = 2
  ref = O_element
FEATURE [App::DocumentObjectGroupPython] G4_TITANIUM_DIOXIDE  # scripted group (container) (typed FeaturePython)
  Dunit = g/cm3
  Dvalue = 4.26
  Group = -> [Ti_element003,O_element098]
  conduct = 2
  density = 1
  expand = 3
  formula = G4_TITANIUM_DIOXIDE
  name = G4_TITANIUM_DIOXIDE
  specific = 4
FEATURE [App::DocumentObjectGroupPython] C_element114  label="C_element : 061"  # scripted group (container) (typed FeaturePython)
  n = 7
  ref = C_element
FEATURE [App::DocumentObjectGroupPython] H_element104  label="H_element : 055"  # scripted group (container) (typed FeaturePython)
  n = 8
  ref = H_element
FEATURE [App::DocumentObjectGroupPython] G4_TOLUENE  # scripted group (container) (typed FeaturePython)
  Dunit = g/cm3
  Dvalue = 0.8669
  Group = -> [C_element114,H_element104]
  conduct = 2
  density = 1
  expand = 3
  formula = G4_TOLUENE
  name = G4_TOLUENE
  specific = 4
FEATURE [App::DocumentObjectGroupPython] C_element115  label="C_element : 062"  # scripted group (container) (typed FeaturePython)
  n = 2
  ref = C_element
FEATURE [App::DocumentObjectGroupPython] H_element105  label="H_element : 056"  # scripted group (container) (typed FeaturePython)
  n = 1
  ref = H_element
FEATURE [App::DocumentObjectGroupPython] Cl_element028  label="Cl_element : 014"  # scripted group (container) (typed FeaturePython)
  n = 3
  ref = Cl_element
FEATURE [App::DocumentObjectGroupPython] G4_TRICHLOROETHYLENE  # scripted group (container) (typed FeaturePython)
  Dunit = g/cm3
  Dvalue = 1.46
  Group = -> [C_element115,H_element105,Cl_element028]
  conduct = 2
  density = 1
  expand = 3
  formula = G4_TRICHLOROETHYLENE
  name = G4_TRICHLOROETHYLENE
  specific = 4
FEATURE [App::DocumentObjectGroupPython] C_element116  label="C_element : 063"  # scripted group (container) (typed FeaturePython)
  n = 6
  ref = C_element
FEATURE [App::DocumentObjectGroupPython] H_element106  label="H_element : 15"  # scripted group (container) (typed FeaturePython)
  n = 15
  ref = H_element
FEATURE [App::DocumentObjectGroupPython] O_element099  label="O_element : 053"  # scripted group (container) (typed FeaturePython)
  n = 4
  ref = O_element
FEATURE [App::DocumentObjectGroupPython] P_element012  label="P_element : 1"  # scripted group (container) (typed FeaturePython)
  n = 1
  ref = P_element
FEATURE [App::DocumentObjectGroupPython] G4_TRIETHYL_PHOSPHATE  # scripted group (container) (typed FeaturePython)
  Dunit = g/cm3
  Dvalue = 1.07
  Group = -> [C_element116,H_element106,O_element099,P_element012]
  conduct = 2
  density = 1
  expand = 3
  formula = G4_TRIETHYL_PHOSPHATE
  name = G4_TRIETHYL_PHOSPHATE
  specific = 4
FEATURE [App::DocumentObjectGroupPython] W_element003  label="W_element : 003"  # scripted group (container) (typed FeaturePython)
  n = 1
  ref = W_element
FEATURE [App::DocumentObjectGroupPython] F_element017  label="F_element : 6"  # scripted group (container) (typed FeaturePython)
  n = 6
  ref = F_element
FEATURE [App::DocumentObjectGroupPython] G4_TUNGSTEN_HEXAFLUORIDE  # scripted group (container) (typed FeaturePython)
  Dunit = g/cm3
  Dvalue = 2.4
  Group = -> [W_element003,F_element017]
  conduct = 2
  density = 1
  expand = 3
  formula = G4_TUNGSTEN_HEXAFLUORIDE
  name = G4_TUNGSTEN_HEXAFLUORIDE
  specific = 4
FEATURE [App::DocumentObjectGroupPython] U_element001  label="U_element : 1"  # scripted group (container) (typed FeaturePython)
  n = 1
  ref = U_element
FEATURE [App::DocumentObjectGroupPython] C_element117  label="C_element : 064"  # scripted group (container) (typed FeaturePython)
  n = 2
  ref = C_element
FEATURE [App::DocumentObjectGroupPython] G4_URANIUM_DICARBIDE  # scripted group (container) (typed FeaturePython)
  Dunit = g/cm3
  Dvalue = 11.28
  Group = -> [U_element001,C_element117]
  conduct = 2
  density = 1
  expand = 3
  formula = G4_URANIUM_DICARBIDE
  name = G4_URANIUM_DICARBIDE
  specific = 4
FEATURE [App::DocumentObjectGroupPython] U_element002  label="U_element : 002"  # scripted group (container) (typed FeaturePython)
  n = 1
  ref = U_element
FEATURE [App::DocumentObjectGroupPython] C_element118  label="C_element : 065"  # scripted group (container) (typed FeaturePython)
  n = 1
  ref = C_element
FEATURE [App::DocumentObjectGroupPython] G4_URANIUM_MONOCARBIDE  # scripted group (container) (typed FeaturePython)
  Dunit = g/cm3
  Dvalue = 13.63
  Group = -> [U_element002,C_element118]
  conduct = 2
  density = 1
  expand = 3
  formula = G4_URANIUM_MONOCARBIDE
  name = G4_URANIUM_MONOCARBIDE
  specific = 4
FEATURE [App::DocumentObjectGroupPython] U_element003  label="U_element : 003"  # scripted group (container) (typed FeaturePython)
  n = 1
  ref = U_element
FEATURE [App::DocumentObjectGroupPython] O_element100  label="O_element : 054"  # scripted group (container) (typed FeaturePython)
  n = 2
  ref = O_element
FEATURE [App::DocumentObjectGroupPython] G4_URANIUM_OXIDE  # scripted group (container) (typed FeaturePython)
  Dunit = g/cm3
  Dvalue = 10.96
  Group = -> [U_element003,O_element100]
  conduct = 2
  density = 1
  expand = 3
  formula = G4_URANIUM_OXIDE
  name = G4_URANIUM_OXIDE
  specific = 4
FEATURE [App::DocumentObjectGroupPython] C_element119  label="C_element : 066"  # scripted group (container) (typed FeaturePython)
  n = 1
  ref = C_element
FEATURE [App::DocumentObjectGroupPython] H_element107  label="H_element : 057"  # scripted group (container) (typed FeaturePython)
  n = 4
  ref = H_element
FEATURE [App::DocumentObjectGroupPython] N_element046  label="N_element : 019"  # scripted group (container) (typed FeaturePython)
  n = 2
  ref = N_element
FEATURE [App::DocumentObjectGroupPython] O_element101  label="O_element : 055"  # scripted group (container) (typed FeaturePython)
  n = 1
  ref = O_element
FEATURE [App::DocumentObjectGroupPython] G4_UREA  # scripted group (container) (typed FeaturePython)
  Dunit = g/cm3
  Dvalue = 1.323
  Group = -> [C_element119,H_element107,N_element046,O_element101]
  conduct = 2
  density = 1
  expand = 3
  formula = G4_UREA
  name = G4_UREA
  specific = 4
FEATURE [App::DocumentObjectGroupPython] C_element120  label="C_element : 067"  # scripted group (container) (typed FeaturePython)
  n = 5
  ref = C_element
FEATURE [App::DocumentObjectGroupPython] H_element108  label="H_element : 058"  # scripted group (container) (typed FeaturePython)
  n = 11
  ref = H_element
FEATURE [App::DocumentObjectGroupPython] N_element047  label="N_element : 020"  # scripted group (container) (typed FeaturePython)
  n = 1
  ref = N_element
FEATURE [App::DocumentObjectGroupPython] O_element102  label="O_element : 056"  # scripted group (container) (typed FeaturePython)
  n = 2
  ref = O_element
FEATURE [App::DocumentObjectGroupPython] G4_VALINE  # scripted group (container) (typed FeaturePython)
  Dunit = g/cm3
  Dvalue = 1.23
  Group = -> [C_element120,H_element108,N_element047,O_element102]
  conduct = 2
  density = 1
  expand = 3
  formula = G4_VALINE
  name = G4_VALINE
  specific = 4
FEATURE [App::DocumentObjectGroupPython] H_element109  label="H_element : 0.009"  # scripted group (container) (typed FeaturePython)
  n = 0.009417
FEATURE [App::DocumentObjectGroupPython] C_element121  label="C_element : 0.281"  # scripted group (container) (typed FeaturePython)
  n = 0.280555
FEATURE [App::DocumentObjectGroupPython] F_element018  label="F_element : 0.710"  # scripted group (container) (typed FeaturePython)
  n = 0.710028
FEATURE [App::DocumentObjectGroupPython] G4_VITON  # scripted group (container) (typed FeaturePython)
  Dunit = g/cm3
  Dvalue = 1.8
  Group = -> [H_element109,C_element121,F_element018]
  conduct = 2
  density = 1
  expand = 3
  formula = G4_VITON
  name = G4_VITON
  specific = 4
FEATURE [App::DocumentObjectGroupPython] H_element110  label="H_element : 059"  # scripted group (container) (typed FeaturePython)
  n = 2
  ref = H_element
FEATURE [App::DocumentObjectGroupPython] O_element103  label="O_element : 057"  # scripted group (container) (typed FeaturePython)
  n = 1
  ref = O_element
FEATURE [App::DocumentObjectGroupPython] G4_WATER  # scripted group (container) (typed FeaturePython)
  Dunit = g/cm3
  Dvalue = 1
  Group = -> [H_element110,O_element103]
  conduct = 2
  density = 1
  expand = 3
  formula = G4_WATER
  name = G4_WATER
  specific = 4
FEATURE [App::DocumentObjectGroupPython] H_element111  label="H_element : 060"  # scripted group (container) (typed FeaturePython)
  n = 2
  ref = H_element
FEATURE [App::DocumentObjectGroupPython] O_element104  label="O_element : 058"  # scripted group (container) (typed FeaturePython)
  n = 1
  ref = O_element
FEATURE [App::DocumentObjectGroupPython] G4_WATER_VAPOR  # scripted group (container) (typed FeaturePython)
  Dunit = g/cm3
  Dvalue = 0.000756182
  Group = -> [H_element111,O_element104]
  conduct = 2
  density = 1
  expand = 3
  formula = G4_WATER_VAPOR
  name = G4_WATER_VAPOR
  specific = 4
FEATURE [App::DocumentObjectGroupPython] C_element122  label="C_element : 068"  # scripted group (container) (typed FeaturePython)
  n = 8
  ref = C_element
FEATURE [App::DocumentObjectGroupPython] H_element112  label="H_element : 061"  # scripted group (container) (typed FeaturePython)
  n = 10
  ref = H_element
FEATURE [App::DocumentObjectGroupPython] G4_XYLENE  # scripted group (container) (typed FeaturePython)
  Dunit = g/cm3
  Dvalue = 0.87
  Group = -> [C_element122,H_element112]
  conduct = 2
  density = 1
  expand = 3
  formula = G4_XYLENE
  name = G4_XYLENE
  specific = 4
FEATURE [App::DocumentObjectGroupPython] C_element123  label="C_element : 069"  # scripted group (container) (typed FeaturePython)
  n = 1
  ref = C_element
FEATURE [App::DocumentObjectGroupPython] G4_GRAPHITE  # scripted group (container) (typed FeaturePython)
  Dunit = g/cm3
  Dvalue = 2.21
  Group = -> [C_element123]
  conduct = 2
  density = 1
  expand = 3
  formula = G4_GRAPHITE
  name = G4_GRAPHITE
  specific = 4
FEATURE [App::DocumentObjectGroupPython] NIST  # scripted group (container) (typed FeaturePython)
  Group = -> [G4_A_150_TISSUE,G4_ACETONE,G4_ACETYLENE,G4_ADENINE,G4_ADIPOSE_TISSUE_ICRP,G4_AIR,G4_ALANINE,G4_ALUMINUM_OXIDE,G4_AMBER,G4_AMMONIA,G4_ANILINE,G4_ANTHRACENE,G4_B_100_BONE,G4_BAKELITE,G4_BARIUM_FLUORIDE,G4_BARIUM_SULFATE,G4_BENZENE,G4_BERYLLIUM_OXIDE,G4_BGO,G4_BLOOD_ICRP,G4_BONE_COMPACT_ICRU,G4_BONE_CORTICAL_ICRP,G4_BORON_CARBIDE,G4_BORON_OXIDE,G4_BRAIN_ICRP,G4_BUTANE,G4_N_BUTYL_ALCOHOL,G4_C_552,+152 more]
FEATURE [App::DocumentObjectGroupPython] H_element113  label="H_element : 062"  # scripted group (container) (typed FeaturePython)
  n = 1
  ref = H_element
FEATURE [App::DocumentObjectGroupPython] G4_H  # scripted group (container) (typed FeaturePython)
  Dunit = g/cm3
  Dvalue = 8.3748e-05
  Group = -> [H_element113]
  conduct = 2
  density = 1
  expand = 3
  formula = H
  name = G4_H
  specific = 4
FEATURE [App::DocumentObjectGroupPython] He_element001  label="He_element : 1"  # scripted group (container) (typed FeaturePython)
  n = 1
  ref = He_element
FEATURE [App::DocumentObjectGroupPython] G4_He  # scripted group (container) (typed FeaturePython)
  Dunit = g/cm3
  Dvalue = 0.000166322
  Group = -> [He_element001]
  conduct = 2
  density = 1
  expand = 3
  formula = He
  name = G4_He
  specific = 4
FEATURE [App::DocumentObjectGroupPython] Li_element008  label="Li_element : 008"  # scripted group (container) (typed FeaturePython)
  n = 1
  ref = Li_element
FEATURE [App::DocumentObjectGroupPython] G4_Li  # scripted group (container) (typed FeaturePython)
  Dunit = g/cm3
  Dvalue = 0.534
  Group = -> [Li_element008]
  conduct = 2
  density = 1
  expand = 3
  formula = Li
  name = G4_Li
  specific = 4
FEATURE [App::DocumentObjectGroupPython] Be_element002  label="Be_element : 002"  # scripted group (container) (typed FeaturePython)
  n = 1
  ref = Be_element
FEATURE [App::DocumentObjectGroupPython] G4_Be  # scripted group (container) (typed FeaturePython)
  Dunit = g/cm3
  Dvalue = 1.848
  Group = -> [Be_element002]
  conduct = 2
  density = 1
  expand = 3
  formula = Be
  name = G4_Be
  specific = 4
FEATURE [App::DocumentObjectGroupPython] B_element007  label="B_element : 007"  # scripted group (container) (typed FeaturePython)
  n = 1
  ref = B_element
FEATURE [App::DocumentObjectGroupPython] G4_B  # scripted group (container) (typed FeaturePython)
  Dunit = g/cm3
  Dvalue = 2.37
  Group = -> [B_element007]
  conduct = 2
  density = 1
  expand = 3
  formula = B
  name = G4_B
  specific = 4
FEATURE [App::DocumentObjectGroupPython] C_element124  label="C_element : 070"  # scripted group (container) (typed FeaturePython)
  n = 1
  ref = C_element
FEATURE [App::DocumentObjectGroupPython] G4_C  # scripted group (container) (typed FeaturePython)
  Dunit = g/cm3
  Dvalue = 2
  Group = -> [C_element124]
  conduct = 2
  density = 1
  expand = 3
  formula = C
  name = G4_C
  specific = 4
FEATURE [App::DocumentObjectGroupPython] N_element048  label="N_element : 021"  # scripted group (container) (typed FeaturePython)
  n = 1
  ref = N_element
FEATURE [App::DocumentObjectGroupPython] G4_N  # scripted group (container) (typed FeaturePython)
  Dunit = g/cm3
  Dvalue = 0.0011652
  Group = -> [N_element048]
  conduct = 2
  density = 1
  expand = 3
  formula = N
  name = G4_N
  specific = 4
FEATURE [App::DocumentObjectGroupPython] O_element105  label="O_element : 059"  # scripted group (container) (typed FeaturePython)
  n = 1
  ref = O_element
FEATURE [App::DocumentObjectGroupPython] G4_O  # scripted group (container) (typed FeaturePython)
  Dunit = g/cm3
  Dvalue = 0.00133151
  Group = -> [O_element105]
  conduct = 2
  density = 1
  expand = 3
  formula = O
  name = G4_O
  specific = 4
FEATURE [App::DocumentObjectGroupPython] F_element019  label="F_element : 008"  # scripted group (container) (typed FeaturePython)
  n = 1
  ref = F_element
FEATURE [App::DocumentObjectGroupPython] G4_F  # scripted group (container) (typed FeaturePython)
  Dunit = g/cm3
  Dvalue = 0.00158029
  Group = -> [F_element019]
  conduct = 2
  density = 1
  expand = 3
  formula = F
  name = G4_F
  specific = 4
FEATURE [App::DocumentObjectGroupPython] Ne_element001  label="Ne_element : 1"  # scripted group (container) (typed FeaturePython)
  n = 1
  ref = Ne_element
FEATURE [App::DocumentObjectGroupPython] G4_Ne  # scripted group (container) (typed FeaturePython)
  Dunit = g/cm3
  Dvalue = 0.000838505
  Group = -> [Ne_element001]
  conduct = 2
  density = 1
  expand = 3
  formula = Ne
  name = G4_Ne
  specific = 4
FEATURE [App::DocumentObjectGroupPython] Na_element020  label="Na_element : 005"  # scripted group (container) (typed FeaturePython)
  n = 1
  ref = Na_element
FEATURE [App::DocumentObjectGroupPython] G4_Na  # scripted group (container) (typed FeaturePython)
  Dunit = g/cm3
  Dvalue = 0.971
  Group = -> [Na_element020]
  conduct = 2
  density = 1
  expand = 3
  formula = Na
  name = G4_Na
  specific = 4
FEATURE [App::DocumentObjectGroupPython] Mg_element011  label="Mg_element : 005"  # scripted group (container) (typed FeaturePython)
  n = 1
  ref = Mg_element
FEATURE [App::DocumentObjectGroupPython] G4_Mg  # scripted group (container) (typed FeaturePython)
  Dunit = g/cm3
  Dvalue = 1.74
  Group = -> [Mg_element011]
  conduct = 2
  density = 1
  expand = 3
  formula = Mg
  name = G4_Mg
  specific = 4
FEATURE [App::DocumentObjectGroupPython] Al_element004  label="Al_element : 1"  # scripted group (container) (typed FeaturePython)
  n = 1
  ref = Al_element
FEATURE [App::DocumentObjectGroupPython] G4_Al  # scripted group (container) (typed FeaturePython)
  Dunit = g/cm3
  Dvalue = 2.699
  Group = -> [Al_element004]
  conduct = 2
  density = 1
  expand = 3
  formula = Al
  name = G4_Al
  specific = 4
FEATURE [App::DocumentObjectGroupPython] Si_element007  label="Si_element : 002"  # scripted group (container) (typed FeaturePython)
  n = 1
  ref = Si_element
FEATURE [App::DocumentObjectGroupPython] G4_Si  # scripted group (container) (typed FeaturePython)
  Dunit = g/cm3
  Dvalue = 2.33
  Group = -> [Si_element007]
  conduct = 2
  density = 1
  expand = 3
  formula = Si
  name = G4_Si
  specific = 4
FEATURE [App::DocumentObjectGroupPython] P_element013  label="P_element : 002"  # scripted group (container) (typed FeaturePython)
  n = 1
  ref = P_element
FEATURE [App::DocumentObjectGroupPython] G4_P  # scripted group (container) (typed FeaturePython)
  Dunit = g/cm3
  Dvalue = 2.2
  Group = -> [P_element013]
  conduct = 2
  density = 1
  expand = 3
  formula = P
  name = G4_P
  specific = 4
FEATURE [App::DocumentObjectGroupPython] S_element023  label="S_element : 007"  # scripted group (container) (typed FeaturePython)
  n = 1
  ref = S_element
FEATURE [App::DocumentObjectGroupPython] G4_S  # scripted group (container) (typed FeaturePython)
  Dunit = g/cm3
  Dvalue = 2
  Group = -> [S_element023]
  conduct = 2
  density = 1
  expand = 3
  formula = S
  name = G4_S
  specific = 4
FEATURE [App::DocumentObjectGroupPython] Cl_element029  label="Cl_element : 015"  # scripted group (container) (typed FeaturePython)
  n = 1
  ref = Cl_element
FEATURE [App::DocumentObjectGroupPython] G4_Cl  # scripted group (container) (typed FeaturePython)
  Dunit = g/cm3
  Dvalue = 0.00299473
  Group = -> [Cl_element029]
  conduct = 2
  density = 1
  expand = 3
  formula = Cl
  name = G4_Cl
  specific = 4
FEATURE [App::DocumentObjectGroupPython] Ar_element002  label="Ar_element : 1"  # scripted group (container) (typed FeaturePython)
  n = 1
  ref = Ar_element
FEATURE [App::DocumentObjectGroupPython] G4_Ar  # scripted group (container) (typed FeaturePython)
  Dunit = g/cm3
  Dvalue = 0.00166201
  Group = -> [Ar_element002]
  conduct = 2
  density = 1
  expand = 3
  formula = Ar
  name = G4_Ar
  specific = 4
FEATURE [App::DocumentObjectGroupPython] K_element013  label="K_element : 003"  # scripted group (container) (typed FeaturePython)
  n = 1
  ref = K_element
FEATURE [App::DocumentObjectGroupPython] G4_K  # scripted group (container) (typed FeaturePython)
  Dunit = g/cm3
  Dvalue = 0.862
  Group = -> [K_element013]
  conduct = 2
  density = 1
  expand = 3
  formula = K
  name = G4_K
  specific = 4
FEATURE [App::DocumentObjectGroupPython] Ca_element014  label="Ca_element : 007"  # scripted group (container) (typed FeaturePython)
  n = 1
  ref = Ca_element
FEATURE [App::DocumentObjectGroupPython] G4_Ca  # scripted group (container) (typed FeaturePython)
  Dunit = g/cm3
  Dvalue = 1.55
  Group = -> [Ca_element014]
  conduct = 2
  density = 1
  expand = 3
  formula = Ca
  name = G4_Ca
  specific = 4
FEATURE [App::DocumentObjectGroupPython] Sc_element001  label="Sc_element : 1"  # scripted group (container) (typed FeaturePython)
  n = 1
  ref = Sc_element
FEATURE [App::DocumentObjectGroupPython] G4_Sc  # scripted group (container) (typed FeaturePython)
  Dunit = g/cm3
  Dvalue = 2.989
  Group = -> [Sc_element001]
  conduct = 2
  density = 1
  expand = 3
  formula = Sc
  name = G4_Sc
  specific = 4
FEATURE [App::DocumentObjectGroupPython] Ti_element004  label="Ti_element : 002"  # scripted group (container) (typed FeaturePython)
  n = 1
  ref = Ti_element
FEATURE [App::DocumentObjectGroupPython] G4_Ti  # scripted group (container) (typed FeaturePython)
  Dunit = g/cm3
  Dvalue = 4.54
  Group = -> [Ti_element004]
  conduct = 2
  density = 1
  expand = 3
  formula = Ti
  name = G4_Ti
  specific = 4
FEATURE [App::DocumentObjectGroupPython] V_element001  label="V_element : 1"  # scripted group (container) (typed FeaturePython)
  n = 1
  ref = V_element
FEATURE [App::DocumentObjectGroupPython] G4_V  # scripted group (container) (typed FeaturePython)
  Dunit = g/cm3
  Dvalue = 6.11
  Group = -> [V_element001]
  conduct = 2
  density = 1
  expand = 3
  formula = V
  name = G4_V
  specific = 4
FEATURE [App::DocumentObjectGroupPython] Cr_element001  label="Cr_element : 1"  # scripted group (container) (typed FeaturePython)
  n = 1
  ref = Cr_element
FEATURE [App::DocumentObjectGroupPython] G4_Cr  # scripted group (container) (typed FeaturePython)
  Dunit = g/cm3
  Dvalue = 7.18
  Group = -> [Cr_element001]
  conduct = 2
  density = 1
  expand = 3
  formula = Cr
  name = G4_Cr
  specific = 4
FEATURE [App::DocumentObjectGroupPython] Mn_element001  label="Mn_element : 1"  # scripted group (container) (typed FeaturePython)
  n = 1
  ref = Mn_element
FEATURE [App::DocumentObjectGroupPython] G4_Mn  # scripted group (container) (typed FeaturePython)
  Dunit = g/cm3
  Dvalue = 7.44
  Group = -> [Mn_element001]
  conduct = 2
  density = 1
  expand = 3
  formula = Mn
  name = G4_Mn
  specific = 4
FEATURE [App::DocumentObjectGroupPython] Fe_element007  label="Fe_element : 004"  # scripted group (container) (typed FeaturePython)
  n = 1
  ref = Fe_element
FEATURE [App::DocumentObjectGroupPython] G4_Fe  # scripted group (container) (typed FeaturePython)
  Dunit = g/cm3
  Dvalue = 7.874
  Group = -> [Fe_element007]
  conduct = 2
  density = 1
  expand = 3
  formula = Fe
  name = G4_Fe
  specific = 4
FEATURE [App::DocumentObjectGroupPython] Co_element001  label="Co_element : 1"  # scripted group (container) (typed FeaturePython)
  n = 1
  ref = Co_element
FEATURE [App::DocumentObjectGroupPython] G4_Co  # scripted group (container) (typed FeaturePython)
  Dunit = g/cm3
  Dvalue = 8.9
  Group = -> [Co_element001]
  conduct = 2
  density = 1
  expand = 3
  formula = Co
  name = G4_Co
  specific = 4
FEATURE [App::DocumentObjectGroupPython] Ni_element001  label="Ni_element : 1"  # scripted group (container) (typed FeaturePython)
  n = 1
  ref = Ni_element
FEATURE [App::DocumentObjectGroupPython] G4_Ni  # scripted group (container) (typed FeaturePython)
  Dunit = g/cm3
  Dvalue = 8.902
  Group = -> [Ni_element001]
  conduct = 2
  density = 1
  expand = 3
  formula = Ni
  name = G4_Ni
  specific = 4
FEATURE [App::DocumentObjectGroupPython] Cu_element001  label="Cu_element : 1"  # scripted group (container) (typed FeaturePython)
  n = 1
  ref = Cu_element
FEATURE [App::DocumentObjectGroupPython] G4_Cu  # scripted group (container) (typed FeaturePython)
  Dunit = g/cm3
  Dvalue = 8.96
  Group = -> [Cu_element001]
  conduct = 2
  density = 1
  expand = 3
  formula = Cu
  name = G4_Cu
  specific = 4
FEATURE [App::DocumentObjectGroupPython] Zn_element001  label="Zn_element : 1"  # scripted group (container) (typed FeaturePython)
  n = 1
  ref = Zn_element
FEATURE [App::DocumentObjectGroupPython] G4_Zn  # scripted group (container) (typed FeaturePython)
  Dunit = g/cm3
  Dvalue = 7.133
  Group = -> [Zn_element001]
  conduct = 2
  density = 1
  expand = 3
  formula = Zn
  name = G4_Zn
  specific = 4
FEATURE [App::DocumentObjectGroupPython] Ga_element002  label="Ga_element : 002"  # scripted group (container) (typed FeaturePython)
  n = 1
  ref = Ga_element
FEATURE [App::DocumentObjectGroupPython] G4_Ga  # scripted group (container) (typed FeaturePython)
  Dunit = g/cm3
  Dvalue = 5.904
  Group = -> [Ga_element002]
  conduct = 2
  density = 1
  expand = 3
  formula = Ga
  name = G4_Ga
  specific = 4
FEATURE [App::DocumentObjectGroupPython] Ge_element002  label="Ge_element : 1"  # scripted group (container) (typed FeaturePython)
  n = 1
  ref = Ge_element
FEATURE [App::DocumentObjectGroupPython] G4_Ge  # scripted group (container) (typed FeaturePython)
  Dunit = g/cm3
  Dvalue = 5.323
  Group = -> [Ge_element002]
  conduct = 2
  density = 1
  expand = 3
  formula = Ge
  name = G4_Ge
  specific = 4
FEATURE [App::DocumentObjectGroupPython] As_element003  label="As_element : 002"  # scripted group (container) (typed FeaturePython)
  n = 1
  ref = As_element
FEATURE [App::DocumentObjectGroupPython] G4_As  # scripted group (container) (typed FeaturePython)
  Dunit = g/cm3
  Dvalue = 5.73
  Group = -> [As_element003]
  conduct = 2
  density = 1
  expand = 3
  formula = As
  name = G4_As
  specific = 4
FEATURE [App::DocumentObjectGroupPython] Se_element001  label="Se_element : 1"  # scripted group (container) (typed FeaturePython)
  n = 1
  ref = Se_element
FEATURE [App::DocumentObjectGroupPython] G4_Se  # scripted group (container) (typed FeaturePython)
  Dunit = g/cm3
  Dvalue = 4.5
  Group = -> [Se_element001]
  conduct = 2
  density = 1
  expand = 3
  formula = Se
  name = G4_Se
  specific = 4
FEATURE [App::DocumentObjectGroupPython] Br_element007  label="Br_element : 004"  # scripted group (container) (typed FeaturePython)
  n = 1
  ref = Br_element
FEATURE [App::DocumentObjectGroupPython] G4_Br  # scripted group (container) (typed FeaturePython)
  Dunit = g/cm3
  Dvalue = 0.0070721
  Group = -> [Br_element007]
  conduct = 2
  density = 1
  expand = 3
  formula = Br
  name = G4_Br
  specific = 4
FEATURE [App::DocumentObjectGroupPython] Kr_element001  label="Kr_element : 1"  # scripted group (container) (typed FeaturePython)
  n = 1
  ref = Kr_element
FEATURE [App::DocumentObjectGroupPython] G4_Kr  # scripted group (container) (typed FeaturePython)
  Dunit = g/cm3
  Dvalue = 0.00347832
  Group = -> [Kr_element001]
  conduct = 2
  density = 1
  expand = 3
  formula = Kr
  name = G4_Kr
  specific = 4
FEATURE [App::DocumentObjectGroupPython] Rb_element001  label="Rb_element : 1"  # scripted group (container) (typed FeaturePython)
  n = 1
  ref = Rb_element
FEATURE [App::DocumentObjectGroupPython] G4_Rb  # scripted group (container) (typed FeaturePython)
  Dunit = g/cm3
  Dvalue = 1.532
  Group = -> [Rb_element001]
  conduct = 2
  density = 1
  expand = 3
  formula = Rb
  name = G4_Rb
  specific = 4
FEATURE [App::DocumentObjectGroupPython] Sr_element001  label="Sr_element : 1"  # scripted group (container) (typed FeaturePython)
  n = 1
  ref = Sr_element
FEATURE [App::DocumentObjectGroupPython] G4_Sr  # scripted group (container) (typed FeaturePython)
  Dunit = g/cm3
  Dvalue = 2.54
  Group = -> [Sr_element001]
  conduct = 2
  density = 1
  expand = 3
  formula = Sr
  name = G4_Sr
  specific = 4
FEATURE [App::DocumentObjectGroupPython] Y_element001  label="Y_element : 1"  # scripted group (container) (typed FeaturePython)
  n = 1
  ref = Y_element
FEATURE [App::DocumentObjectGroupPython] G4_Y  # scripted group (container) (typed FeaturePython)
  Dunit = g/cm3
  Dvalue = 4.469
  Group = -> [Y_element001]
  conduct = 2
  density = 1
  expand = 3
  formula = Y
  name = G4_Y
  specific = 4
FEATURE [App::DocumentObjectGroupPython] Zr_element001  label="Zr_element : 1"  # scripted group (container) (typed FeaturePython)
  n = 1
  ref = Zr_element
FEATURE [App::DocumentObjectGroupPython] G4_Zr  # scripted group (container) (typed FeaturePython)
  Dunit = g/cm3
  Dvalue = 6.506
  Group = -> [Zr_element001]
  conduct = 2
  density = 1
  expand = 3
  formula = Zr
  name = G4_Zr
  specific = 4
FEATURE [App::DocumentObjectGroupPython] Nb_element001  label="Nb_element : 1"  # scripted group (container) (typed FeaturePython)
  n = 1
  ref = Nb_element
FEATURE [App::DocumentObjectGroupPython] G4_Nb  # scripted group (container) (typed FeaturePython)
  Dunit = g/cm3
  Dvalue = 8.57
  Group = -> [Nb_element001]
  conduct = 2
  density = 1
  expand = 3
  formula = Nb
  name = G4_Nb
  specific = 4
FEATURE [App::DocumentObjectGroupPython] Mo_element001  label="Mo_element : 1"  # scripted group (container) (typed FeaturePython)
  n = 1
  ref = Mo_element
FEATURE [App::DocumentObjectGroupPython] G4_Mo  # scripted group (container) (typed FeaturePython)
  Dunit = g/cm3
  Dvalue = 10.22
  Group = -> [Mo_element001]
  conduct = 2
  density = 1
  expand = 3
  formula = Mo
  name = G4_Mo
  specific = 4
FEATURE [App::DocumentObjectGroupPython] Tc_element001  label="Tc_element : 1"  # scripted group (container) (typed FeaturePython)
  n = 1
  ref = Tc_element
FEATURE [App::DocumentObjectGroupPython] G4_Tc  # scripted group (container) (typed FeaturePython)
  Dunit = g/cm3
  Dvalue = 11.5
  Group = -> [Tc_element001]
  conduct = 2
  density = 1
  expand = 3
  formula = Tc
  name = G4_Tc
  specific = 4
FEATURE [App::DocumentObjectGroupPython] Ru_element001  label="Ru_element : 1"  # scripted group (container) (typed FeaturePython)
  n = 1
  ref = Ru_element
FEATURE [App::DocumentObjectGroupPython] G4_Ru  # scripted group (container) (typed FeaturePython)
  Dunit = g/cm3
  Dvalue = 12.41
  Group = -> [Ru_element001]
  conduct = 2
  density = 1
  expand = 3
  formula = Ru
  name = G4_Ru
  specific = 4
FEATURE [App::DocumentObjectGroupPython] Rh_element001  label="Rh_element : 1"  # scripted group (container) (typed FeaturePython)
  n = 1
  ref = Rh_element
FEATURE [App::DocumentObjectGroupPython] G4_Rh  # scripted group (container) (typed FeaturePython)
  Dunit = g/cm3
  Dvalue = 12.41
  Group = -> [Rh_element001]
  conduct = 2
  density = 1
  expand = 3
  formula = Rh
  name = G4_Rh
  specific = 4
FEATURE [App::DocumentObjectGroupPython] Pd_element001  label="Pd_element : 1"  # scripted group (container) (typed FeaturePython)
  n = 1
  ref = Pd_element
FEATURE [App::DocumentObjectGroupPython] G4_Pd  # scripted group (container) (typed FeaturePython)
  Dunit = g/cm3
  Dvalue = 12.02
  Group = -> [Pd_element001]
  conduct = 2
  density = 1
  expand = 3
  formula = Pd
  name = G4_Pd
  specific = 4
FEATURE [App::DocumentObjectGroupPython] Ag_element006  label="Ag_element : 004"  # scripted group (container) (typed FeaturePython)
  n = 1
  ref = Ag_element
FEATURE [App::DocumentObjectGroupPython] G4_Ag  # scripted group (container) (typed FeaturePython)
  Dunit = g/cm3
  Dvalue = 10.5
  Group = -> [Ag_element006]
  conduct = 2
  density = 1
  expand = 3
  formula = Ag
  name = G4_Ag
  specific = 4
FEATURE [App::DocumentObjectGroupPython] Cd_element003  label="Cd_element : 003"  # scripted group (container) (typed FeaturePython)
  n = 1
  ref = Cd_element
FEATURE [App::DocumentObjectGroupPython] G4_Cd  # scripted group (container) (typed FeaturePython)
  Dunit = g/cm3
  Dvalue = 8.65
  Group = -> [Cd_element003]
  conduct = 2
  density = 1
  expand = 3
  formula = Cd
  name = G4_Cd
  specific = 4
FEATURE [App::DocumentObjectGroupPython] In_element001  label="In_element : 1"  # scripted group (container) (typed FeaturePython)
  n = 1
  ref = In_element
FEATURE [App::DocumentObjectGroupPython] G4_In  # scripted group (container) (typed FeaturePython)
  Dunit = g/cm3
  Dvalue = 7.31
  Group = -> [In_element001]
  conduct = 2
  density = 1
  expand = 3
  formula = In
  name = G4_In
  specific = 4
FEATURE [App::DocumentObjectGroupPython] Sn_element001  label="Sn_element : 1"  # scripted group (container) (typed FeaturePython)
  n = 1
  ref = Sn_element
FEATURE [App::DocumentObjectGroupPython] G4_Sn  # scripted group (container) (typed FeaturePython)
  Dunit = g/cm3
  Dvalue = 7.31
  Group = -> [Sn_element001]
  conduct = 2
  density = 1
  expand = 3
  formula = Sn
  name = G4_Sn
  specific = 4
FEATURE [App::DocumentObjectGroupPython] Sb_element001  label="Sb_element : 1"  # scripted group (container) (typed FeaturePython)
  n = 1
  ref = Sb_element
FEATURE [App::DocumentObjectGroupPython] G4_Sb  # scripted group (container) (typed FeaturePython)
  Dunit = g/cm3
  Dvalue = 6.691
  Group = -> [Sb_element001]
  conduct = 2
  density = 1
  expand = 3
  formula = Sb
  name = G4_Sb
  specific = 4
FEATURE [App::DocumentObjectGroupPython] Te_element002  label="Te_element : 002"  # scripted group (container) (typed FeaturePython)
  n = 1
  ref = Te_element
FEATURE [App::DocumentObjectGroupPython] G4_Te  # scripted group (container) (typed FeaturePython)
  Dunit = g/cm3
  Dvalue = 6.24
  Group = -> [Te_element002]
  conduct = 2
  density = 1
  expand = 3
  formula = Te
  name = G4_Te
  specific = 4
FEATURE [App::DocumentObjectGroupPython] I_element010  label="I_element : 006"  # scripted group (container) (typed FeaturePython)
  n = 1
  ref = I_element
FEATURE [App::DocumentObjectGroupPython] G4_I  # scripted group (container) (typed FeaturePython)
  Dunit = g/cm3
  Dvalue = 4.93
  Group = -> [I_element010]
  conduct = 2
  density = 1
  expand = 3
  formula = I
  name = G4_I
  specific = 4
FEATURE [App::DocumentObjectGroupPython] Xe_element001  label="Xe_element : 1"  # scripted group (container) (typed FeaturePython)
  n = 1
  ref = Xe_element
FEATURE [App::DocumentObjectGroupPython] G4_Xe  # scripted group (container) (typed FeaturePython)
  Dunit = g/cm3
  Dvalue = 0.00548536
  Group = -> [Xe_element001]
  conduct = 2
  density = 1
  expand = 3
  formula = Xe
  name = G4_Xe
  specific = 4
FEATURE [App::DocumentObjectGroupPython] Cs_element003  label="Cs_element : 003"  # scripted group (container) (typed FeaturePython)
  n = 1
  ref = Cs_element
FEATURE [App::DocumentObjectGroupPython] G4_Cs  # scripted group (container) (typed FeaturePython)
  Dunit = g/cm3
  Dvalue = 1.873
  Group = -> [Cs_element003]
  conduct = 2
  density = 1
  expand = 3
  formula = Cs
  name = G4_Cs
  specific = 4
FEATURE [App::DocumentObjectGroupPython] Ba_element003  label="Ba_element : 003"  # scripted group (container) (typed FeaturePython)
  n = 1
  ref = Ba_element
FEATURE [App::DocumentObjectGroupPython] G4_Ba  # scripted group (container) (typed FeaturePython)
  Dunit = g/cm3
  Dvalue = 3.5
  Group = -> [Ba_element003]
  conduct = 2
  density = 1
  expand = 3
  formula = Ba
  name = G4_Ba
  specific = 4
FEATURE [App::DocumentObjectGroupPython] La_element003  label="La_element : 003"  # scripted group (container) (typed FeaturePython)
  n = 1
  ref = La_element
FEATURE [App::DocumentObjectGroupPython] G4_La  # scripted group (container) (typed FeaturePython)
  Dunit = g/cm3
  Dvalue = 6.154
  Group = -> [La_element003]
  conduct = 2
  density = 1
  expand = 3
  formula = La
  name = G4_La
  specific = 4
FEATURE [App::DocumentObjectGroupPython] Ce_element002  label="Ce_element : 1"  # scripted group (container) (typed FeaturePython)
  n = 1
  ref = Ce_element
FEATURE [App::DocumentObjectGroupPython] G4_Ce  # scripted group (container) (typed FeaturePython)
  Dunit = g/cm3
  Dvalue = 6.657
  Group = -> [Ce_element002]
  conduct = 2
  density = 1
  expand = 3
  formula = Ce
  name = G4_Ce
  specific = 4
FEATURE [App::DocumentObjectGroupPython] Pr_element001  label="Pr_element : 1"  # scripted group (container) (typed FeaturePython)
  n = 1
  ref = Pr_element
FEATURE [App::DocumentObjectGroupPython] G4_Pr  # scripted group (container) (typed FeaturePython)
  Dunit = g/cm3
  Dvalue = 6.71
  Group = -> [Pr_element001]
  conduct = 2
  density = 1
  expand = 3
  formula = Pr
  name = G4_Pr
  specific = 4
FEATURE [App::DocumentObjectGroupPython] Nd_element001  label="Nd_element : 1"  # scripted group (container) (typed FeaturePython)
  n = 1
  ref = Nd_element
FEATURE [App::DocumentObjectGroupPython] G4_Nd  # scripted group (container) (typed FeaturePython)
  Dunit = g/cm3
  Dvalue = 6.9
  Group = -> [Nd_element001]
  conduct = 2
  density = 1
  expand = 3
  formula = Nd
  name = G4_Nd
  specific = 4
FEATURE [App::DocumentObjectGroupPython] Pm_element001  label="Pm_element : 1"  # scripted group (container) (typed FeaturePython)
  n = 1
  ref = Pm_element
FEATURE [App::DocumentObjectGroupPython] G4_Pm  # scripted group (container) (typed FeaturePython)
  Dunit = g/cm3
  Dvalue = 7.22
  Group = -> [Pm_element001]
  conduct = 2
  density = 1
  expand = 3
  formula = Pm
  name = G4_Pm
  specific = 4
FEATURE [App::DocumentObjectGroupPython] Sm_element001  label="Sm_element : 1"  # scripted group (container) (typed FeaturePython)
  n = 1
  ref = Sm_element
FEATURE [App::DocumentObjectGroupPython] G4_Sm  # scripted group (container) (typed FeaturePython)
  Dunit = g/cm3
  Dvalue = 7.46
  Group = -> [Sm_element001]
  conduct = 2
  density = 1
  expand = 3
  formula = Sm
  name = G4_Sm
  specific = 4
FEATURE [App::DocumentObjectGroupPython] Eu_element001  label="Eu_element : 1"  # scripted group (container) (typed FeaturePython)
  n = 1
  ref = Eu_element
FEATURE [App::DocumentObjectGroupPython] G4_Eu  # scripted group (container) (typed FeaturePython)
  Dunit = g/cm3
  Dvalue = 5.243
  Group = -> [Eu_element001]
  conduct = 2
  density = 1
  expand = 3
  formula = Eu
  name = G4_Eu
  specific = 4
FEATURE [App::DocumentObjectGroupPython] Gd_element002  label="Gd_element : 1"  # scripted group (container) (typed FeaturePython)
  n = 1
  ref = Gd_element
FEATURE [App::DocumentObjectGroupPython] G4_Gd  # scripted group (container) (typed FeaturePython)
  Dunit = g/cm3
  Dvalue = 7.9004
  Group = -> [Gd_element002]
  conduct = 2
  density = 1
  expand = 3
  formula = Gd
  name = G4_Gd
  specific = 4
FEATURE [App::DocumentObjectGroupPython] Tb_element001  label="Tb_element : 1"  # scripted group (container) (typed FeaturePython)
  n = 1
  ref = Tb_element
FEATURE [App::DocumentObjectGroupPython] G4_Tb  # scripted group (container) (typed FeaturePython)
  Dunit = g/cm3
  Dvalue = 8.229
  Group = -> [Tb_element001]
  conduct = 2
  density = 1
  expand = 3
  formula = Tb
  name = G4_Tb
  specific = 4
FEATURE [App::DocumentObjectGroupPython] Dy_element001  label="Dy_element : 1"  # scripted group (container) (typed FeaturePython)
  n = 1
  ref = Dy_element
FEATURE [App::DocumentObjectGroupPython] G4_Dy  # scripted group (container) (typed FeaturePython)
  Dunit = g/cm3
  Dvalue = 8.55
  Group = -> [Dy_element001]
  conduct = 2
  density = 1
  expand = 3
  formula = Dy
  name = G4_Dy
  specific = 4
FEATURE [App::DocumentObjectGroupPython] Ho_element001  label="Ho_element : 1"  # scripted group (container) (typed FeaturePython)
  n = 1
  ref = Ho_element
FEATURE [App::DocumentObjectGroupPython] G4_Ho  # scripted group (container) (typed FeaturePython)
  Dunit = g/cm3
  Dvalue = 8.795
  Group = -> [Ho_element001]
  conduct = 2
  density = 1
  expand = 3
  formula = Ho
  name = G4_Ho
  specific = 4
FEATURE [App::DocumentObjectGroupPython] Er_element001  label="Er_element : 1"  # scripted group (container) (typed FeaturePython)
  n = 1
  ref = Er_element
FEATURE [App::DocumentObjectGroupPython] G4_Er  # scripted group (container) (typed FeaturePython)
  Dunit = g/cm3
  Dvalue = 9.066
  Group = -> [Er_element001]
  conduct = 2
  density = 1
  expand = 3
  formula = Er
  name = G4_Er
  specific = 4
FEATURE [App::DocumentObjectGroupPython] Tm_element001  label="Tm_element : 1"  # scripted group (container) (typed FeaturePython)
  n = 1
  ref = Tm_element
FEATURE [App::DocumentObjectGroupPython] G4_Tm  # scripted group (container) (typed FeaturePython)
  Dunit = g/cm3
  Dvalue = 9.321
  Group = -> [Tm_element001]
  conduct = 2
  density = 1
  expand = 3
  formula = Tm
  name = G4_Tm
  specific = 4
FEATURE [App::DocumentObjectGroupPython] Yb_element001  label="Yb_element : 1"  # scripted group (container) (typed FeaturePython)
  n = 1
  ref = Yb_element
FEATURE [App::DocumentObjectGroupPython] G4_Yb  # scripted group (container) (typed FeaturePython)
  Dunit = g/cm3
  Dvalue = 6.73
  Group = -> [Yb_element001]
  conduct = 2
  density = 1
  expand = 3
  formula = Yb
  name = G4_Yb
  specific = 4
FEATURE [App::DocumentObjectGroupPython] Lu_element001  label="Lu_element : 1"  # scripted group (container) (typed FeaturePython)
  n = 1
  ref = Lu_element
FEATURE [App::DocumentObjectGroupPython] G4_Lu  # scripted group (container) (typed FeaturePython)
  Dunit = g/cm3
  Dvalue = 9.84
  Group = -> [Lu_element001]
  conduct = 2
  density = 1
  expand = 3
  formula = Lu
  name = G4_Lu
  specific = 4
FEATURE [App::DocumentObjectGroupPython] Hf_element001  label="Hf_element : 1"  # scripted group (container) (typed FeaturePython)
  n = 1
  ref = Hf_element
FEATURE [App::DocumentObjectGroupPython] G4_Hf  # scripted group (container) (typed FeaturePython)
  Dunit = g/cm3
  Dvalue = 13.31
  Group = -> [Hf_element001]
  conduct = 2
  density = 1
  expand = 3
  formula = Hf
  name = G4_Hf
  specific = 4
FEATURE [App::DocumentObjectGroupPython] Ta_element001  label="Ta_element : 1"  # scripted group (container) (typed FeaturePython)
  n = 1
  ref = Ta_element
FEATURE [App::DocumentObjectGroupPython] G4_Ta  # scripted group (container) (typed FeaturePython)
  Dunit = g/cm3
  Dvalue = 16.654
  Group = -> [Ta_element001]
  conduct = 2
  density = 1
  expand = 3
  formula = Ta
  name = G4_Ta
  specific = 4
FEATURE [App::DocumentObjectGroupPython] W_element004  label="W_element : 004"  # scripted group (container) (typed FeaturePython)
  n = 1
  ref = W_element
FEATURE [App::DocumentObjectGroupPython] G4_W  # scripted group (container) (typed FeaturePython)
  Dunit = g/cm3
  Dvalue = 19.3
  Group = -> [W_element004]
  conduct = 2
  density = 1
  expand = 3
  formula = W
  name = G4_W
  specific = 4
FEATURE [App::DocumentObjectGroupPython] Re_element001  label="Re_element : 1"  # scripted group (container) (typed FeaturePython)
  n = 1
  ref = Re_element
FEATURE [App::DocumentObjectGroupPython] G4_Re  # scripted group (container) (typed FeaturePython)
  Dunit = g/cm3
  Dvalue = 21.02
  Group = -> [Re_element001]
  conduct = 2
  density = 1
  expand = 3
  formula = Re
  name = G4_Re
  specific = 4
FEATURE [App::DocumentObjectGroupPython] Os_element001  label="Os_element : 1"  # scripted group (container) (typed FeaturePython)
  n = 1
  ref = Os_element
FEATURE [App::DocumentObjectGroupPython] G4_Os  # scripted group (container) (typed FeaturePython)
  Dunit = g/cm3
  Dvalue = 22.57
  Group = -> [Os_element001]
  conduct = 2
  density = 1
  expand = 3
  formula = Os
  name = G4_Os
  specific = 4
FEATURE [App::DocumentObjectGroupPython] Ir_element001  label="Ir_element : 1"  # scripted group (container) (typed FeaturePython)
  n = 1
  ref = Ir_element
FEATURE [App::DocumentObjectGroupPython] G4_Ir  # scripted group (container) (typed FeaturePython)
  Dunit = g/cm3
  Dvalue = 22.42
  Group = -> [Ir_element001]
  conduct = 2
  density = 1
  expand = 3
  formula = Ir
  name = G4_Ir
  specific = 4
FEATURE [App::DocumentObjectGroupPython] Pt_element001  label="Pt_element : 1"  # scripted group (container) (typed FeaturePython)
  n = 1
  ref = Pt_element
FEATURE [App::DocumentObjectGroupPython] G4_Pt  # scripted group (container) (typed FeaturePython)
  Dunit = g/cm3
  Dvalue = 21.45
  Group = -> [Pt_element001]
  conduct = 2
  density = 1
  expand = 3
  formula = Pt
  name = G4_Pt
  specific = 4
FEATURE [App::DocumentObjectGroupPython] Au_element001  label="Au_element : 1"  # scripted group (container) (typed FeaturePython)
  n = 1
  ref = Au_element
FEATURE [App::DocumentObjectGroupPython] G4_Au  # scripted group (container) (typed FeaturePython)
  Dunit = g/cm3
  Dvalue = 19.32
  Group = -> [Au_element001]
  conduct = 2
  density = 1
  expand = 3
  formula = Au
  name = G4_Au
  specific = 4
FEATURE [App::DocumentObjectGroupPython] Hg_element002  label="Hg_element : 002"  # scripted group (container) (typed FeaturePython)
  n = 1
  ref = Hg_element
FEATURE [App::DocumentObjectGroupPython] G4_Hg  # scripted group (container) (typed FeaturePython)
  Dunit = g/cm3
  Dvalue = 13.546
  Group = -> [Hg_element002]
  conduct = 2
  density = 1
  expand = 3
  formula = Hg
  name = G4_Hg
  specific = 4
FEATURE [App::DocumentObjectGroupPython] Tl_element002  label="Tl_element : 002"  # scripted group (container) (typed FeaturePython)
  n = 1
  ref = Tl_element
FEATURE [App::DocumentObjectGroupPython] G4_Tl  # scripted group (container) (typed FeaturePython)
  Dunit = g/cm3
  Dvalue = 11.72
  Group = -> [Tl_element002]
  conduct = 2
  density = 1
  expand = 3
  formula = Tl
  name = G4_Tl
  specific = 4
FEATURE [App::DocumentObjectGroupPython] Pb_element003  label="Pb_element : 1"  # scripted group (container) (typed FeaturePython)
  n = 1
  ref = Pb_element
FEATURE [App::DocumentObjectGroupPython] G4_Pb  # scripted group (container) (typed FeaturePython)
  Dunit = g/cm3
  Dvalue = 11.35
  Group = -> [Pb_element003]
  conduct = 2
  density = 1
  expand = 3
  formula = Pb
  name = G4_Pb
  specific = 4
FEATURE [App::DocumentObjectGroupPython] Bi_element002  label="Bi_element : 1"  # scripted group (container) (typed FeaturePython)
  n = 1
  ref = Bi_element
FEATURE [App::DocumentObjectGroupPython] G4_Bi  # scripted group (container) (typed FeaturePython)
  Dunit = g/cm3
  Dvalue = 9.747
  Group = -> [Bi_element002]
  conduct = 2
  density = 1
  expand = 3
  formula = Bi
  name = G4_Bi
  specific = 4
FEATURE [App::DocumentObjectGroupPython] Po_element001  label="Po_element : 1"  # scripted group (container) (typed FeaturePython)
  n = 1
  ref = Po_element
FEATURE [App::DocumentObjectGroupPython] G4_Po  # scripted group (container) (typed FeaturePython)
  Dunit = g/cm3
  Dvalue = 9.32
  Group = -> [Po_element001]
  conduct = 2
  density = 1
  expand = 3
  formula = Po
  name = G4_Po
  specific = 4
FEATURE [App::DocumentObjectGroupPython] At_element001  label="At_element : 1"  # scripted group (container) (typed FeaturePython)
  n = 1
  ref = At_element
FEATURE [App::DocumentObjectGroupPython] G4_At  # scripted group (container) (typed FeaturePython)
  Dunit = g/cm3
  Dvalue = 9.32
  Group = -> [At_element001]
  conduct = 2
  density = 1
  expand = 3
  formula = At
  name = G4_At
  specific = 4
FEATURE [App::DocumentObjectGroupPython] Rn_element001  label="Rn_element : 1"  # scripted group (container) (typed FeaturePython)
  n = 1
  ref = Rn_element
FEATURE [App::DocumentObjectGroupPython] G4_Rn  # scripted group (container) (typed FeaturePython)
  Dunit = g/cm3
  Dvalue = 0.00900662
  Group = -> [Rn_element001]
  conduct = 2
  density = 1
  expand = 3
  formula = Rn
  name = G4_Rn
  specific = 4
FEATURE [App::DocumentObjectGroupPython] Fr_element001  label="Fr_element : 1"  # scripted group (container) (typed FeaturePython)
  n = 1
  ref = Fr_element
FEATURE [App::DocumentObjectGroupPython] G4_Fr  # scripted group (container) (typed FeaturePython)
  Dunit = g/cm3
  Dvalue = 1
  Group = -> [Fr_element001]
  conduct = 2
  density = 1
  expand = 3
  formula = Fr
  name = G4_Fr
  specific = 4
FEATURE [App::DocumentObjectGroupPython] Ra_element001  label="Ra_element : 1"  # scripted group (container) (typed FeaturePython)
  n = 1
  ref = Ra_element
FEATURE [App::DocumentObjectGroupPython] G4_Ra  # scripted group (container) (typed FeaturePython)
  Dunit = g/cm3
  Dvalue = 5
  Group = -> [Ra_element001]
  conduct = 2
  density = 1
  expand = 3
  formula = Ra
  name = G4_Ra
  specific = 4
FEATURE [App::DocumentObjectGroupPython] Ac_element001  label="Ac_element : 1"  # scripted group (container) (typed FeaturePython)
  n = 1
  ref = Ac_element
FEATURE [App::DocumentObjectGroupPython] G4_Ac  # scripted group (container) (typed FeaturePython)
  Dunit = g/cm3
  Dvalue = 10.07
  Group = -> [Ac_element001]
  conduct = 2
  density = 1
  expand = 3
  formula = Ac
  name = G4_Ac
  specific = 4
FEATURE [App::DocumentObjectGroupPython] Th_element001  label="Th_element : 1"  # scripted group (container) (typed FeaturePython)
  n = 1
  ref = Th_element
FEATURE [App::DocumentObjectGroupPython] G4_Th  # scripted group (container) (typed FeaturePython)
  Dunit = g/cm3
  Dvalue = 11.72
  Group = -> [Th_element001]
  conduct = 2
  density = 1
  expand = 3
  formula = Th
  name = G4_Th
  specific = 4
FEATURE [App::DocumentObjectGroupPython] Pa_element001  label="Pa_element : 1"  # scripted group (container) (typed FeaturePython)
  n = 1
  ref = Pa_element
FEATURE [App::DocumentObjectGroupPython] G4_Pa  # scripted group (container) (typed FeaturePython)
  Dunit = g/cm3
  Dvalue = 15.37
  Group = -> [Pa_element001]
  conduct = 2
  density = 1
  expand = 3
  formula = Pa
  name = G4_Pa
  specific = 4
FEATURE [App::DocumentObjectGroupPython] U_element004  label="U_element : 004"  # scripted group (container) (typed FeaturePython)
  n = 1
  ref = U_element
FEATURE [App::DocumentObjectGroupPython] G4_U  # scripted group (container) (typed FeaturePython)
  Dunit = g/cm3
  Dvalue = 18.95
  Group = -> [U_element004]
  conduct = 2
  density = 1
  expand = 3
  formula = U
  name = G4_U
  specific = 4
FEATURE [App::DocumentObjectGroupPython] Np_element001  label="Np_element : 1"  # scripted group (container) (typed FeaturePython)
  n = 1
  ref = Np_element
FEATURE [App::DocumentObjectGroupPython] G4_Np  # scripted group (container) (typed FeaturePython)
  Dunit = g/cm3
  Dvalue = 20.25
  Group = -> [Np_element001]
  conduct = 2
  density = 1
  expand = 3
  formula = Np
  name = G4_Np
  specific = 4
FEATURE [App::DocumentObjectGroupPython] Pu_element002  label="Pu_element : 002"  # scripted group (container) (typed FeaturePython)
  n = 1
  ref = Pu_element
FEATURE [App::DocumentObjectGroupPython] G4_Pu  # scripted group (container) (typed FeaturePython)
  Dunit = g/cm3
  Dvalue = 19.84
  Group = -> [Pu_element002]
  conduct = 2
  density = 1
  expand = 3
  formula = Pu
  name = G4_Pu
  specific = 4
FEATURE [App::DocumentObjectGroupPython] Am_element001  label="Am_element : 1"  # scripted group (container) (typed FeaturePython)
  n = 1
  ref = Am_element
FEATURE [App::DocumentObjectGroupPython] G4_Am  # scripted group (container) (typed FeaturePython)
  Dunit = g/cm3
  Dvalue = 13.67
  Group = -> [Am_element001]
  conduct = 2
  density = 1
  expand = 3
  formula = Am
  name = G4_Am
  specific = 4
FEATURE [App::DocumentObjectGroupPython] Cm_element001  label="Cm_element : 1"  # scripted group (container) (typed FeaturePython)
  n = 1
  ref = Cm_element
FEATURE [App::DocumentObjectGroupPython] G4_Cm  # scripted group (container) (typed FeaturePython)
  Dunit = g/cm3
  Dvalue = 13.51
  Group = -> [Cm_element001]
  conduct = 2
  density = 1
  expand = 3
  formula = Cm
  name = G4_Cm
  specific = 4
FEATURE [App::DocumentObjectGroupPython] Bk_element001  label="Bk_element : 1"  # scripted group (container) (typed FeaturePython)
  n = 1
  ref = Bk_element
FEATURE [App::DocumentObjectGroupPython] G4_Bk  # scripted group (container) (typed FeaturePython)
  Dunit = g/cm3
  Dvalue = 14
  Group = -> [Bk_element001]
  conduct = 2
  density = 1
  expand = 3
  formula = Bk
  name = G4_Bk
  specific = 4
FEATURE [App::DocumentObjectGroupPython] Cf_element001  label="Cf_element : 1"  # scripted group (container) (typed FeaturePython)
  n = 1
  ref = Cf_element
FEATURE [App::DocumentObjectGroupPython] G4_Cf  # scripted group (container) (typed FeaturePython)
  Dunit = g/cm3
  Dvalue = 10
  Group = -> [Cf_element001]
  conduct = 2
  density = 1
  expand = 3
  formula = Cf
  name = G4_Cf
  specific = 4
FEATURE [App::DocumentObjectGroupPython] Element  # scripted group (container) (typed FeaturePython)
  Group = -> [G4_H,G4_He,G4_Li,G4_Be,G4_B,G4_C,G4_N,G4_O,G4_F,G4_Ne,G4_Na,G4_Mg,G4_Al,G4_Si,G4_P,G4_S,G4_Cl,G4_Ar,G4_K,G4_Ca,G4_Sc,G4_Ti,G4_V,G4_Cr,G4_Mn,G4_Fe,G4_Co,G4_Ni,G4_Cu,G4_Zn,G4_Ga,G4_Ge,G4_As,G4_Se,G4_Br,G4_Kr,G4_Rb,G4_Sr,G4_Y,G4_Zr,G4_Nb,G4_Mo,G4_Tc,G4_Ru,G4_Rh,G4_Pd,G4_Ag,G4_Cd,G4_In,G4_Sn,G4_Sb,G4_Te,G4_I,G4_Xe,G4_Cs,G4_Ba,G4_La,G4_Ce,G4_Pr,G4_Nd,G4_Pm,G4_Sm,G4_Eu,G4_Gd,G4_Tb,G4_Dy,G4_Ho,G4_Er,+30 more]
FEATURE [App::DocumentObjectGroupPython] H_element114  label="H_element : 063"  # scripted group (container) (typed FeaturePython)
  n = 2
  ref = H_element
FEATURE [App::DocumentObjectGroupPython] G4_lH2  # scripted group (container) (typed FeaturePython)
  Dunit = g/cm3
  Dvalue = 0.0708
  Group = -> [H_element114]
  conduct = 2
  density = 1
  expand = 3
  formula = G4_lH2
  name = G4_lH2
  specific = 4
FEATURE [App::DocumentObjectGroupPython] N_element049  label="N_element : 022"  # scripted group (container) (typed FeaturePython)
  n = 2
  ref = N_element
FEATURE [App::DocumentObjectGroupPython] G4_lN2  # scripted group (container) (typed FeaturePython)
  Dunit = g/cm3
  Dvalue = 0.807
  Group = -> [N_element049]
  conduct = 2
  density = 1
  expand = 3
  formula = G4_lN2
  name = G4_lN2
  specific = 4
FEATURE [App::DocumentObjectGroupPython] O_element106  label="O_element : 060"  # scripted group (container) (typed FeaturePython)
  n = 2
  ref = O_element
FEATURE [App::DocumentObjectGroupPython] G4_lO2  # scripted group (container) (typed FeaturePython)
  Dunit = g/cm3
  Dvalue = 1.141
  Group = -> [O_element106]
  conduct = 2
  density = 1
  expand = 3
  formula = G4_lO2
  name = G4_lO2
  specific = 4
FEATURE [App::DocumentObjectGroupPython] Ar  label="Ar : 1"  # scripted group (container) (typed FeaturePython)
  n = 1
  ref = Ar
FEATURE [App::DocumentObjectGroupPython] G4_lAr  # scripted group (container) (typed FeaturePython)
  Dunit = g/cm3
  Dvalue = 1.396
  Group = -> [Ar]
  conduct = 2
  density = 1
  expand = 3
  formula = G4_lAr
  name = G4_lAr
  specific = 4
FEATURE [App::DocumentObjectGroupPython] Br  label="Br : 1"  # scripted group (container) (typed FeaturePython)
  n = 1
  ref = Br
FEATURE [App::DocumentObjectGroupPython] G4_lBr  # scripted group (container) (typed FeaturePython)
  Dunit = g/cm3
  Dvalue = 3.1028
  Group = -> [Br]
  conduct = 2
  density = 1
  expand = 3
  formula = G4_lBr
  name = G4_lBr
  specific = 4
FEATURE [App::DocumentObjectGroupPython] Kr  label="Kr : 1"  # scripted group (container) (typed FeaturePython)
  n = 1
  ref = Kr
FEATURE [App::DocumentObjectGroupPython] G4_lKr  # scripted group (container) (typed FeaturePython)
  Dunit = g/cm3
  Dvalue = 2.418
  Group = -> [Kr]
  conduct = 2
  density = 1
  expand = 3
  formula = G4_lKr
  name = G4_lKr
  specific = 4
FEATURE [App::DocumentObjectGroupPython] Xe  label="Xe : 1"  # scripted group (container) (typed FeaturePython)
  n = 1
  ref = Xe
FEATURE [App::DocumentObjectGroupPython] G4_lXe  # scripted group (container) (typed FeaturePython)
  Dunit = g/cm3
  Dvalue = 2.953
  Group = -> [Xe]
  conduct = 2
  density = 1
  expand = 3
  formula = G4_lXe
  name = G4_lXe
  specific = 4
FEATURE [App::DocumentObjectGroupPython] O_element107  label="O_element : 061"  # scripted group (container) (typed FeaturePython)
  n = 4
  ref = O_element
FEATURE [App::DocumentObjectGroupPython] Pb_element004  label="Pb_element : 002"  # scripted group (container) (typed FeaturePython)
  n = 1
  ref = Pb_element
FEATURE [App::DocumentObjectGroupPython] W_element005  label="W_element : 005"  # scripted group (container) (typed FeaturePython)
  n = 1
  ref = W_element
FEATURE [App::DocumentObjectGroupPython] G4_PbWO4  # scripted group (container) (typed FeaturePython)
  Dunit = g/cm3
  Dvalue = 8.28
  Group = -> [O_element107,Pb_element004,W_element005]
  conduct = 2
  density = 1
  expand = 3
  formula = G4_PbWO4
  name = G4_PbWO4
  specific = 4
FEATURE [App::DocumentObjectGroupPython] alactic  label="alactic : 1"  # scripted group (container) (typed FeaturePython)
  n = 1
  ref = alactic
FEATURE [App::DocumentObjectGroupPython] G4_Galactic  # scripted group (container) (typed FeaturePython)
  Dunit = g/cm3
  Dvalue = 0
  Group = -> [alactic]
  conduct = 2
  density = 1
  expand = 3
  formula = G4_Galactic
  name = G4_Galactic
  specific = 4
FEATURE [App::DocumentObjectGroupPython] RAPHITE_POROUS  label="RAPHITE_POROUS : 1"  # scripted group (container) (typed FeaturePython)
  n = 1
  ref = RAPHITE_POROUS
FEATURE [App::DocumentObjectGroupPython] G4_GRAPHITE_POROUS  # scripted group (container) (typed FeaturePython)
  Dunit = g/cm3
  Dvalue = 1.7
  Group = -> [RAPHITE_POROUS]
  conduct = 2
  density = 1
  expand = 3
  formula = G4_GRAPHITE_POROUS
  name = G4_GRAPHITE_POROUS
  specific = 4
FEATURE [App::DocumentObjectGroupPython] H_element115  label="H_element : 0.150"  # scripted group (container) (typed FeaturePython)
  n = 0.080538
FEATURE [App::DocumentObjectGroupPython] C_element125  label="C_element : 0.600"  # scripted group (container) (typed FeaturePython)
  n = 0.599848
FEATURE [App::DocumentObjectGroupPython] O_element108  label="O_element : 0.320"  # scripted group (container) (typed FeaturePython)
  n = 0.319614
FEATURE [App::DocumentObjectGroupPython] G4_LUCITE  # scripted group (container) (typed FeaturePython)
  Dunit = g/cm3
  Dvalue = 1.19
  Group = -> [H_element115,C_element125,O_element108]
  conduct = 2
  density = 1
  expand = 3
  formula = G4_LUCITE
  name = G4_LUCITE
  specific = 4
FEATURE [App::DocumentObjectGroupPython] Cu_element002  label="Cu_element : 62"  # scripted group (container) (typed FeaturePython)
  n = 62
  ref = Cu_element
FEATURE [App::DocumentObjectGroupPython] Zn_element002  label="Zn_element : 35"  # scripted group (container) (typed FeaturePython)
  n = 35
  ref = Zn_element
FEATURE [App::DocumentObjectGroupPython] Pb_element005  label="Pb_element : 3"  # scripted group (container) (typed FeaturePython)
  n = 3
  ref = Pb_element
FEATURE [App::DocumentObjectGroupPython] G4_BRASS  # scripted group (container) (typed FeaturePython)
  Dunit = g/cm3
  Dvalue = 8.52
  Group = -> [Cu_element002,Zn_element002,Pb_element005]
  conduct = 2
  density = 1
  expand = 3
  formula = G4_BRASS
  name = G4_BRASS
  specific = 4
FEATURE [App::DocumentObjectGroupPython] Cu_element003  label="Cu_element : 89"  # scripted group (container) (typed FeaturePython)
  n = 89
  ref = Cu_element
FEATURE [App::DocumentObjectGroupPython] Zn_element003  label="Zn_element : 9"  # scripted group (container) (typed FeaturePython)
  n = 9
  ref = Zn_element
FEATURE [App::DocumentObjectGroupPython] Pb_element006  label="Pb_element : 2"  # scripted group (container) (typed FeaturePython)
  n = 2
  ref = Pb_element
FEATURE [App::DocumentObjectGroupPython] G4_BRONZE  # scripted group (container) (typed FeaturePython)
  Dunit = g/cm3
  Dvalue = 8.82
  Group = -> [Cu_element003,Zn_element003,Pb_element006]
  conduct = 2
  density = 1
  expand = 3
  formula = G4_BRONZE
  name = G4_BRONZE
  specific = 4
FEATURE [App::DocumentObjectGroupPython] Fe_element008  label="Fe_element : 74"  # scripted group (container) (typed FeaturePython)
  n = 74
  ref = Fe_element
FEATURE [App::DocumentObjectGroupPython] Cr_element002  label="Cr_element : 18"  # scripted group (container) (typed FeaturePython)
  n = 18
  ref = Cr_element
FEATURE [App::DocumentObjectGroupPython] Ni_element002  label="Ni_element : 8"  # scripted group (container) (typed FeaturePython)
  n = 8
  ref = Ni_element
FEATURE [App::DocumentObjectGroupPython] G4_STAINLESS_STEEL  label="G4_STAINLESS-STEEL"  # scripted group (container) (typed FeaturePython)
  Dunit = g/cm3
  Dvalue = 8
  Group = -> [Fe_element008,Cr_element002,Ni_element002]
  conduct = 2
  density = 1
  expand = 3
  formula = G4_STAINLESS-STEEL
  name = G4_STAINLESS-STEEL
  specific = 4
FEATURE [App::DocumentObjectGroupPython] H_element116  label="H_element : 064"  # scripted group (container) (typed FeaturePython)
  n = 18
  ref = H_element
FEATURE [App::DocumentObjectGroupPython] C_element126  label="C_element : 071"  # scripted group (container) (typed FeaturePython)
  n = 12
  ref = C_element
FEATURE [App::DocumentObjectGroupPython] O_element109  label="O_element : 062"  # scripted group (container) (typed FeaturePython)
  n = 7
  ref = O_element
FEATURE [App::DocumentObjectGroupPython] G4_CR39  # scripted group (container) (typed FeaturePython)
  Dunit = g/cm3
  Dvalue = 1.32
  Group = -> [H_element116,C_element126,O_element109]
  conduct = 2
  density = 1
  expand = 3
  formula = G4_CR39
  name = G4_CR39
  specific = 4
FEATURE [App::DocumentObjectGroupPython] H_element117  label="H_element : 38"  # scripted group (container) (typed FeaturePython)
  n = 38
  ref = H_element
FEATURE [App::DocumentObjectGroupPython] C_element127  label="C_element : 072"  # scripted group (container) (typed FeaturePython)
  n = 18
  ref = C_element
FEATURE [App::DocumentObjectGroupPython] O_element110  label="O_element : 063"  # scripted group (container) (typed FeaturePython)
  n = 1
  ref = O_element
FEATURE [App::DocumentObjectGroupPython] G4_OCTADECANOL  # scripted group (container) (typed FeaturePython)
  Dunit = g/cm3
  Dvalue = 0.812
  Group = -> [H_element117,C_element127,O_element110]
  conduct = 2
  density = 1
  expand = 3
  formula = G4_OCTADECANOL
  name = G4_OCTADECANOL
  specific = 4
FEATURE [App::DocumentObjectGroupPython] HEP  # scripted group (container) (typed FeaturePython)
  Group = -> [G4_lH2,G4_lN2,G4_lO2,G4_lAr,G4_lBr,G4_lKr,G4_lXe,G4_PbWO4,G4_Galactic,G4_GRAPHITE_POROUS,G4_LUCITE,G4_BRASS,G4_BRONZE,G4_STAINLESS_STEEL,G4_CR39,G4_OCTADECANOL]
FEATURE [App::DocumentObjectGroupPython] C_element128  label="C_element : 073"  # scripted group (container) (typed FeaturePython)
  n = 14
  ref = C_element
FEATURE [App::DocumentObjectGroupPython] H_element118  label="H_element : 065"  # scripted group (container) (typed FeaturePython)
  n = 10
  ref = H_element
FEATURE [App::DocumentObjectGroupPython] O_element111  label="O_element : 064"  # scripted group (container) (typed FeaturePython)
  n = 2
  ref = O_element
FEATURE [App::DocumentObjectGroupPython] N_element050  label="N_element : 023"  # scripted group (container) (typed FeaturePython)
  n = 2
  ref = N_element
FEATURE [App::DocumentObjectGroupPython] G4_KEVLAR  # scripted group (container) (typed FeaturePython)
  Dunit = g/cm3
  Dvalue = 1.44
  Group = -> [C_element128,H_element118,O_element111,N_element050]
  conduct = 2
  density = 1
  expand = 3
  formula = G4_KEVLAR
  name = G4_KEVLAR
  specific = 4
FEATURE [App::DocumentObjectGroupPython] C_element129  label="C_element : 074"  # scripted group (container) (typed FeaturePython)
  n = 10
  ref = C_element
FEATURE [App::DocumentObjectGroupPython] H_element119  label="H_element : 066"  # scripted group (container) (typed FeaturePython)
  n = 8
  ref = H_element
FEATURE [App::DocumentObjectGroupPython] O_element112  label="O_element : 065"  # scripted group (container) (typed FeaturePython)
  n = 4
  ref = O_element
FEATURE [App::DocumentObjectGroupPython] G4_DACRON  # scripted group (container) (typed FeaturePython)
  Dunit = g/cm3
  Dvalue = 1.4
  Group = -> [C_element129,H_element119,O_element112]
  conduct = 2
  density = 1
  expand = 3
  formula = G4_DACRON
  name = G4_DACRON
  specific = 4
FEATURE [App::DocumentObjectGroupPython] C_element130  label="C_element : 075"  # scripted group (container) (typed FeaturePython)
  n = 4
  ref = C_element
FEATURE [App::DocumentObjectGroupPython] H_element120  label="H_element : 067"  # scripted group (container) (typed FeaturePython)
  n = 5
  ref = H_element
FEATURE [App::DocumentObjectGroupPython] Cl_element030  label="Cl_element : 016"  # scripted group (container) (typed FeaturePython)
  n = 1
  ref = Cl_element
FEATURE [App::DocumentObjectGroupPython] G4_NEOPRENE  # scripted group (container) (typed FeaturePython)
  Dunit = g/cm3
  Dvalue = 1.23
  Group = -> [C_element130,H_element120,Cl_element030]
  conduct = 2
  density = 1
  expand = 3
  formula = G4_NEOPRENE
  name = G4_NEOPRENE
  specific = 4
FEATURE [App::DocumentObjectGroupPython] Space  # scripted group (container) (typed FeaturePython)
  Group = -> [G4_KEVLAR,G4_DACRON,G4_NEOPRENE]
FEATURE [App::DocumentObjectGroupPython] H_element121  label="H_element : 068"  # scripted group (container) (typed FeaturePython)
  n = 5
  ref = H_element
FEATURE [App::DocumentObjectGroupPython] C_element131  label="C_element : 076"  # scripted group (container) (typed FeaturePython)
  n = 4
  ref = C_element
FEATURE [App::DocumentObjectGroupPython] N_element051  label="N_element : 3"  # scripted group (container) (typed FeaturePython)
  n = 3
  ref = N_element
FEATURE [App::DocumentObjectGroupPython] O_element113  label="O_element : 066"  # scripted group (container) (typed FeaturePython)
  n = 1
  ref = O_element
FEATURE [App::DocumentObjectGroupPython] G4_CYTOSINE  # scripted group (container) (typed FeaturePython)
  Dunit = g/cm3
  Dvalue = 1.55
  Group = -> [H_element121,C_element131,N_element051,O_element113]
  conduct = 2
  density = 1
  expand = 3
  formula = G4_CYTOSINE
  name = G4_CYTOSINE
  specific = 4
FEATURE [App::DocumentObjectGroupPython] H_element122  label="H_element : 069"  # scripted group (container) (typed FeaturePython)
  n = 6
  ref = H_element
FEATURE [App::DocumentObjectGroupPython] C_element132  label="C_element : 077"  # scripted group (container) (typed FeaturePython)
  n = 5
  ref = C_element
FEATURE [App::DocumentObjectGroupPython] N_element052  label="N_element : 024"  # scripted group (container) (typed FeaturePython)
  n = 2
  ref = N_element
FEATURE [App::DocumentObjectGroupPython] O_element114  label="O_element : 067"  # scripted group (container) (typed FeaturePython)
  n = 2
  ref = O_element
FEATURE [App::DocumentObjectGroupPython] G4_THYMINE  # scripted group (container) (typed FeaturePython)
  Dunit = g/cm3
  Dvalue = 1.23
  Group = -> [H_element122,C_element132,N_element052,O_element114]
  conduct = 2
  density = 1
  expand = 3
  formula = G4_THYMINE
  name = G4_THYMINE
  specific = 4
FEATURE [App::DocumentObjectGroupPython] H_element123  label="H_element : 070"  # scripted group (container) (typed FeaturePython)
  n = 4
  ref = H_element
FEATURE [App::DocumentObjectGroupPython] C_element133  label="C_element : 078"  # scripted group (container) (typed FeaturePython)
  n = 4
  ref = C_element
FEATURE [App::DocumentObjectGroupPython] N_element053  label="N_element : 025"  # scripted group (container) (typed FeaturePython)
  n = 2
  ref = N_element
FEATURE [App::DocumentObjectGroupPython] O_element115  label="O_element : 068"  # scripted group (container) (typed FeaturePython)
  n = 2
  ref = O_element
FEATURE [App::DocumentObjectGroupPython] G4_URACIL  # scripted group (container) (typed FeaturePython)
  Dunit = g/cm3
  Dvalue = 1.32
  Group = -> [H_element123,C_element133,N_element053,O_element115]
  conduct = 2
  density = 1
  expand = 3
  formula = G4_URACIL
  name = G4_URACIL
  specific = 4
FEATURE [App::DocumentObjectGroupPython] H_element124  label="H_element : 071"  # scripted group (container) (typed FeaturePython)
  n = 4
  ref = H_element
FEATURE [App::DocumentObjectGroupPython] C_element134  label="C_element : 079"  # scripted group (container) (typed FeaturePython)
  n = 5
  ref = C_element
FEATURE [App::DocumentObjectGroupPython] N_element054  label="N_element : 026"  # scripted group (container) (typed FeaturePython)
  n = 5
  ref = N_element
FEATURE [App::DocumentObjectGroupPython] G4_DNA_ADENINE  # scripted group (container) (typed FeaturePython)
  Dunit = g/cm3
  Dvalue = 1
  Group = -> [H_element124,C_element134,N_element054]
  conduct = 2
  density = 1
  expand = 3
  formula = G4_DNA_ADENINE
  name = G4_DNA_ADENINE
  specific = 4
FEATURE [App::DocumentObjectGroupPython] H_element125  label="H_element : 072"  # scripted group (container) (typed FeaturePython)
  n = 4
  ref = H_element
FEATURE [App::DocumentObjectGroupPython] C_element135  label="C_element : 080"  # scripted group (container) (typed FeaturePython)
  n = 5
  ref = C_element
FEATURE [App::DocumentObjectGroupPython] N_element055  label="N_element : 027"  # scripted group (container) (typed FeaturePython)
  n = 5
  ref = N_element
FEATURE [App::DocumentObjectGroupPython] O_element116  label="O_element : 069"  # scripted group (container) (typed FeaturePython)
  n = 1
  ref = O_element
FEATURE [App::DocumentObjectGroupPython] G4_DNA_GUANINE  # scripted group (container) (typed FeaturePython)
  Dunit = g/cm3
  Dvalue = 1
  Group = -> [H_element125,C_element135,N_element055,O_element116]
  conduct = 2
  density = 1
  expand = 3
  formula = G4_DNA_GUANINE
  name = G4_DNA_GUANINE
  specific = 4
FEATURE [App::DocumentObjectGroupPython] H_element126  label="H_element : 073"  # scripted group (container) (typed FeaturePython)
  n = 4
  ref = H_element
FEATURE [App::DocumentObjectGroupPython] C_element136  label="C_element : 081"  # scripted group (container) (typed FeaturePython)
  n = 4
  ref = C_element
FEATURE [App::DocumentObjectGroupPython] N_element056  label="N_element : 028"  # scripted group (container) (typed FeaturePython)
  n = 3
  ref = N_element
FEATURE [App::DocumentObjectGroupPython] O_element117  label="O_element : 070"  # scripted group (container) (typed FeaturePython)
  n = 1
  ref = O_element
FEATURE [App::DocumentObjectGroupPython] G4_DNA_CYTOSINE  # scripted group (container) (typed FeaturePython)
  Dunit = g/cm3
  Dvalue = 1
  Group = -> [H_element126,C_element136,N_element056,O_element117]
  conduct = 2
  density = 1
  expand = 3
  formula = G4_DNA_CYTOSINE
  name = G4_DNA_CYTOSINE
  specific = 4
FEATURE [App::DocumentObjectGroupPython] H_element127  label="H_element : 074"  # scripted group (container) (typed FeaturePython)
  n = 5
  ref = H_element
FEATURE [App::DocumentObjectGroupPython] C_element137  label="C_element : 082"  # scripted group (container) (typed FeaturePython)
  n = 5
  ref = C_element
FEATURE [App::DocumentObjectGroupPython] N_element057  label="N_element : 029"  # scripted group (container) (typed FeaturePython)
  n = 2
  ref = N_element
FEATURE [App::DocumentObjectGroupPython] O_element118  label="O_element : 071"  # scripted group (container) (typed FeaturePython)
  n = 2
  ref = O_element
FEATURE [App::DocumentObjectGroupPython] G4_DNA_THYMINE  # scripted group (container) (typed FeaturePython)
  Dunit = g/cm3
  Dvalue = 1
  Group = -> [H_element127,C_element137,N_element057,O_element118]
  conduct = 2
  density = 1
  expand = 3
  formula = G4_DNA_THYMINE
  name = G4_DNA_THYMINE
  specific = 4
FEATURE [App::DocumentObjectGroupPython] H_element128  label="H_element : 075"  # scripted group (container) (typed FeaturePython)
  n = 3
  ref = H_element
FEATURE [App::DocumentObjectGroupPython] C_element138  label="C_element : 083"  # scripted group (container) (typed FeaturePython)
  n = 4
  ref = C_element
FEATURE [App::DocumentObjectGroupPython] N_element058  label="N_element : 030"  # scripted group (container) (typed FeaturePython)
  n = 2
  ref = N_element
FEATURE [App::DocumentObjectGroupPython] O_element119  label="O_element : 072"  # scripted group (container) (typed FeaturePython)
  n = 2
  ref = O_element
FEATURE [App::DocumentObjectGroupPython] G4_DNA_URACIL  # scripted group (container) (typed FeaturePython)
  Dunit = g/cm3
  Dvalue = 1
  Group = -> [H_element128,C_element138,N_element058,O_element119]
  conduct = 2
  density = 1
  expand = 3
  formula = G4_DNA_URACIL
  name = G4_DNA_URACIL
  specific = 4
FEATURE [App::DocumentObjectGroupPython] H_element129  label="H_element : 076"  # scripted group (container) (typed FeaturePython)
  n = 10
  ref = H_element
FEATURE [App::DocumentObjectGroupPython] C_element139  label="C_element : 084"  # scripted group (container) (typed FeaturePython)
  n = 10
  ref = C_element
FEATURE [App::DocumentObjectGroupPython] N_element059  label="N_element : 031"  # scripted group (container) (typed FeaturePython)
  n = 5
  ref = N_element
FEATURE [App::DocumentObjectGroupPython] O_element120  label="O_element : 073"  # scripted group (container) (typed FeaturePython)
  n = 4
  ref = O_element
FEATURE [App::DocumentObjectGroupPython] G4_DNA_ADENOSINE  # scripted group (container) (typed FeaturePython)
  Dunit = g/cm3
  Dvalue = 1
  Group = -> [H_element129,C_element139,N_element059,O_element120]
  conduct = 2
  density = 1
  expand = 3
  formula = G4_DNA_ADENOSINE
  name = G4_DNA_ADENOSINE
  specific = 4
FEATURE [App::DocumentObjectGroupPython] H_element130  label="H_element : 077"  # scripted group (container) (typed FeaturePython)
  n = 10
  ref = H_element
FEATURE [App::DocumentObjectGroupPython] C_element140  label="C_element : 085"  # scripted group (container) (typed FeaturePython)
  n = 10
  ref = C_element
FEATURE [App::DocumentObjectGroupPython] N_element060  label="N_element : 032"  # scripted group (container) (typed FeaturePython)
  n = 5
  ref = N_element
FEATURE [App::DocumentObjectGroupPython] O_element121  label="O_element : 074"  # scripted group (container) (typed FeaturePython)
  n = 5
  ref = O_element
FEATURE [App::DocumentObjectGroupPython] G4_DNA_GUANOSINE  # scripted group (container) (typed FeaturePython)
  Dunit = g/cm3
  Dvalue = 1
  Group = -> [H_element130,C_element140,N_element060,O_element121]
  conduct = 2
  density = 1
  expand = 3
  formula = G4_DNA_GUANOSINE
  name = G4_DNA_GUANOSINE
  specific = 4
FEATURE [App::DocumentObjectGroupPython] H_element131  label="H_element : 078"  # scripted group (container) (typed FeaturePython)
  n = 10
  ref = H_element
FEATURE [App::DocumentObjectGroupPython] C_element141  label="C_element : 086"  # scripted group (container) (typed FeaturePython)
  n = 9
  ref = C_element
FEATURE [App::DocumentObjectGroupPython] N_element061  label="N_element : 033"  # scripted group (container) (typed FeaturePython)
  n = 3
  ref = N_element
FEATURE [App::DocumentObjectGroupPython] O_element122  label="O_element : 075"  # scripted group (container) (typed FeaturePython)
  n = 5
  ref = O_element
FEATURE [App::DocumentObjectGroupPython] G4_DNA_CYTIDINE  # scripted group (container) (typed FeaturePython)
  Dunit = g/cm3
  Dvalue = 1
  Group = -> [H_element131,C_element141,N_element061,O_element122]
  conduct = 2
  density = 1
  expand = 3
  formula = G4_DNA_CYTIDINE
  name = G4_DNA_CYTIDINE
  specific = 4
FEATURE [App::DocumentObjectGroupPython] H_element132  label="H_element : 079"  # scripted group (container) (typed FeaturePython)
  n = 9
  ref = H_element
FEATURE [App::DocumentObjectGroupPython] C_element142  label="C_element : 087"  # scripted group (container) (typed FeaturePython)
  n = 9
  ref = C_element
FEATURE [App::DocumentObjectGroupPython] N_element062  label="N_element : 034"  # scripted group (container) (typed FeaturePython)
  n = 2
  ref = N_element
FEATURE [App::DocumentObjectGroupPython] O_element123  label="O_element : 076"  # scripted group (container) (typed FeaturePython)
  n = 6
  ref = O_element
FEATURE [App::DocumentObjectGroupPython] G4_DNA_URIDINE  # scripted group (container) (typed FeaturePython)
  Dunit = g/cm3
  Dvalue = 1
  Group = -> [H_element132,C_element142,N_element062,O_element123]
  conduct = 2
  density = 1
  expand = 3
  formula = G4_DNA_URIDINE
  name = G4_DNA_URIDINE
  specific = 4
FEATURE [App::DocumentObjectGroupPython] H_element133  label="H_element : 080"  # scripted group (container) (typed FeaturePython)
  n = 11
  ref = H_element
FEATURE [App::DocumentObjectGroupPython] C_element143  label="C_element : 088"  # scripted group (container) (typed FeaturePython)
  n = 10
  ref = C_element
FEATURE [App::DocumentObjectGroupPython] N_element063  label="N_element : 035"  # scripted group (container) (typed FeaturePython)
  n = 2
  ref = N_element
FEATURE [App::DocumentObjectGroupPython] O_element124  label="O_element : 077"  # scripted group (container) (typed FeaturePython)
  n = 6
  ref = O_element
FEATURE [App::DocumentObjectGroupPython] G4_DNA_METHYLURIDINE  # scripted group (container) (typed FeaturePython)
  Dunit = g/cm3
  Dvalue = 1
  Group = -> [H_element133,C_element143,N_element063,O_element124]
  conduct = 2
  density = 1
  expand = 3
  formula = G4_DNA_METHYLURIDINE
  name = G4_DNA_METHYLURIDINE
  specific = 4
FEATURE [App::DocumentObjectGroupPython] P_element014  label="P_element : 003"  # scripted group (container) (typed FeaturePython)
  n = 1
  ref = P_element
FEATURE [App::DocumentObjectGroupPython] O_element125  label="O_element : 078"  # scripted group (container) (typed FeaturePython)
  n = 3
  ref = O_element
FEATURE [App::DocumentObjectGroupPython] G4_DNA_MONOPHOSPHATE  # scripted group (container) (typed FeaturePython)
  Dunit = g/cm3
  Dvalue = 1
  Group = -> [P_element014,O_element125]
  conduct = 2
  density = 1
  expand = 3
  formula = G4_DNA_MONOPHOSPHATE
  name = G4_DNA_MONOPHOSPHATE
  specific = 4
FEATURE [App::DocumentObjectGroupPython] H_element134  label="H_element : 081"  # scripted group (container) (typed FeaturePython)
  n = 10
  ref = H_element
FEATURE [App::DocumentObjectGroupPython] C_element144  label="C_element : 089"  # scripted group (container) (typed FeaturePython)
  n = 10
  ref = C_element
FEATURE [App::DocumentObjectGroupPython] N_element064  label="N_element : 036"  # scripted group (container) (typed FeaturePython)
  n = 5
  ref = N_element
FEATURE [App::DocumentObjectGroupPython] O_element126  label="O_element : 079"  # scripted group (container) (typed FeaturePython)
  n = 7
  ref = O_element
FEATURE [App::DocumentObjectGroupPython] P_element015  label="P_element : 004"  # scripted group (container) (typed FeaturePython)
  n = 1
  ref = P_element
FEATURE [App::DocumentObjectGroupPython] G4_DNA_A  # scripted group (container) (typed FeaturePython)
  Dunit = g/cm3
  Dvalue = 1
  Group = -> [H_element134,C_element144,N_element064,O_element126,P_element015]
  conduct = 2
  density = 1
  expand = 3
  formula = G4_DNA_A
  name = G4_DNA_A
  specific = 4
FEATURE [App::DocumentObjectGroupPython] H_element135  label="H_element : 082"  # scripted group (container) (typed FeaturePython)
  n = 10
  ref = H_element
FEATURE [App::DocumentObjectGroupPython] C_element145  label="C_element : 090"  # scripted group (container) (typed FeaturePython)
  n = 10
  ref = C_element
FEATURE [App::DocumentObjectGroupPython] N_element065  label="N_element : 037"  # scripted group (container) (typed FeaturePython)
  n = 5
  ref = N_element
FEATURE [App::DocumentObjectGroupPython] O_element127  label="O_element : 8"  # scripted group (container) (typed FeaturePython)
  n = 8
  ref = O_element
FEATURE [App::DocumentObjectGroupPython] P_element016  label="P_element : 005"  # scripted group (container) (typed FeaturePython)
  n = 1
  ref = P_element
FEATURE [App::DocumentObjectGroupPython] G4_DNA_G  # scripted group (container) (typed FeaturePython)
  Dunit = g/cm3
  Dvalue = 1
  Group = -> [H_element135,C_element145,N_element065,O_element127,P_element016]
  conduct = 2
  density = 1
  expand = 3
  formula = G4_DNA_G
  name = G4_DNA_G
  specific = 4
FEATURE [App::DocumentObjectGroupPython] H_element136  label="H_element : 083"  # scripted group (container) (typed FeaturePython)
  n = 10
  ref = H_element
FEATURE [App::DocumentObjectGroupPython] C_element146  label="C_element : 091"  # scripted group (container) (typed FeaturePython)
  n = 9
  ref = C_element
FEATURE [App::DocumentObjectGroupPython] N_element066  label="N_element : 038"  # scripted group (container) (typed FeaturePython)
  n = 3
  ref = N_element
FEATURE [App::DocumentObjectGroupPython] O_element128  label="O_element : 080"  # scripted group (container) (typed FeaturePython)
  n = 8
  ref = O_element
FEATURE [App::DocumentObjectGroupPython] P_element017  label="P_element : 006"  # scripted group (container) (typed FeaturePython)
  n = 1
  ref = P_element
FEATURE [App::DocumentObjectGroupPython] G4_DNA_C  # scripted group (container) (typed FeaturePython)
  Dunit = g/cm3
  Dvalue = 1
  Group = -> [H_element136,C_element146,N_element066,O_element128,P_element017]
  conduct = 2
  density = 1
  expand = 3
  formula = G4_DNA_C
  name = G4_DNA_C
  specific = 4
FEATURE [App::DocumentObjectGroupPython] H_element137  label="H_element : 084"  # scripted group (container) (typed FeaturePython)
  n = 9
  ref = H_element
FEATURE [App::DocumentObjectGroupPython] C_element147  label="C_element : 092"  # scripted group (container) (typed FeaturePython)
  n = 9
  ref = C_element
FEATURE [App::DocumentObjectGroupPython] N_element067  label="N_element : 039"  # scripted group (container) (typed FeaturePython)
  n = 2
  ref = N_element
FEATURE [App::DocumentObjectGroupPython] O_element129  label="O_element : 9"  # scripted group (container) (typed FeaturePython)
  n = 9
  ref = O_element
FEATURE [App::DocumentObjectGroupPython] P_element018  label="P_element : 007"  # scripted group (container) (typed FeaturePython)
  n = 1
  ref = P_element
FEATURE [App::DocumentObjectGroupPython] G4_DNA_U  # scripted group (container) (typed FeaturePython)
  Dunit = g/cm3
  Dvalue = 1
  Group = -> [H_element137,C_element147,N_element067,O_element129,P_element018]
  conduct = 2
  density = 1
  expand = 3
  formula = G4_DNA_U
  name = G4_DNA_U
  specific = 4
FEATURE [App::DocumentObjectGroupPython] H_element138  label="H_element : 085"  # scripted group (container) (typed FeaturePython)
  n = 11
  ref = H_element
FEATURE [App::DocumentObjectGroupPython] C_element148  label="C_element : 093"  # scripted group (container) (typed FeaturePython)
  n = 10
  ref = C_element
FEATURE [App::DocumentObjectGroupPython] N_element068  label="N_element : 040"  # scripted group (container) (typed FeaturePython)
  n = 2
  ref = N_element
FEATURE [App::DocumentObjectGroupPython] O_element130  label="O_element : 081"  # scripted group (container) (typed FeaturePython)
  n = 9
  ref = O_element
FEATURE [App::DocumentObjectGroupPython] P_element019  label="P_element : 008"  # scripted group (container) (typed FeaturePython)
  n = 1
  ref = P_element
FEATURE [App::DocumentObjectGroupPython] G4_DNA_MU  # scripted group (container) (typed FeaturePython)
  Dunit = g/cm3
  Dvalue = 1
  Group = -> [H_element138,C_element148,N_element068,O_element130,P_element019]
  conduct = 2
  density = 1
  expand = 3
  formula = G4_DNA_MU
  name = G4_DNA_MU
  specific = 4
FEATURE [App::DocumentObjectGroupPython] BioChemical  # scripted group (container) (typed FeaturePython)
  Group = -> [G4_CYTOSINE,G4_THYMINE,G4_URACIL,G4_DNA_ADENINE,G4_DNA_GUANINE,G4_DNA_CYTOSINE,G4_DNA_THYMINE,G4_DNA_URACIL,G4_DNA_ADENOSINE,G4_DNA_GUANOSINE,G4_DNA_CYTIDINE,G4_DNA_URIDINE,G4_DNA_METHYLURIDINE,G4_DNA_MONOPHOSPHATE,G4_DNA_A,G4_DNA_G,G4_DNA_C,G4_DNA_U,G4_DNA_MU]
FEATURE [App::DocumentObjectGroupPython] G4Materials  # scripted group (container) (typed FeaturePython)
  Group = -> [NIST,Element,HEP,Space,BioChemical]
  version = 1
FEATURE [App::DocumentObjectGroupPython] Geant4  # scripted group (container) (typed FeaturePython)
  Group = -> [G4Isotopes,G4Elements,G4Materials]
FEATURE [App::DocumentObjectGroupPython] Materials  # scripted group (container) (typed FeaturePython)
  Group = -> [Geant4]
FEATURE [Part::FeaturePython] GDMLBox_WorldBox  # WARN: FeaturePython — macro-defined, semantics opaque (R4)
  lunit = 2
  material = 5
  x = 100
  y = 100
  z = 100
FEATURE [Sketcher::SketchObject] Sketch
  FullyConstrained = false
  sketch-geometry (15):
    g0-g5: Circle x6 (B-spline internal-alignment scaffolding for g6; pole/knot coordinates omitted)
    g6: BSplineCurve PolesCount=7 KnotsCount=5 Degree=3 IsPeriodic=0
    g7-g10: GeomPoint x4 (B-spline internal-alignment scaffolding for g6; pole/knot coordinates omitted)
    g11: LineSegment StartX=-4.39557 StartY=8.39124 StartZ=0 EndX=-5.2662 EndY=10.5884 EndZ=0
    g12: LineSegment StartX=-5.2662 StartY=10.5884 StartZ=0 EndX=-7.82152 EndY=9.89481 EndZ=0
    g13: LineSegment StartX=-7.82152 StartY=9.89481 StartZ=0 EndX=-9.50073 EndY=7.63152 EndZ=0
    g14: ArcOfCircle CenterX=-7.8377 CenterY=5.34547 CenterZ=0 NormalX=0 NormalY=0 NormalZ=1 AngleXU=0 Radius=2.82696 StartAngle=4.84147 EndAngle=8.48291
  constraints (9):
    c: Weight(g0) = 1
    c: Equal(g0, g1-g5) x5
    c: InternalAlignment(g0-g5 -> g6) x6
    c: InternalAlignment(g7-g10 -> g6) x4
    c: Coincident(g11,g6)
    c: Coincident(g11,g12)
    c: Coincident(g12,g13)
    c: Coincident(g14,g13)
    c: Coincident(g14,g6)
FEATURE [Part::Extrusion] Extrude
  Base = -> Sketch
  Dir = (0,0,1)
  DirMode = 2
  FaceMakerClass = Part::FaceMakerBullseye
  LengthFwd = 10
  LengthRev = 0
  Placement = pos=(13,12,0) rot=(0,0,1;0rad)
  Solid = true
  Symmetric = false
  material = 1
FEATURE [Part::Mirroring] Part__Mirroring  label="mirror1"
  Base = (0,0,0)
  Normal = (1,0,0)
  Placement = pos=(0,21,0) rot=(0,0,1;0rad)
  Source = -> Extrude
  material = 261
FEATURE [Part::Mirroring] Part__Mirroring002  label="mirror2"
  Base = (0,0,0)
  Normal = (0,1,0)
  Placement = pos=(-10,0,0) rot=(0,0,1;0rad)
  Source = -> Part__Mirroring
FEATURE [App::Part] Part
  Group = -> [Sketch,Extrude,Part__Mirroring,Part__Mirroring002]
  Origin = -> Origin001
FEATURE [App::Part] worldVOL
  Group = -> [GDMLBox_WorldBox,Part]
  Origin = -> Origin
